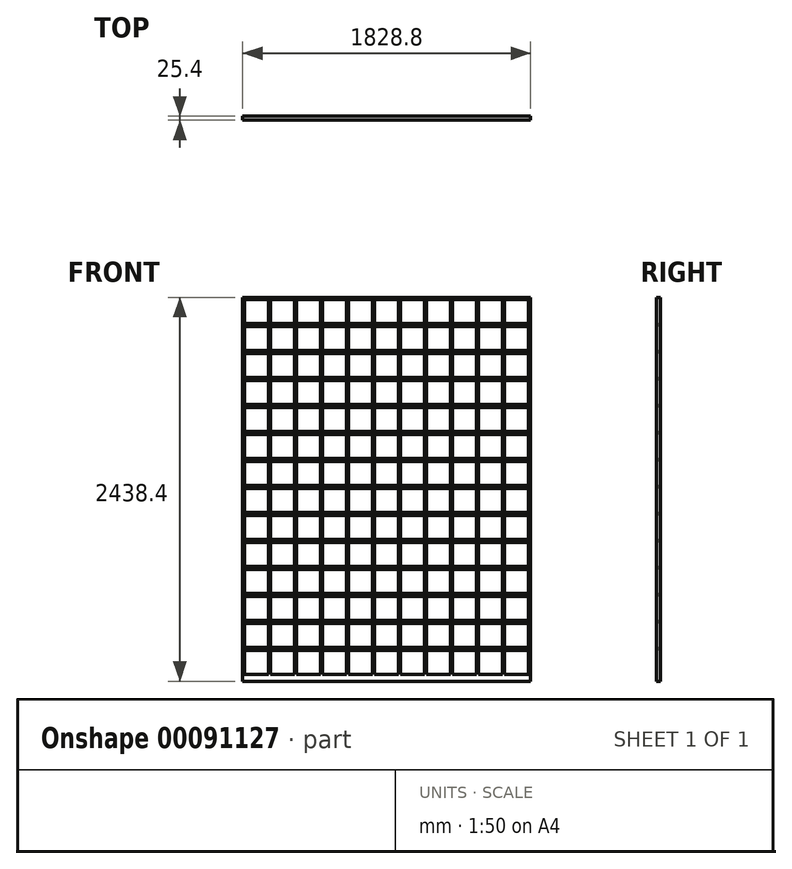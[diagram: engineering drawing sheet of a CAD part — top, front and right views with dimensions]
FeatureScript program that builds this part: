
annotation { "Feature Type Name" : "Feature", "Feature Type Description" : "" }
export const myFeature = defineFeature(function(context is Context, id is Id, definition is map)
    precondition{}
    {
        {
            var Q0;
            Q0=qCreatedBy(makeId("Front.planeOp"),FACE);
            var sketch = newSketch(context, id + "F0", { "sketchPlane" : qUnion([Q0])});
            skLineSegment(sketch, "E0.bottom", {"start": v(-98.4, 2369.27) * mm, "end": v(1730.4, 2369.27) * mm});
            skLineSegment(sketch, "E0.top", {"start": v(-98.4, -69.13) * mm, "end": v(1730.4, -69.13) * mm});
            skLineSegment(sketch, "E0.left", {"start": v(-98.4, 2369.27) * mm, "end": v(-98.4, -69.13) * mm});
            skLineSegment(sketch, "E0.right", {"start": v(1730.4, 2369.27) * mm, "end": v(1730.4, -69.13) * mm});
            skSolve(sketch);
        }
        {
            var Q0;
            Q0 = qSketchRegion(id + "F0", true);
            extrude(context, id + "F1", {"entities" : qUnion([Q0]), "depth" : 25.4 * mm});
        }
        {
            var Q0;
            Q0=makeQuery(id+"F1.opExtrude","CAP_FACE",FACE,{"disambiguationData":[OSD([sQuery(id+"F0.wireOp",EDGE,"E0.bottom"),sQuery(id+"F0.wireOp",EDGE,"E0.top"),sQuery(id+"F0.wireOp",EDGE,"E0.left"),sQuery(id+"F0.wireOp",EDGE,"E0.right")])],"isStart":false});
            var sketch = newSketch(context, id + "F2", { "sketchPlane" : qUnion([Q0])});
            skLineSegment(sketch, "E1.bottom", {"start": v(-85.7, 2356.57) * mm, "end": v(66.7, 2356.57) * mm});
            skLineSegment(sketch, "E1.top", {"start": v(-85.7, 2204.17) * mm, "end": v(66.7, 2204.17) * mm});
            skLineSegment(sketch, "E1.left", {"start": v(-85.7, 2356.57) * mm, "end": v(-85.7, 2204.17) * mm});
            skLineSegment(sketch, "E1.right", {"start": v(66.7, 2356.57) * mm, "end": v(66.7, 2204.17) * mm});
            skLineSegment(sketch, "E2.0.1.0", {"start": v(66.7, 2185.12) * mm, "end": v(66.7, 2032.72) * mm});
            skLineSegment(sketch, "E2.0.1.1", {"start": v(-85.7, 2185.12) * mm, "end": v(66.7, 2185.12) * mm});
            skLineSegment(sketch, "E2.0.1.2", {"start": v(-85.7, 2185.12) * mm, "end": v(-85.7, 2032.72) * mm});
            skLineSegment(sketch, "E2.0.1.3", {"start": v(-85.7, 2032.72) * mm, "end": v(66.7, 2032.72) * mm});
            skLineSegment(sketch, "E2.0.2.0", {"start": v(66.7, 2013.67) * mm, "end": v(66.7, 1861.27) * mm});
            skLineSegment(sketch, "E2.0.2.1", {"start": v(-85.7, 2013.67) * mm, "end": v(66.7, 2013.67) * mm});
            skLineSegment(sketch, "E2.0.2.2", {"start": v(-85.7, 2013.67) * mm, "end": v(-85.7, 1861.27) * mm});
            skLineSegment(sketch, "E2.0.2.3", {"start": v(-85.7, 1861.27) * mm, "end": v(66.7, 1861.27) * mm});
            skLineSegment(sketch, "E2.0.3.0", {"start": v(66.7, 1842.22) * mm, "end": v(66.7, 1689.82) * mm});
            skLineSegment(sketch, "E2.0.3.1", {"start": v(-85.7, 1842.22) * mm, "end": v(66.7, 1842.22) * mm});
            skLineSegment(sketch, "E2.0.3.2", {"start": v(-85.7, 1842.22) * mm, "end": v(-85.7, 1689.82) * mm});
            skLineSegment(sketch, "E2.0.3.3", {"start": v(-85.7, 1689.82) * mm, "end": v(66.7, 1689.82) * mm});
            skLineSegment(sketch, "E2.0.4.0", {"start": v(66.7, 1670.77) * mm, "end": v(66.7, 1518.37) * mm});
            skLineSegment(sketch, "E2.0.4.1", {"start": v(-85.7, 1670.77) * mm, "end": v(66.7, 1670.77) * mm});
            skLineSegment(sketch, "E2.0.4.2", {"start": v(-85.7, 1670.77) * mm, "end": v(-85.7, 1518.37) * mm});
            skLineSegment(sketch, "E2.0.4.3", {"start": v(-85.7, 1518.37) * mm, "end": v(66.7, 1518.37) * mm});
            skLineSegment(sketch, "E2.0.5.0", {"start": v(66.7, 1499.32) * mm, "end": v(66.7, 1346.92) * mm});
            skLineSegment(sketch, "E2.0.5.1", {"start": v(-85.7, 1499.32) * mm, "end": v(66.7, 1499.32) * mm});
            skLineSegment(sketch, "E2.0.5.2", {"start": v(-85.7, 1499.32) * mm, "end": v(-85.7, 1346.92) * mm});
            skLineSegment(sketch, "E2.0.5.3", {"start": v(-85.7, 1346.92) * mm, "end": v(66.7, 1346.92) * mm});
            skLineSegment(sketch, "E2.0.6.0", {"start": v(66.7, 1327.87) * mm, "end": v(66.7, 1175.47) * mm});
            skLineSegment(sketch, "E2.0.6.1", {"start": v(-85.7, 1327.87) * mm, "end": v(66.7, 1327.87) * mm});
            skLineSegment(sketch, "E2.0.6.2", {"start": v(-85.7, 1327.87) * mm, "end": v(-85.7, 1175.47) * mm});
            skLineSegment(sketch, "E2.0.6.3", {"start": v(-85.7, 1175.47) * mm, "end": v(66.7, 1175.47) * mm});
            skLineSegment(sketch, "E2.0.7.0", {"start": v(66.7, 1156.42) * mm, "end": v(66.7, 1004.02) * mm});
            skLineSegment(sketch, "E2.0.7.1", {"start": v(-85.7, 1156.42) * mm, "end": v(66.7, 1156.42) * mm});
            skLineSegment(sketch, "E2.0.7.2", {"start": v(-85.7, 1156.42) * mm, "end": v(-85.7, 1004.02) * mm});
            skLineSegment(sketch, "E2.0.7.3", {"start": v(-85.7, 1004.02) * mm, "end": v(66.7, 1004.02) * mm});
            skLineSegment(sketch, "E2.1.0.0", {"start": v(231.8, 2356.57) * mm, "end": v(231.8, 2204.17) * mm});
            skLineSegment(sketch, "E2.1.0.1", {"start": v(79.4, 2356.57) * mm, "end": v(231.8, 2356.57) * mm});
            skLineSegment(sketch, "E2.1.0.2", {"start": v(79.4, 2356.57) * mm, "end": v(79.4, 2204.17) * mm});
            skLineSegment(sketch, "E2.1.0.3", {"start": v(79.4, 2204.17) * mm, "end": v(231.8, 2204.17) * mm});
            skLineSegment(sketch, "E2.1.1.0", {"start": v(231.8, 2185.12) * mm, "end": v(231.8, 2032.72) * mm});
            skLineSegment(sketch, "E2.1.1.1", {"start": v(79.4, 2185.12) * mm, "end": v(231.8, 2185.12) * mm});
            skLineSegment(sketch, "E2.1.1.2", {"start": v(79.4, 2185.12) * mm, "end": v(79.4, 2032.72) * mm});
            skLineSegment(sketch, "E2.1.1.3", {"start": v(79.4, 2032.72) * mm, "end": v(231.8, 2032.72) * mm});
            skLineSegment(sketch, "E2.1.2.0", {"start": v(231.8, 2013.67) * mm, "end": v(231.8, 1861.27) * mm});
            skLineSegment(sketch, "E2.1.2.1", {"start": v(79.4, 2013.67) * mm, "end": v(231.8, 2013.67) * mm});
            skLineSegment(sketch, "E2.1.2.2", {"start": v(79.4, 2013.67) * mm, "end": v(79.4, 1861.27) * mm});
            skLineSegment(sketch, "E2.1.2.3", {"start": v(79.4, 1861.27) * mm, "end": v(231.8, 1861.27) * mm});
            skLineSegment(sketch, "E2.1.3.0", {"start": v(231.8, 1842.22) * mm, "end": v(231.8, 1689.82) * mm});
            skLineSegment(sketch, "E2.1.3.1", {"start": v(79.4, 1842.22) * mm, "end": v(231.8, 1842.22) * mm});
            skLineSegment(sketch, "E2.1.3.2", {"start": v(79.4, 1842.22) * mm, "end": v(79.4, 1689.82) * mm});
            skLineSegment(sketch, "E2.1.3.3", {"start": v(79.4, 1689.82) * mm, "end": v(231.8, 1689.82) * mm});
            skLineSegment(sketch, "E2.1.4.0", {"start": v(231.8, 1670.77) * mm, "end": v(231.8, 1518.37) * mm});
            skLineSegment(sketch, "E2.1.4.1", {"start": v(79.4, 1670.77) * mm, "end": v(231.8, 1670.77) * mm});
            skLineSegment(sketch, "E2.1.4.2", {"start": v(79.4, 1670.77) * mm, "end": v(79.4, 1518.37) * mm});
            skLineSegment(sketch, "E2.1.4.3", {"start": v(79.4, 1518.37) * mm, "end": v(231.8, 1518.37) * mm});
            skLineSegment(sketch, "E2.1.5.0", {"start": v(231.8, 1499.32) * mm, "end": v(231.8, 1346.92) * mm});
            skLineSegment(sketch, "E2.1.5.1", {"start": v(79.4, 1499.32) * mm, "end": v(231.8, 1499.32) * mm});
            skLineSegment(sketch, "E2.1.5.2", {"start": v(79.4, 1499.32) * mm, "end": v(79.4, 1346.92) * mm});
            skLineSegment(sketch, "E2.1.5.3", {"start": v(79.4, 1346.92) * mm, "end": v(231.8, 1346.92) * mm});
            skLineSegment(sketch, "E2.1.6.0", {"start": v(231.8, 1327.87) * mm, "end": v(231.8, 1175.47) * mm});
            skLineSegment(sketch, "E2.1.6.1", {"start": v(79.4, 1327.87) * mm, "end": v(231.8, 1327.87) * mm});
            skLineSegment(sketch, "E2.1.6.2", {"start": v(79.4, 1327.87) * mm, "end": v(79.4, 1175.47) * mm});
            skLineSegment(sketch, "E2.1.6.3", {"start": v(79.4, 1175.47) * mm, "end": v(231.8, 1175.47) * mm});
            skLineSegment(sketch, "E2.1.7.0", {"start": v(231.8, 1156.42) * mm, "end": v(231.8, 1004.02) * mm});
            skLineSegment(sketch, "E2.1.7.1", {"start": v(79.4, 1156.42) * mm, "end": v(231.8, 1156.42) * mm});
            skLineSegment(sketch, "E2.1.7.2", {"start": v(79.4, 1156.42) * mm, "end": v(79.4, 1004.02) * mm});
            skLineSegment(sketch, "E2.1.7.3", {"start": v(79.4, 1004.02) * mm, "end": v(231.8, 1004.02) * mm});
            skLineSegment(sketch, "E2.2.0.0", {"start": v(396.9, 2356.57) * mm, "end": v(396.9, 2204.17) * mm});
            skLineSegment(sketch, "E2.2.0.1", {"start": v(244.5, 2356.57) * mm, "end": v(396.9, 2356.57) * mm});
            skLineSegment(sketch, "E2.2.0.2", {"start": v(244.5, 2356.57) * mm, "end": v(244.5, 2204.17) * mm});
            skLineSegment(sketch, "E2.2.0.3", {"start": v(244.5, 2204.17) * mm, "end": v(396.9, 2204.17) * mm});
            skLineSegment(sketch, "E2.2.1.0", {"start": v(396.9, 2185.12) * mm, "end": v(396.9, 2032.72) * mm});
            skLineSegment(sketch, "E2.2.1.1", {"start": v(244.5, 2185.12) * mm, "end": v(396.9, 2185.12) * mm});
            skLineSegment(sketch, "E2.2.1.2", {"start": v(244.5, 2185.12) * mm, "end": v(244.5, 2032.72) * mm});
            skLineSegment(sketch, "E2.2.1.3", {"start": v(244.5, 2032.72) * mm, "end": v(396.9, 2032.72) * mm});
            skLineSegment(sketch, "E2.2.2.0", {"start": v(396.9, 2013.67) * mm, "end": v(396.9, 1861.27) * mm});
            skLineSegment(sketch, "E2.2.2.1", {"start": v(244.5, 2013.67) * mm, "end": v(396.9, 2013.67) * mm});
            skLineSegment(sketch, "E2.2.2.2", {"start": v(244.5, 2013.67) * mm, "end": v(244.5, 1861.27) * mm});
            skLineSegment(sketch, "E2.2.2.3", {"start": v(244.5, 1861.27) * mm, "end": v(396.9, 1861.27) * mm});
            skLineSegment(sketch, "E2.2.3.0", {"start": v(396.9, 1842.22) * mm, "end": v(396.9, 1689.82) * mm});
            skLineSegment(sketch, "E2.2.3.1", {"start": v(244.5, 1842.22) * mm, "end": v(396.9, 1842.22) * mm});
            skLineSegment(sketch, "E2.2.3.2", {"start": v(244.5, 1842.22) * mm, "end": v(244.5, 1689.82) * mm});
            skLineSegment(sketch, "E2.2.3.3", {"start": v(244.5, 1689.82) * mm, "end": v(396.9, 1689.82) * mm});
            skLineSegment(sketch, "E2.2.4.0", {"start": v(396.9, 1670.77) * mm, "end": v(396.9, 1518.37) * mm});
            skLineSegment(sketch, "E2.2.4.1", {"start": v(244.5, 1670.77) * mm, "end": v(396.9, 1670.77) * mm});
            skLineSegment(sketch, "E2.2.4.2", {"start": v(244.5, 1670.77) * mm, "end": v(244.5, 1518.37) * mm});
            skLineSegment(sketch, "E2.2.4.3", {"start": v(244.5, 1518.37) * mm, "end": v(396.9, 1518.37) * mm});
            skLineSegment(sketch, "E2.2.5.0", {"start": v(396.9, 1499.32) * mm, "end": v(396.9, 1346.92) * mm});
            skLineSegment(sketch, "E2.2.5.1", {"start": v(244.5, 1499.32) * mm, "end": v(396.9, 1499.32) * mm});
            skLineSegment(sketch, "E2.2.5.2", {"start": v(244.5, 1499.32) * mm, "end": v(244.5, 1346.92) * mm});
            skLineSegment(sketch, "E2.2.5.3", {"start": v(244.5, 1346.92) * mm, "end": v(396.9, 1346.92) * mm});
            skLineSegment(sketch, "E2.2.6.0", {"start": v(396.9, 1327.87) * mm, "end": v(396.9, 1175.47) * mm});
            skLineSegment(sketch, "E2.2.6.1", {"start": v(244.5, 1327.87) * mm, "end": v(396.9, 1327.87) * mm});
            skLineSegment(sketch, "E2.2.6.2", {"start": v(244.5, 1327.87) * mm, "end": v(244.5, 1175.47) * mm});
            skLineSegment(sketch, "E2.2.6.3", {"start": v(244.5, 1175.47) * mm, "end": v(396.9, 1175.47) * mm});
            skLineSegment(sketch, "E2.2.7.0", {"start": v(396.9, 1156.42) * mm, "end": v(396.9, 1004.02) * mm});
            skLineSegment(sketch, "E2.2.7.1", {"start": v(244.5, 1156.42) * mm, "end": v(396.9, 1156.42) * mm});
            skLineSegment(sketch, "E2.2.7.2", {"start": v(244.5, 1156.42) * mm, "end": v(244.5, 1004.02) * mm});
            skLineSegment(sketch, "E2.2.7.3", {"start": v(244.5, 1004.02) * mm, "end": v(396.9, 1004.02) * mm});
            skLineSegment(sketch, "E2.3.0.0", {"start": v(562, 2356.57) * mm, "end": v(562, 2204.17) * mm});
            skLineSegment(sketch, "E2.3.0.1", {"start": v(409.6, 2356.57) * mm, "end": v(562, 2356.57) * mm});
            skLineSegment(sketch, "E2.3.0.2", {"start": v(409.6, 2356.57) * mm, "end": v(409.6, 2204.17) * mm});
            skLineSegment(sketch, "E2.3.0.3", {"start": v(409.6, 2204.17) * mm, "end": v(562, 2204.17) * mm});
            skLineSegment(sketch, "E2.3.1.0", {"start": v(562, 2185.12) * mm, "end": v(562, 2032.72) * mm});
            skLineSegment(sketch, "E2.3.1.1", {"start": v(409.6, 2185.12) * mm, "end": v(562, 2185.12) * mm});
            skLineSegment(sketch, "E2.3.1.2", {"start": v(409.6, 2185.12) * mm, "end": v(409.6, 2032.72) * mm});
            skLineSegment(sketch, "E2.3.1.3", {"start": v(409.6, 2032.72) * mm, "end": v(562, 2032.72) * mm});
            skLineSegment(sketch, "E2.3.2.0", {"start": v(562, 2013.67) * mm, "end": v(562, 1861.27) * mm});
            skLineSegment(sketch, "E2.3.2.1", {"start": v(409.6, 2013.67) * mm, "end": v(562, 2013.67) * mm});
            skLineSegment(sketch, "E2.3.2.2", {"start": v(409.6, 2013.67) * mm, "end": v(409.6, 1861.27) * mm});
            skLineSegment(sketch, "E2.3.2.3", {"start": v(409.6, 1861.27) * mm, "end": v(562, 1861.27) * mm});
            skLineSegment(sketch, "E2.3.3.0", {"start": v(562, 1842.22) * mm, "end": v(562, 1689.82) * mm});
            skLineSegment(sketch, "E2.3.3.1", {"start": v(409.6, 1842.22) * mm, "end": v(562, 1842.22) * mm});
            skLineSegment(sketch, "E2.3.3.2", {"start": v(409.6, 1842.22) * mm, "end": v(409.6, 1689.82) * mm});
            skLineSegment(sketch, "E2.3.3.3", {"start": v(409.6, 1689.82) * mm, "end": v(562, 1689.82) * mm});
            skLineSegment(sketch, "E2.3.4.0", {"start": v(562, 1670.77) * mm, "end": v(562, 1518.37) * mm});
            skLineSegment(sketch, "E2.3.4.1", {"start": v(409.6, 1670.77) * mm, "end": v(562, 1670.77) * mm});
            skLineSegment(sketch, "E2.3.4.2", {"start": v(409.6, 1670.77) * mm, "end": v(409.6, 1518.37) * mm});
            skLineSegment(sketch, "E2.3.4.3", {"start": v(409.6, 1518.37) * mm, "end": v(562, 1518.37) * mm});
            skLineSegment(sketch, "E2.3.5.0", {"start": v(562, 1499.32) * mm, "end": v(562, 1346.92) * mm});
            skLineSegment(sketch, "E2.3.5.1", {"start": v(409.6, 1499.32) * mm, "end": v(562, 1499.32) * mm});
            skLineSegment(sketch, "E2.3.5.2", {"start": v(409.6, 1499.32) * mm, "end": v(409.6, 1346.92) * mm});
            skLineSegment(sketch, "E2.3.5.3", {"start": v(409.6, 1346.92) * mm, "end": v(562, 1346.92) * mm});
            skLineSegment(sketch, "E2.3.6.0", {"start": v(562, 1327.87) * mm, "end": v(562, 1175.47) * mm});
            skLineSegment(sketch, "E2.3.6.1", {"start": v(409.6, 1327.87) * mm, "end": v(562, 1327.87) * mm});
            skLineSegment(sketch, "E2.3.6.2", {"start": v(409.6, 1327.87) * mm, "end": v(409.6, 1175.47) * mm});
            skLineSegment(sketch, "E2.3.6.3", {"start": v(409.6, 1175.47) * mm, "end": v(562, 1175.47) * mm});
            skLineSegment(sketch, "E2.3.7.0", {"start": v(562, 1156.42) * mm, "end": v(562, 1004.02) * mm});
            skLineSegment(sketch, "E2.3.7.1", {"start": v(409.6, 1156.42) * mm, "end": v(562, 1156.42) * mm});
            skLineSegment(sketch, "E2.3.7.2", {"start": v(409.6, 1156.42) * mm, "end": v(409.6, 1004.02) * mm});
            skLineSegment(sketch, "E2.3.7.3", {"start": v(409.6, 1004.02) * mm, "end": v(562, 1004.02) * mm});
            skLineSegment(sketch, "E2.4.0.0", {"start": v(727.1, 2356.57) * mm, "end": v(727.1, 2204.17) * mm});
            skLineSegment(sketch, "E2.4.0.1", {"start": v(574.7, 2356.57) * mm, "end": v(727.1, 2356.57) * mm});
            skLineSegment(sketch, "E2.4.0.2", {"start": v(574.7, 2356.57) * mm, "end": v(574.7, 2204.17) * mm});
            skLineSegment(sketch, "E2.4.0.3", {"start": v(574.7, 2204.17) * mm, "end": v(727.1, 2204.17) * mm});
            skLineSegment(sketch, "E2.4.1.0", {"start": v(727.1, 2185.12) * mm, "end": v(727.1, 2032.72) * mm});
            skLineSegment(sketch, "E2.4.1.1", {"start": v(574.7, 2185.12) * mm, "end": v(727.1, 2185.12) * mm});
            skLineSegment(sketch, "E2.4.1.2", {"start": v(574.7, 2185.12) * mm, "end": v(574.7, 2032.72) * mm});
            skLineSegment(sketch, "E2.4.1.3", {"start": v(574.7, 2032.72) * mm, "end": v(727.1, 2032.72) * mm});
            skLineSegment(sketch, "E2.4.2.0", {"start": v(727.1, 2013.67) * mm, "end": v(727.1, 1861.27) * mm});
            skLineSegment(sketch, "E2.4.2.1", {"start": v(574.7, 2013.67) * mm, "end": v(727.1, 2013.67) * mm});
            skLineSegment(sketch, "E2.4.2.2", {"start": v(574.7, 2013.67) * mm, "end": v(574.7, 1861.27) * mm});
            skLineSegment(sketch, "E2.4.2.3", {"start": v(574.7, 1861.27) * mm, "end": v(727.1, 1861.27) * mm});
            skLineSegment(sketch, "E2.4.3.0", {"start": v(727.1, 1842.22) * mm, "end": v(727.1, 1689.82) * mm});
            skLineSegment(sketch, "E2.4.3.1", {"start": v(574.7, 1842.22) * mm, "end": v(727.1, 1842.22) * mm});
            skLineSegment(sketch, "E2.4.3.2", {"start": v(574.7, 1842.22) * mm, "end": v(574.7, 1689.82) * mm});
            skLineSegment(sketch, "E2.4.3.3", {"start": v(574.7, 1689.82) * mm, "end": v(727.1, 1689.82) * mm});
            skLineSegment(sketch, "E2.4.4.0", {"start": v(727.1, 1670.77) * mm, "end": v(727.1, 1518.37) * mm});
            skLineSegment(sketch, "E2.4.4.1", {"start": v(574.7, 1670.77) * mm, "end": v(727.1, 1670.77) * mm});
            skLineSegment(sketch, "E2.4.4.2", {"start": v(574.7, 1670.77) * mm, "end": v(574.7, 1518.37) * mm});
            skLineSegment(sketch, "E2.4.4.3", {"start": v(574.7, 1518.37) * mm, "end": v(727.1, 1518.37) * mm});
            skLineSegment(sketch, "E2.4.5.0", {"start": v(727.1, 1499.32) * mm, "end": v(727.1, 1346.92) * mm});
            skLineSegment(sketch, "E2.4.5.1", {"start": v(574.7, 1499.32) * mm, "end": v(727.1, 1499.32) * mm});
            skLineSegment(sketch, "E2.4.5.2", {"start": v(574.7, 1499.32) * mm, "end": v(574.7, 1346.92) * mm});
            skLineSegment(sketch, "E2.4.5.3", {"start": v(574.7, 1346.92) * mm, "end": v(727.1, 1346.92) * mm});
            skLineSegment(sketch, "E2.4.6.0", {"start": v(727.1, 1327.87) * mm, "end": v(727.1, 1175.47) * mm});
            skLineSegment(sketch, "E2.4.6.1", {"start": v(574.7, 1327.87) * mm, "end": v(727.1, 1327.87) * mm});
            skLineSegment(sketch, "E2.4.6.2", {"start": v(574.7, 1327.87) * mm, "end": v(574.7, 1175.47) * mm});
            skLineSegment(sketch, "E2.4.6.3", {"start": v(574.7, 1175.47) * mm, "end": v(727.1, 1175.47) * mm});
            skLineSegment(sketch, "E2.4.7.0", {"start": v(727.1, 1156.42) * mm, "end": v(727.1, 1004.02) * mm});
            skLineSegment(sketch, "E2.4.7.1", {"start": v(574.7, 1156.42) * mm, "end": v(727.1, 1156.42) * mm});
            skLineSegment(sketch, "E2.4.7.2", {"start": v(574.7, 1156.42) * mm, "end": v(574.7, 1004.02) * mm});
            skLineSegment(sketch, "E2.4.7.3", {"start": v(574.7, 1004.02) * mm, "end": v(727.1, 1004.02) * mm});
            skLineSegment(sketch, "E2.5.0.0", {"start": v(892.2, 2356.57) * mm, "end": v(892.2, 2204.17) * mm});
            skLineSegment(sketch, "E2.5.0.1", {"start": v(739.8, 2356.57) * mm, "end": v(892.2, 2356.57) * mm});
            skLineSegment(sketch, "E2.5.0.2", {"start": v(739.8, 2356.57) * mm, "end": v(739.8, 2204.17) * mm});
            skLineSegment(sketch, "E2.5.0.3", {"start": v(739.8, 2204.17) * mm, "end": v(892.2, 2204.17) * mm});
            skLineSegment(sketch, "E2.5.1.0", {"start": v(892.2, 2185.12) * mm, "end": v(892.2, 2032.72) * mm});
            skLineSegment(sketch, "E2.5.1.1", {"start": v(739.8, 2185.12) * mm, "end": v(892.2, 2185.12) * mm});
            skLineSegment(sketch, "E2.5.1.2", {"start": v(739.8, 2185.12) * mm, "end": v(739.8, 2032.72) * mm});
            skLineSegment(sketch, "E2.5.1.3", {"start": v(739.8, 2032.72) * mm, "end": v(892.2, 2032.72) * mm});
            skLineSegment(sketch, "E2.5.2.0", {"start": v(892.2, 2013.67) * mm, "end": v(892.2, 1861.27) * mm});
            skLineSegment(sketch, "E2.5.2.1", {"start": v(739.8, 2013.67) * mm, "end": v(892.2, 2013.67) * mm});
            skLineSegment(sketch, "E2.5.2.2", {"start": v(739.8, 2013.67) * mm, "end": v(739.8, 1861.27) * mm});
            skLineSegment(sketch, "E2.5.2.3", {"start": v(739.8, 1861.27) * mm, "end": v(892.2, 1861.27) * mm});
            skLineSegment(sketch, "E2.5.3.0", {"start": v(892.2, 1842.22) * mm, "end": v(892.2, 1689.82) * mm});
            skLineSegment(sketch, "E2.5.3.1", {"start": v(739.8, 1842.22) * mm, "end": v(892.2, 1842.22) * mm});
            skLineSegment(sketch, "E2.5.3.2", {"start": v(739.8, 1842.22) * mm, "end": v(739.8, 1689.82) * mm});
            skLineSegment(sketch, "E2.5.3.3", {"start": v(739.8, 1689.82) * mm, "end": v(892.2, 1689.82) * mm});
            skLineSegment(sketch, "E2.5.4.0", {"start": v(892.2, 1670.77) * mm, "end": v(892.2, 1518.37) * mm});
            skLineSegment(sketch, "E2.5.4.1", {"start": v(739.8, 1670.77) * mm, "end": v(892.2, 1670.77) * mm});
            skLineSegment(sketch, "E2.5.4.2", {"start": v(739.8, 1670.77) * mm, "end": v(739.8, 1518.37) * mm});
            skLineSegment(sketch, "E2.5.4.3", {"start": v(739.8, 1518.37) * mm, "end": v(892.2, 1518.37) * mm});
            skLineSegment(sketch, "E2.5.5.0", {"start": v(892.2, 1499.32) * mm, "end": v(892.2, 1346.92) * mm});
            skLineSegment(sketch, "E2.5.5.1", {"start": v(739.8, 1499.32) * mm, "end": v(892.2, 1499.32) * mm});
            skLineSegment(sketch, "E2.5.5.2", {"start": v(739.8, 1499.32) * mm, "end": v(739.8, 1346.92) * mm});
            skLineSegment(sketch, "E2.5.5.3", {"start": v(739.8, 1346.92) * mm, "end": v(892.2, 1346.92) * mm});
            skLineSegment(sketch, "E2.5.6.0", {"start": v(892.2, 1327.87) * mm, "end": v(892.2, 1175.47) * mm});
            skLineSegment(sketch, "E2.5.6.1", {"start": v(739.8, 1327.87) * mm, "end": v(892.2, 1327.87) * mm});
            skLineSegment(sketch, "E2.5.6.2", {"start": v(739.8, 1327.87) * mm, "end": v(739.8, 1175.47) * mm});
            skLineSegment(sketch, "E2.5.6.3", {"start": v(739.8, 1175.47) * mm, "end": v(892.2, 1175.47) * mm});
            skLineSegment(sketch, "E2.5.7.0", {"start": v(892.2, 1156.42) * mm, "end": v(892.2, 1004.02) * mm});
            skLineSegment(sketch, "E2.5.7.1", {"start": v(739.8, 1156.42) * mm, "end": v(892.2, 1156.42) * mm});
            skLineSegment(sketch, "E2.5.7.2", {"start": v(739.8, 1156.42) * mm, "end": v(739.8, 1004.02) * mm});
            skLineSegment(sketch, "E2.5.7.3", {"start": v(739.8, 1004.02) * mm, "end": v(892.2, 1004.02) * mm});
            skLineSegment(sketch, "E2.direction1", {"start": v(66.7, 2204.17) * mm, "end": v(231.8, 2204.17) * mm, "construction": true});
            skLineSegment(sketch, "E2.direction2", {"start": v(66.7, 2204.17) * mm, "end": v(66.7, 2032.72) * mm, "construction": true});
            skLineSegment(sketch, "E3.0.6.0", {"start": v(1057.3, 2356.57) * mm, "end": v(1057.3, 2204.17) * mm});
            skLineSegment(sketch, "E3.3.6.0", {"start": v(904.9, 2356.57) * mm, "end": v(1057.3, 2356.57) * mm});
            skLineSegment(sketch, "E3.6.6.0", {"start": v(904.9, 2356.57) * mm, "end": v(904.9, 2204.17) * mm});
            skLineSegment(sketch, "E3.9.6.0", {"start": v(904.9, 2204.17) * mm, "end": v(1057.3, 2204.17) * mm});
            skLineSegment(sketch, "E3.0.6.1", {"start": v(1057.3, 2185.12) * mm, "end": v(1057.3, 2032.72) * mm});
            skLineSegment(sketch, "E3.3.6.1", {"start": v(904.9, 2185.12) * mm, "end": v(1057.3, 2185.12) * mm});
            skLineSegment(sketch, "E3.6.6.1", {"start": v(904.9, 2185.12) * mm, "end": v(904.9, 2032.72) * mm});
            skLineSegment(sketch, "E3.9.6.1", {"start": v(904.9, 2032.72) * mm, "end": v(1057.3, 2032.72) * mm});
            skLineSegment(sketch, "E3.0.6.2", {"start": v(1057.3, 2013.67) * mm, "end": v(1057.3, 1861.27) * mm});
            skLineSegment(sketch, "E3.3.6.2", {"start": v(904.9, 2013.67) * mm, "end": v(1057.3, 2013.67) * mm});
            skLineSegment(sketch, "E3.6.6.2", {"start": v(904.9, 2013.67) * mm, "end": v(904.9, 1861.27) * mm});
            skLineSegment(sketch, "E3.9.6.2", {"start": v(904.9, 1861.27) * mm, "end": v(1057.3, 1861.27) * mm});
            skLineSegment(sketch, "E3.0.6.3", {"start": v(1057.3, 1842.22) * mm, "end": v(1057.3, 1689.82) * mm});
            skLineSegment(sketch, "E3.3.6.3", {"start": v(904.9, 1842.22) * mm, "end": v(1057.3, 1842.22) * mm});
            skLineSegment(sketch, "E3.6.6.3", {"start": v(904.9, 1842.22) * mm, "end": v(904.9, 1689.82) * mm});
            skLineSegment(sketch, "E3.9.6.3", {"start": v(904.9, 1689.82) * mm, "end": v(1057.3, 1689.82) * mm});
            skLineSegment(sketch, "E3.0.6.4", {"start": v(1057.3, 1670.77) * mm, "end": v(1057.3, 1518.37) * mm});
            skLineSegment(sketch, "E3.3.6.4", {"start": v(904.9, 1670.77) * mm, "end": v(1057.3, 1670.77) * mm});
            skLineSegment(sketch, "E3.6.6.4", {"start": v(904.9, 1670.77) * mm, "end": v(904.9, 1518.37) * mm});
            skLineSegment(sketch, "E3.9.6.4", {"start": v(904.9, 1518.37) * mm, "end": v(1057.3, 1518.37) * mm});
            skLineSegment(sketch, "E3.0.6.5", {"start": v(1057.3, 1499.32) * mm, "end": v(1057.3, 1346.92) * mm});
            skLineSegment(sketch, "E3.3.6.5", {"start": v(904.9, 1499.32) * mm, "end": v(1057.3, 1499.32) * mm});
            skLineSegment(sketch, "E3.6.6.5", {"start": v(904.9, 1499.32) * mm, "end": v(904.9, 1346.92) * mm});
            skLineSegment(sketch, "E3.9.6.5", {"start": v(904.9, 1346.92) * mm, "end": v(1057.3, 1346.92) * mm});
            skLineSegment(sketch, "E3.0.6.6", {"start": v(1057.3, 1327.87) * mm, "end": v(1057.3, 1175.47) * mm});
            skLineSegment(sketch, "E3.3.6.6", {"start": v(904.9, 1327.87) * mm, "end": v(1057.3, 1327.87) * mm});
            skLineSegment(sketch, "E3.6.6.6", {"start": v(904.9, 1327.87) * mm, "end": v(904.9, 1175.47) * mm});
            skLineSegment(sketch, "E3.9.6.6", {"start": v(904.9, 1175.47) * mm, "end": v(1057.3, 1175.47) * mm});
            skLineSegment(sketch, "E3.0.6.7", {"start": v(1057.3, 1156.42) * mm, "end": v(1057.3, 1004.02) * mm});
            skLineSegment(sketch, "E3.3.6.7", {"start": v(904.9, 1156.42) * mm, "end": v(1057.3, 1156.42) * mm});
            skLineSegment(sketch, "E3.6.6.7", {"start": v(904.9, 1156.42) * mm, "end": v(904.9, 1004.02) * mm});
            skLineSegment(sketch, "E3.9.6.7", {"start": v(904.9, 1004.02) * mm, "end": v(1057.3, 1004.02) * mm});
            skLineSegment(sketch, "E4.0.0.8", {"start": v(66.7, 984.97) * mm, "end": v(66.7, 832.57) * mm});
            skLineSegment(sketch, "E4.3.0.8", {"start": v(-85.7, 984.97) * mm, "end": v(66.7, 984.97) * mm});
            skLineSegment(sketch, "E4.6.0.8", {"start": v(-85.7, 984.97) * mm, "end": v(-85.7, 832.57) * mm});
            skLineSegment(sketch, "E4.9.0.8", {"start": v(-85.7, 832.57) * mm, "end": v(66.7, 832.57) * mm});
            skLineSegment(sketch, "E4.0.1.8", {"start": v(231.8, 984.97) * mm, "end": v(231.8, 832.57) * mm});
            skLineSegment(sketch, "E4.3.1.8", {"start": v(79.4, 984.97) * mm, "end": v(231.8, 984.97) * mm});
            skLineSegment(sketch, "E4.6.1.8", {"start": v(79.4, 984.97) * mm, "end": v(79.4, 832.57) * mm});
            skLineSegment(sketch, "E4.9.1.8", {"start": v(79.4, 832.57) * mm, "end": v(231.8, 832.57) * mm});
            skLineSegment(sketch, "E4.0.2.8", {"start": v(396.9, 984.97) * mm, "end": v(396.9, 832.57) * mm});
            skLineSegment(sketch, "E4.3.2.8", {"start": v(244.5, 984.97) * mm, "end": v(396.9, 984.97) * mm});
            skLineSegment(sketch, "E4.6.2.8", {"start": v(244.5, 984.97) * mm, "end": v(244.5, 832.57) * mm});
            skLineSegment(sketch, "E4.9.2.8", {"start": v(244.5, 832.57) * mm, "end": v(396.9, 832.57) * mm});
            skLineSegment(sketch, "E4.0.3.8", {"start": v(562, 984.97) * mm, "end": v(562, 832.57) * mm});
            skLineSegment(sketch, "E4.3.3.8", {"start": v(409.6, 984.97) * mm, "end": v(562, 984.97) * mm});
            skLineSegment(sketch, "E4.6.3.8", {"start": v(409.6, 984.97) * mm, "end": v(409.6, 832.57) * mm});
            skLineSegment(sketch, "E4.9.3.8", {"start": v(409.6, 832.57) * mm, "end": v(562, 832.57) * mm});
            skLineSegment(sketch, "E4.0.4.8", {"start": v(727.1, 984.97) * mm, "end": v(727.1, 832.57) * mm});
            skLineSegment(sketch, "E4.3.4.8", {"start": v(574.7, 984.97) * mm, "end": v(727.1, 984.97) * mm});
            skLineSegment(sketch, "E4.6.4.8", {"start": v(574.7, 984.97) * mm, "end": v(574.7, 832.57) * mm});
            skLineSegment(sketch, "E4.9.4.8", {"start": v(574.7, 832.57) * mm, "end": v(727.1, 832.57) * mm});
            skLineSegment(sketch, "E4.0.5.8", {"start": v(892.2, 984.97) * mm, "end": v(892.2, 832.57) * mm});
            skLineSegment(sketch, "E4.3.5.8", {"start": v(739.8, 984.97) * mm, "end": v(892.2, 984.97) * mm});
            skLineSegment(sketch, "E4.6.5.8", {"start": v(739.8, 984.97) * mm, "end": v(739.8, 832.57) * mm});
            skLineSegment(sketch, "E4.9.5.8", {"start": v(739.8, 832.57) * mm, "end": v(892.2, 832.57) * mm});
            skLineSegment(sketch, "E4.0.6.8", {"start": v(1057.3, 984.97) * mm, "end": v(1057.3, 832.57) * mm});
            skLineSegment(sketch, "E4.3.6.8", {"start": v(904.9, 984.97) * mm, "end": v(1057.3, 984.97) * mm});
            skLineSegment(sketch, "E4.6.6.8", {"start": v(904.9, 984.97) * mm, "end": v(904.9, 832.57) * mm});
            skLineSegment(sketch, "E4.9.6.8", {"start": v(904.9, 832.57) * mm, "end": v(1057.3, 832.57) * mm});
            skLineSegment(sketch, "E5.0.7.0", {"start": v(1222.4, 2356.57) * mm, "end": v(1222.4, 2204.17) * mm});
            skLineSegment(sketch, "E5.3.7.0", {"start": v(1070, 2356.57) * mm, "end": v(1222.4, 2356.57) * mm});
            skLineSegment(sketch, "E5.6.7.0", {"start": v(1070, 2356.57) * mm, "end": v(1070, 2204.17) * mm});
            skLineSegment(sketch, "E5.9.7.0", {"start": v(1070, 2204.17) * mm, "end": v(1222.4, 2204.17) * mm});
            skLineSegment(sketch, "E5.0.7.1", {"start": v(1222.4, 2185.12) * mm, "end": v(1222.4, 2032.72) * mm});
            skLineSegment(sketch, "E5.3.7.1", {"start": v(1070, 2185.12) * mm, "end": v(1222.4, 2185.12) * mm});
            skLineSegment(sketch, "E5.6.7.1", {"start": v(1070, 2185.12) * mm, "end": v(1070, 2032.72) * mm});
            skLineSegment(sketch, "E5.9.7.1", {"start": v(1070, 2032.72) * mm, "end": v(1222.4, 2032.72) * mm});
            skLineSegment(sketch, "E5.0.7.2", {"start": v(1222.4, 2013.67) * mm, "end": v(1222.4, 1861.27) * mm});
            skLineSegment(sketch, "E5.3.7.2", {"start": v(1070, 2013.67) * mm, "end": v(1222.4, 2013.67) * mm});
            skLineSegment(sketch, "E5.6.7.2", {"start": v(1070, 2013.67) * mm, "end": v(1070, 1861.27) * mm});
            skLineSegment(sketch, "E5.9.7.2", {"start": v(1070, 1861.27) * mm, "end": v(1222.4, 1861.27) * mm});
            skLineSegment(sketch, "E5.0.7.3", {"start": v(1222.4, 1842.22) * mm, "end": v(1222.4, 1689.82) * mm});
            skLineSegment(sketch, "E5.3.7.3", {"start": v(1070, 1842.22) * mm, "end": v(1222.4, 1842.22) * mm});
            skLineSegment(sketch, "E5.6.7.3", {"start": v(1070, 1842.22) * mm, "end": v(1070, 1689.82) * mm});
            skLineSegment(sketch, "E5.9.7.3", {"start": v(1070, 1689.82) * mm, "end": v(1222.4, 1689.82) * mm});
            skLineSegment(sketch, "E5.0.7.4", {"start": v(1222.4, 1670.77) * mm, "end": v(1222.4, 1518.37) * mm});
            skLineSegment(sketch, "E5.3.7.4", {"start": v(1070, 1670.77) * mm, "end": v(1222.4, 1670.77) * mm});
            skLineSegment(sketch, "E5.6.7.4", {"start": v(1070, 1670.77) * mm, "end": v(1070, 1518.37) * mm});
            skLineSegment(sketch, "E5.9.7.4", {"start": v(1070, 1518.37) * mm, "end": v(1222.4, 1518.37) * mm});
            skLineSegment(sketch, "E5.0.7.5", {"start": v(1222.4, 1499.32) * mm, "end": v(1222.4, 1346.92) * mm});
            skLineSegment(sketch, "E5.3.7.5", {"start": v(1070, 1499.32) * mm, "end": v(1222.4, 1499.32) * mm});
            skLineSegment(sketch, "E5.6.7.5", {"start": v(1070, 1499.32) * mm, "end": v(1070, 1346.92) * mm});
            skLineSegment(sketch, "E5.9.7.5", {"start": v(1070, 1346.92) * mm, "end": v(1222.4, 1346.92) * mm});
            skLineSegment(sketch, "E5.0.7.6", {"start": v(1222.4, 1327.87) * mm, "end": v(1222.4, 1175.47) * mm});
            skLineSegment(sketch, "E5.3.7.6", {"start": v(1070, 1327.87) * mm, "end": v(1222.4, 1327.87) * mm});
            skLineSegment(sketch, "E5.6.7.6", {"start": v(1070, 1327.87) * mm, "end": v(1070, 1175.47) * mm});
            skLineSegment(sketch, "E5.9.7.6", {"start": v(1070, 1175.47) * mm, "end": v(1222.4, 1175.47) * mm});
            skLineSegment(sketch, "E5.0.7.7", {"start": v(1222.4, 1156.42) * mm, "end": v(1222.4, 1004.02) * mm});
            skLineSegment(sketch, "E5.3.7.7", {"start": v(1070, 1156.42) * mm, "end": v(1222.4, 1156.42) * mm});
            skLineSegment(sketch, "E5.6.7.7", {"start": v(1070, 1156.42) * mm, "end": v(1070, 1004.02) * mm});
            skLineSegment(sketch, "E5.9.7.7", {"start": v(1070, 1004.02) * mm, "end": v(1222.4, 1004.02) * mm});
            skLineSegment(sketch, "E5.0.7.8", {"start": v(1222.4, 984.97) * mm, "end": v(1222.4, 832.57) * mm});
            skLineSegment(sketch, "E5.3.7.8", {"start": v(1070, 984.97) * mm, "end": v(1222.4, 984.97) * mm});
            skLineSegment(sketch, "E5.6.7.8", {"start": v(1070, 984.97) * mm, "end": v(1070, 832.57) * mm});
            skLineSegment(sketch, "E5.9.7.8", {"start": v(1070, 832.57) * mm, "end": v(1222.4, 832.57) * mm});
            skLineSegment(sketch, "E5.0.8.0", {"start": v(1387.5, 2356.57) * mm, "end": v(1387.5, 2204.17) * mm});
            skLineSegment(sketch, "E5.3.8.0", {"start": v(1235.1, 2356.57) * mm, "end": v(1387.5, 2356.57) * mm});
            skLineSegment(sketch, "E5.6.8.0", {"start": v(1235.1, 2356.57) * mm, "end": v(1235.1, 2204.17) * mm});
            skLineSegment(sketch, "E5.9.8.0", {"start": v(1235.1, 2204.17) * mm, "end": v(1387.5, 2204.17) * mm});
            skLineSegment(sketch, "E5.0.8.1", {"start": v(1387.5, 2185.12) * mm, "end": v(1387.5, 2032.72) * mm});
            skLineSegment(sketch, "E5.3.8.1", {"start": v(1235.1, 2185.12) * mm, "end": v(1387.5, 2185.12) * mm});
            skLineSegment(sketch, "E5.6.8.1", {"start": v(1235.1, 2185.12) * mm, "end": v(1235.1, 2032.72) * mm});
            skLineSegment(sketch, "E5.9.8.1", {"start": v(1235.1, 2032.72) * mm, "end": v(1387.5, 2032.72) * mm});
            skLineSegment(sketch, "E5.0.8.2", {"start": v(1387.5, 2013.67) * mm, "end": v(1387.5, 1861.27) * mm});
            skLineSegment(sketch, "E5.3.8.2", {"start": v(1235.1, 2013.67) * mm, "end": v(1387.5, 2013.67) * mm});
            skLineSegment(sketch, "E5.6.8.2", {"start": v(1235.1, 2013.67) * mm, "end": v(1235.1, 1861.27) * mm});
            skLineSegment(sketch, "E5.9.8.2", {"start": v(1235.1, 1861.27) * mm, "end": v(1387.5, 1861.27) * mm});
            skLineSegment(sketch, "E5.0.8.3", {"start": v(1387.5, 1842.22) * mm, "end": v(1387.5, 1689.82) * mm});
            skLineSegment(sketch, "E5.3.8.3", {"start": v(1235.1, 1842.22) * mm, "end": v(1387.5, 1842.22) * mm});
            skLineSegment(sketch, "E5.6.8.3", {"start": v(1235.1, 1842.22) * mm, "end": v(1235.1, 1689.82) * mm});
            skLineSegment(sketch, "E5.9.8.3", {"start": v(1235.1, 1689.82) * mm, "end": v(1387.5, 1689.82) * mm});
            skLineSegment(sketch, "E5.0.8.4", {"start": v(1387.5, 1670.77) * mm, "end": v(1387.5, 1518.37) * mm});
            skLineSegment(sketch, "E5.3.8.4", {"start": v(1235.1, 1670.77) * mm, "end": v(1387.5, 1670.77) * mm});
            skLineSegment(sketch, "E5.6.8.4", {"start": v(1235.1, 1670.77) * mm, "end": v(1235.1, 1518.37) * mm});
            skLineSegment(sketch, "E5.9.8.4", {"start": v(1235.1, 1518.37) * mm, "end": v(1387.5, 1518.37) * mm});
            skLineSegment(sketch, "E5.0.8.5", {"start": v(1387.5, 1499.32) * mm, "end": v(1387.5, 1346.92) * mm});
            skLineSegment(sketch, "E5.3.8.5", {"start": v(1235.1, 1499.32) * mm, "end": v(1387.5, 1499.32) * mm});
            skLineSegment(sketch, "E5.6.8.5", {"start": v(1235.1, 1499.32) * mm, "end": v(1235.1, 1346.92) * mm});
            skLineSegment(sketch, "E5.9.8.5", {"start": v(1235.1, 1346.92) * mm, "end": v(1387.5, 1346.92) * mm});
            skLineSegment(sketch, "E5.0.8.6", {"start": v(1387.5, 1327.87) * mm, "end": v(1387.5, 1175.47) * mm});
            skLineSegment(sketch, "E5.3.8.6", {"start": v(1235.1, 1327.87) * mm, "end": v(1387.5, 1327.87) * mm});
            skLineSegment(sketch, "E5.6.8.6", {"start": v(1235.1, 1327.87) * mm, "end": v(1235.1, 1175.47) * mm});
            skLineSegment(sketch, "E5.9.8.6", {"start": v(1235.1, 1175.47) * mm, "end": v(1387.5, 1175.47) * mm});
            skLineSegment(sketch, "E5.0.8.7", {"start": v(1387.5, 1156.42) * mm, "end": v(1387.5, 1004.02) * mm});
            skLineSegment(sketch, "E5.3.8.7", {"start": v(1235.1, 1156.42) * mm, "end": v(1387.5, 1156.42) * mm});
            skLineSegment(sketch, "E5.6.8.7", {"start": v(1235.1, 1156.42) * mm, "end": v(1235.1, 1004.02) * mm});
            skLineSegment(sketch, "E5.9.8.7", {"start": v(1235.1, 1004.02) * mm, "end": v(1387.5, 1004.02) * mm});
            skLineSegment(sketch, "E5.0.8.8", {"start": v(1387.5, 984.97) * mm, "end": v(1387.5, 832.57) * mm});
            skLineSegment(sketch, "E5.3.8.8", {"start": v(1235.1, 984.97) * mm, "end": v(1387.5, 984.97) * mm});
            skLineSegment(sketch, "E5.6.8.8", {"start": v(1235.1, 984.97) * mm, "end": v(1235.1, 832.57) * mm});
            skLineSegment(sketch, "E5.9.8.8", {"start": v(1235.1, 832.57) * mm, "end": v(1387.5, 832.57) * mm});
            skLineSegment(sketch, "E5.0.9.0", {"start": v(1552.6, 2356.57) * mm, "end": v(1552.6, 2204.17) * mm});
            skLineSegment(sketch, "E5.3.9.0", {"start": v(1400.2, 2356.57) * mm, "end": v(1552.6, 2356.57) * mm});
            skLineSegment(sketch, "E5.6.9.0", {"start": v(1400.2, 2356.57) * mm, "end": v(1400.2, 2204.17) * mm});
            skLineSegment(sketch, "E5.9.9.0", {"start": v(1400.2, 2204.17) * mm, "end": v(1552.6, 2204.17) * mm});
            skLineSegment(sketch, "E5.0.9.1", {"start": v(1552.6, 2185.12) * mm, "end": v(1552.6, 2032.72) * mm});
            skLineSegment(sketch, "E5.3.9.1", {"start": v(1400.2, 2185.12) * mm, "end": v(1552.6, 2185.12) * mm});
            skLineSegment(sketch, "E5.6.9.1", {"start": v(1400.2, 2185.12) * mm, "end": v(1400.2, 2032.72) * mm});
            skLineSegment(sketch, "E5.9.9.1", {"start": v(1400.2, 2032.72) * mm, "end": v(1552.6, 2032.72) * mm});
            skLineSegment(sketch, "E5.0.9.2", {"start": v(1552.6, 2013.67) * mm, "end": v(1552.6, 1861.27) * mm});
            skLineSegment(sketch, "E5.3.9.2", {"start": v(1400.2, 2013.67) * mm, "end": v(1552.6, 2013.67) * mm});
            skLineSegment(sketch, "E5.6.9.2", {"start": v(1400.2, 2013.67) * mm, "end": v(1400.2, 1861.27) * mm});
            skLineSegment(sketch, "E5.9.9.2", {"start": v(1400.2, 1861.27) * mm, "end": v(1552.6, 1861.27) * mm});
            skLineSegment(sketch, "E5.0.9.3", {"start": v(1552.6, 1842.22) * mm, "end": v(1552.6, 1689.82) * mm});
            skLineSegment(sketch, "E5.3.9.3", {"start": v(1400.2, 1842.22) * mm, "end": v(1552.6, 1842.22) * mm});
            skLineSegment(sketch, "E5.6.9.3", {"start": v(1400.2, 1842.22) * mm, "end": v(1400.2, 1689.82) * mm});
            skLineSegment(sketch, "E5.9.9.3", {"start": v(1400.2, 1689.82) * mm, "end": v(1552.6, 1689.82) * mm});
            skLineSegment(sketch, "E5.0.9.4", {"start": v(1552.6, 1670.77) * mm, "end": v(1552.6, 1518.37) * mm});
            skLineSegment(sketch, "E5.3.9.4", {"start": v(1400.2, 1670.77) * mm, "end": v(1552.6, 1670.77) * mm});
            skLineSegment(sketch, "E5.6.9.4", {"start": v(1400.2, 1670.77) * mm, "end": v(1400.2, 1518.37) * mm});
            skLineSegment(sketch, "E5.9.9.4", {"start": v(1400.2, 1518.37) * mm, "end": v(1552.6, 1518.37) * mm});
            skLineSegment(sketch, "E5.0.9.5", {"start": v(1552.6, 1499.32) * mm, "end": v(1552.6, 1346.92) * mm});
            skLineSegment(sketch, "E5.3.9.5", {"start": v(1400.2, 1499.32) * mm, "end": v(1552.6, 1499.32) * mm});
            skLineSegment(sketch, "E5.6.9.5", {"start": v(1400.2, 1499.32) * mm, "end": v(1400.2, 1346.92) * mm});
            skLineSegment(sketch, "E5.9.9.5", {"start": v(1400.2, 1346.92) * mm, "end": v(1552.6, 1346.92) * mm});
            skLineSegment(sketch, "E5.0.9.6", {"start": v(1552.6, 1327.87) * mm, "end": v(1552.6, 1175.47) * mm});
            skLineSegment(sketch, "E5.3.9.6", {"start": v(1400.2, 1327.87) * mm, "end": v(1552.6, 1327.87) * mm});
            skLineSegment(sketch, "E5.6.9.6", {"start": v(1400.2, 1327.87) * mm, "end": v(1400.2, 1175.47) * mm});
            skLineSegment(sketch, "E5.9.9.6", {"start": v(1400.2, 1175.47) * mm, "end": v(1552.6, 1175.47) * mm});
            skLineSegment(sketch, "E5.0.9.7", {"start": v(1552.6, 1156.42) * mm, "end": v(1552.6, 1004.02) * mm});
            skLineSegment(sketch, "E5.3.9.7", {"start": v(1400.2, 1156.42) * mm, "end": v(1552.6, 1156.42) * mm});
            skLineSegment(sketch, "E5.6.9.7", {"start": v(1400.2, 1156.42) * mm, "end": v(1400.2, 1004.02) * mm});
            skLineSegment(sketch, "E5.9.9.7", {"start": v(1400.2, 1004.02) * mm, "end": v(1552.6, 1004.02) * mm});
            skLineSegment(sketch, "E5.0.9.8", {"start": v(1552.6, 984.97) * mm, "end": v(1552.6, 832.57) * mm});
            skLineSegment(sketch, "E5.3.9.8", {"start": v(1400.2, 984.97) * mm, "end": v(1552.6, 984.97) * mm});
            skLineSegment(sketch, "E5.6.9.8", {"start": v(1400.2, 984.97) * mm, "end": v(1400.2, 832.57) * mm});
            skLineSegment(sketch, "E5.9.9.8", {"start": v(1400.2, 832.57) * mm, "end": v(1552.6, 832.57) * mm});
            skLineSegment(sketch, "E5.0.10.0", {"start": v(1717.7, 2356.57) * mm, "end": v(1717.7, 2204.17) * mm});
            skLineSegment(sketch, "E5.3.10.0", {"start": v(1565.3, 2356.57) * mm, "end": v(1717.7, 2356.57) * mm});
            skLineSegment(sketch, "E5.6.10.0", {"start": v(1565.3, 2356.57) * mm, "end": v(1565.3, 2204.17) * mm});
            skLineSegment(sketch, "E5.9.10.0", {"start": v(1565.3, 2204.17) * mm, "end": v(1717.7, 2204.17) * mm});
            skLineSegment(sketch, "E5.0.10.1", {"start": v(1717.7, 2185.12) * mm, "end": v(1717.7, 2032.72) * mm});
            skLineSegment(sketch, "E5.3.10.1", {"start": v(1565.3, 2185.12) * mm, "end": v(1717.7, 2185.12) * mm});
            skLineSegment(sketch, "E5.6.10.1", {"start": v(1565.3, 2185.12) * mm, "end": v(1565.3, 2032.72) * mm});
            skLineSegment(sketch, "E5.9.10.1", {"start": v(1565.3, 2032.72) * mm, "end": v(1717.7, 2032.72) * mm});
            skLineSegment(sketch, "E5.0.10.2", {"start": v(1717.7, 2013.67) * mm, "end": v(1717.7, 1861.27) * mm});
            skLineSegment(sketch, "E5.3.10.2", {"start": v(1565.3, 2013.67) * mm, "end": v(1717.7, 2013.67) * mm});
            skLineSegment(sketch, "E5.6.10.2", {"start": v(1565.3, 2013.67) * mm, "end": v(1565.3, 1861.27) * mm});
            skLineSegment(sketch, "E5.9.10.2", {"start": v(1565.3, 1861.27) * mm, "end": v(1717.7, 1861.27) * mm});
            skLineSegment(sketch, "E5.0.10.3", {"start": v(1717.7, 1842.22) * mm, "end": v(1717.7, 1689.82) * mm});
            skLineSegment(sketch, "E5.3.10.3", {"start": v(1565.3, 1842.22) * mm, "end": v(1717.7, 1842.22) * mm});
            skLineSegment(sketch, "E5.6.10.3", {"start": v(1565.3, 1842.22) * mm, "end": v(1565.3, 1689.82) * mm});
            skLineSegment(sketch, "E5.9.10.3", {"start": v(1565.3, 1689.82) * mm, "end": v(1717.7, 1689.82) * mm});
            skLineSegment(sketch, "E5.0.10.4", {"start": v(1717.7, 1670.77) * mm, "end": v(1717.7, 1518.37) * mm});
            skLineSegment(sketch, "E5.3.10.4", {"start": v(1565.3, 1670.77) * mm, "end": v(1717.7, 1670.77) * mm});
            skLineSegment(sketch, "E5.6.10.4", {"start": v(1565.3, 1670.77) * mm, "end": v(1565.3, 1518.37) * mm});
            skLineSegment(sketch, "E5.9.10.4", {"start": v(1565.3, 1518.37) * mm, "end": v(1717.7, 1518.37) * mm});
            skLineSegment(sketch, "E5.0.10.5", {"start": v(1717.7, 1499.32) * mm, "end": v(1717.7, 1346.92) * mm});
            skLineSegment(sketch, "E5.3.10.5", {"start": v(1565.3, 1499.32) * mm, "end": v(1717.7, 1499.32) * mm});
            skLineSegment(sketch, "E5.6.10.5", {"start": v(1565.3, 1499.32) * mm, "end": v(1565.3, 1346.92) * mm});
            skLineSegment(sketch, "E5.9.10.5", {"start": v(1565.3, 1346.92) * mm, "end": v(1717.7, 1346.92) * mm});
            skLineSegment(sketch, "E5.0.10.6", {"start": v(1717.7, 1327.87) * mm, "end": v(1717.7, 1175.47) * mm});
            skLineSegment(sketch, "E5.3.10.6", {"start": v(1565.3, 1327.87) * mm, "end": v(1717.7, 1327.87) * mm});
            skLineSegment(sketch, "E5.6.10.6", {"start": v(1565.3, 1327.87) * mm, "end": v(1565.3, 1175.47) * mm});
            skLineSegment(sketch, "E5.9.10.6", {"start": v(1565.3, 1175.47) * mm, "end": v(1717.7, 1175.47) * mm});
            skLineSegment(sketch, "E5.0.10.7", {"start": v(1717.7, 1156.42) * mm, "end": v(1717.7, 1004.02) * mm});
            skLineSegment(sketch, "E5.3.10.7", {"start": v(1565.3, 1156.42) * mm, "end": v(1717.7, 1156.42) * mm});
            skLineSegment(sketch, "E5.6.10.7", {"start": v(1565.3, 1156.42) * mm, "end": v(1565.3, 1004.02) * mm});
            skLineSegment(sketch, "E5.9.10.7", {"start": v(1565.3, 1004.02) * mm, "end": v(1717.7, 1004.02) * mm});
            skLineSegment(sketch, "E5.0.10.8", {"start": v(1717.7, 984.97) * mm, "end": v(1717.7, 832.57) * mm});
            skLineSegment(sketch, "E5.3.10.8", {"start": v(1565.3, 984.97) * mm, "end": v(1717.7, 984.97) * mm});
            skLineSegment(sketch, "E5.6.10.8", {"start": v(1565.3, 984.97) * mm, "end": v(1565.3, 832.57) * mm});
            skLineSegment(sketch, "E5.9.10.8", {"start": v(1565.3, 832.57) * mm, "end": v(1717.7, 832.57) * mm});
            skLineSegment(sketch, "E6.0.0.9", {"start": v(66.7, 813.52) * mm, "end": v(66.7, 661.12) * mm});
            skLineSegment(sketch, "E6.3.0.9", {"start": v(-85.7, 813.52) * mm, "end": v(66.7, 813.52) * mm});
            skLineSegment(sketch, "E6.6.0.9", {"start": v(-85.7, 813.52) * mm, "end": v(-85.7, 661.12) * mm});
            skLineSegment(sketch, "E6.9.0.9", {"start": v(-85.7, 661.12) * mm, "end": v(66.7, 661.12) * mm});
            skLineSegment(sketch, "E6.0.0.10", {"start": v(66.7, 642.07) * mm, "end": v(66.7, 489.67) * mm});
            skLineSegment(sketch, "E6.3.0.10", {"start": v(-85.7, 642.07) * mm, "end": v(66.7, 642.07) * mm});
            skLineSegment(sketch, "E6.6.0.10", {"start": v(-85.7, 642.07) * mm, "end": v(-85.7, 489.67) * mm});
            skLineSegment(sketch, "E6.9.0.10", {"start": v(-85.7, 489.67) * mm, "end": v(66.7, 489.67) * mm});
            skLineSegment(sketch, "E6.0.0.11", {"start": v(66.7, 470.62) * mm, "end": v(66.7, 318.22) * mm});
            skLineSegment(sketch, "E6.3.0.11", {"start": v(-85.7, 470.62) * mm, "end": v(66.7, 470.62) * mm});
            skLineSegment(sketch, "E6.6.0.11", {"start": v(-85.7, 470.62) * mm, "end": v(-85.7, 318.22) * mm});
            skLineSegment(sketch, "E6.9.0.11", {"start": v(-85.7, 318.22) * mm, "end": v(66.7, 318.22) * mm});
            skLineSegment(sketch, "E6.0.0.12", {"start": v(66.7, 299.17) * mm, "end": v(66.7, 146.77) * mm});
            skLineSegment(sketch, "E6.3.0.12", {"start": v(-85.7, 299.17) * mm, "end": v(66.7, 299.17) * mm});
            skLineSegment(sketch, "E6.6.0.12", {"start": v(-85.7, 299.17) * mm, "end": v(-85.7, 146.77) * mm});
            skLineSegment(sketch, "E6.9.0.12", {"start": v(-85.7, 146.77) * mm, "end": v(66.7, 146.77) * mm});
            skLineSegment(sketch, "E6.0.0.13", {"start": v(66.7, 127.72) * mm, "end": v(66.7, -24.68) * mm});
            skLineSegment(sketch, "E6.3.0.13", {"start": v(-85.7, 127.72) * mm, "end": v(66.7, 127.72) * mm});
            skLineSegment(sketch, "E6.6.0.13", {"start": v(-85.7, 127.72) * mm, "end": v(-85.7, -24.68) * mm});
            skLineSegment(sketch, "E6.9.0.13", {"start": v(-85.7, -24.68) * mm, "end": v(66.7, -24.68) * mm});
            skLineSegment(sketch, "E6.0.1.9", {"start": v(231.8, 813.52) * mm, "end": v(231.8, 661.12) * mm});
            skLineSegment(sketch, "E6.3.1.9", {"start": v(79.4, 813.52) * mm, "end": v(231.8, 813.52) * mm});
            skLineSegment(sketch, "E6.6.1.9", {"start": v(79.4, 813.52) * mm, "end": v(79.4, 661.12) * mm});
            skLineSegment(sketch, "E6.9.1.9", {"start": v(79.4, 661.12) * mm, "end": v(231.8, 661.12) * mm});
            skLineSegment(sketch, "E6.0.1.10", {"start": v(231.8, 642.07) * mm, "end": v(231.8, 489.67) * mm});
            skLineSegment(sketch, "E6.3.1.10", {"start": v(79.4, 642.07) * mm, "end": v(231.8, 642.07) * mm});
            skLineSegment(sketch, "E6.6.1.10", {"start": v(79.4, 642.07) * mm, "end": v(79.4, 489.67) * mm});
            skLineSegment(sketch, "E6.9.1.10", {"start": v(79.4, 489.67) * mm, "end": v(231.8, 489.67) * mm});
            skLineSegment(sketch, "E6.0.1.11", {"start": v(231.8, 470.62) * mm, "end": v(231.8, 318.22) * mm});
            skLineSegment(sketch, "E6.3.1.11", {"start": v(79.4, 470.62) * mm, "end": v(231.8, 470.62) * mm});
            skLineSegment(sketch, "E6.6.1.11", {"start": v(79.4, 470.62) * mm, "end": v(79.4, 318.22) * mm});
            skLineSegment(sketch, "E6.9.1.11", {"start": v(79.4, 318.22) * mm, "end": v(231.8, 318.22) * mm});
            skLineSegment(sketch, "E6.0.1.12", {"start": v(231.8, 299.17) * mm, "end": v(231.8, 146.77) * mm});
            skLineSegment(sketch, "E6.3.1.12", {"start": v(79.4, 299.17) * mm, "end": v(231.8, 299.17) * mm});
            skLineSegment(sketch, "E6.6.1.12", {"start": v(79.4, 299.17) * mm, "end": v(79.4, 146.77) * mm});
            skLineSegment(sketch, "E6.9.1.12", {"start": v(79.4, 146.77) * mm, "end": v(231.8, 146.77) * mm});
            skLineSegment(sketch, "E6.0.1.13", {"start": v(231.8, 127.72) * mm, "end": v(231.8, -24.68) * mm});
            skLineSegment(sketch, "E6.3.1.13", {"start": v(79.4, 127.72) * mm, "end": v(231.8, 127.72) * mm});
            skLineSegment(sketch, "E6.6.1.13", {"start": v(79.4, 127.72) * mm, "end": v(79.4, -24.68) * mm});
            skLineSegment(sketch, "E6.9.1.13", {"start": v(79.4, -24.68) * mm, "end": v(231.8, -24.68) * mm});
            skLineSegment(sketch, "E6.0.2.9", {"start": v(396.9, 813.52) * mm, "end": v(396.9, 661.12) * mm});
            skLineSegment(sketch, "E6.3.2.9", {"start": v(244.5, 813.52) * mm, "end": v(396.9, 813.52) * mm});
            skLineSegment(sketch, "E6.6.2.9", {"start": v(244.5, 813.52) * mm, "end": v(244.5, 661.12) * mm});
            skLineSegment(sketch, "E6.9.2.9", {"start": v(244.5, 661.12) * mm, "end": v(396.9, 661.12) * mm});
            skLineSegment(sketch, "E6.0.2.10", {"start": v(396.9, 642.07) * mm, "end": v(396.9, 489.67) * mm});
            skLineSegment(sketch, "E6.3.2.10", {"start": v(244.5, 642.07) * mm, "end": v(396.9, 642.07) * mm});
            skLineSegment(sketch, "E6.6.2.10", {"start": v(244.5, 642.07) * mm, "end": v(244.5, 489.67) * mm});
            skLineSegment(sketch, "E6.9.2.10", {"start": v(244.5, 489.67) * mm, "end": v(396.9, 489.67) * mm});
            skLineSegment(sketch, "E6.0.2.11", {"start": v(396.9, 470.62) * mm, "end": v(396.9, 318.22) * mm});
            skLineSegment(sketch, "E6.3.2.11", {"start": v(244.5, 470.62) * mm, "end": v(396.9, 470.62) * mm});
            skLineSegment(sketch, "E6.6.2.11", {"start": v(244.5, 470.62) * mm, "end": v(244.5, 318.22) * mm});
            skLineSegment(sketch, "E6.9.2.11", {"start": v(244.5, 318.22) * mm, "end": v(396.9, 318.22) * mm});
            skLineSegment(sketch, "E6.0.2.12", {"start": v(396.9, 299.17) * mm, "end": v(396.9, 146.77) * mm});
            skLineSegment(sketch, "E6.3.2.12", {"start": v(244.5, 299.17) * mm, "end": v(396.9, 299.17) * mm});
            skLineSegment(sketch, "E6.6.2.12", {"start": v(244.5, 299.17) * mm, "end": v(244.5, 146.77) * mm});
            skLineSegment(sketch, "E6.9.2.12", {"start": v(244.5, 146.77) * mm, "end": v(396.9, 146.77) * mm});
            skLineSegment(sketch, "E6.0.2.13", {"start": v(396.9, 127.72) * mm, "end": v(396.9, -24.68) * mm});
            skLineSegment(sketch, "E6.3.2.13", {"start": v(244.5, 127.72) * mm, "end": v(396.9, 127.72) * mm});
            skLineSegment(sketch, "E6.6.2.13", {"start": v(244.5, 127.72) * mm, "end": v(244.5, -24.68) * mm});
            skLineSegment(sketch, "E6.9.2.13", {"start": v(244.5, -24.68) * mm, "end": v(396.9, -24.68) * mm});
            skLineSegment(sketch, "E6.0.3.9", {"start": v(562, 813.52) * mm, "end": v(562, 661.12) * mm});
            skLineSegment(sketch, "E6.3.3.9", {"start": v(409.6, 813.52) * mm, "end": v(562, 813.52) * mm});
            skLineSegment(sketch, "E6.6.3.9", {"start": v(409.6, 813.52) * mm, "end": v(409.6, 661.12) * mm});
            skLineSegment(sketch, "E6.9.3.9", {"start": v(409.6, 661.12) * mm, "end": v(562, 661.12) * mm});
            skLineSegment(sketch, "E6.0.3.10", {"start": v(562, 642.07) * mm, "end": v(562, 489.67) * mm});
            skLineSegment(sketch, "E6.3.3.10", {"start": v(409.6, 642.07) * mm, "end": v(562, 642.07) * mm});
            skLineSegment(sketch, "E6.6.3.10", {"start": v(409.6, 642.07) * mm, "end": v(409.6, 489.67) * mm});
            skLineSegment(sketch, "E6.9.3.10", {"start": v(409.6, 489.67) * mm, "end": v(562, 489.67) * mm});
            skLineSegment(sketch, "E6.0.3.11", {"start": v(562, 470.62) * mm, "end": v(562, 318.22) * mm});
            skLineSegment(sketch, "E6.3.3.11", {"start": v(409.6, 470.62) * mm, "end": v(562, 470.62) * mm});
            skLineSegment(sketch, "E6.6.3.11", {"start": v(409.6, 470.62) * mm, "end": v(409.6, 318.22) * mm});
            skLineSegment(sketch, "E6.9.3.11", {"start": v(409.6, 318.22) * mm, "end": v(562, 318.22) * mm});
            skLineSegment(sketch, "E6.0.3.12", {"start": v(562, 299.17) * mm, "end": v(562, 146.77) * mm});
            skLineSegment(sketch, "E6.3.3.12", {"start": v(409.6, 299.17) * mm, "end": v(562, 299.17) * mm});
            skLineSegment(sketch, "E6.6.3.12", {"start": v(409.6, 299.17) * mm, "end": v(409.6, 146.77) * mm});
            skLineSegment(sketch, "E6.9.3.12", {"start": v(409.6, 146.77) * mm, "end": v(562, 146.77) * mm});
            skLineSegment(sketch, "E6.0.3.13", {"start": v(562, 127.72) * mm, "end": v(562, -24.68) * mm});
            skLineSegment(sketch, "E6.3.3.13", {"start": v(409.6, 127.72) * mm, "end": v(562, 127.72) * mm});
            skLineSegment(sketch, "E6.6.3.13", {"start": v(409.6, 127.72) * mm, "end": v(409.6, -24.68) * mm});
            skLineSegment(sketch, "E6.9.3.13", {"start": v(409.6, -24.68) * mm, "end": v(562, -24.68) * mm});
            skLineSegment(sketch, "E6.0.4.9", {"start": v(727.1, 813.52) * mm, "end": v(727.1, 661.12) * mm});
            skLineSegment(sketch, "E6.3.4.9", {"start": v(574.7, 813.52) * mm, "end": v(727.1, 813.52) * mm});
            skLineSegment(sketch, "E6.6.4.9", {"start": v(574.7, 813.52) * mm, "end": v(574.7, 661.12) * mm});
            skLineSegment(sketch, "E6.9.4.9", {"start": v(574.7, 661.12) * mm, "end": v(727.1, 661.12) * mm});
            skLineSegment(sketch, "E6.0.4.10", {"start": v(727.1, 642.07) * mm, "end": v(727.1, 489.67) * mm});
            skLineSegment(sketch, "E6.3.4.10", {"start": v(574.7, 642.07) * mm, "end": v(727.1, 642.07) * mm});
            skLineSegment(sketch, "E6.6.4.10", {"start": v(574.7, 642.07) * mm, "end": v(574.7, 489.67) * mm});
            skLineSegment(sketch, "E6.9.4.10", {"start": v(574.7, 489.67) * mm, "end": v(727.1, 489.67) * mm});
            skLineSegment(sketch, "E6.0.4.11", {"start": v(727.1, 470.62) * mm, "end": v(727.1, 318.22) * mm});
            skLineSegment(sketch, "E6.3.4.11", {"start": v(574.7, 470.62) * mm, "end": v(727.1, 470.62) * mm});
            skLineSegment(sketch, "E6.6.4.11", {"start": v(574.7, 470.62) * mm, "end": v(574.7, 318.22) * mm});
            skLineSegment(sketch, "E6.9.4.11", {"start": v(574.7, 318.22) * mm, "end": v(727.1, 318.22) * mm});
            skLineSegment(sketch, "E6.0.4.12", {"start": v(727.1, 299.17) * mm, "end": v(727.1, 146.77) * mm});
            skLineSegment(sketch, "E6.3.4.12", {"start": v(574.7, 299.17) * mm, "end": v(727.1, 299.17) * mm});
            skLineSegment(sketch, "E6.6.4.12", {"start": v(574.7, 299.17) * mm, "end": v(574.7, 146.77) * mm});
            skLineSegment(sketch, "E6.9.4.12", {"start": v(574.7, 146.77) * mm, "end": v(727.1, 146.77) * mm});
            skLineSegment(sketch, "E6.0.4.13", {"start": v(727.1, 127.72) * mm, "end": v(727.1, -24.68) * mm});
            skLineSegment(sketch, "E6.3.4.13", {"start": v(574.7, 127.72) * mm, "end": v(727.1, 127.72) * mm});
            skLineSegment(sketch, "E6.6.4.13", {"start": v(574.7, 127.72) * mm, "end": v(574.7, -24.68) * mm});
            skLineSegment(sketch, "E6.9.4.13", {"start": v(574.7, -24.68) * mm, "end": v(727.1, -24.68) * mm});
            skLineSegment(sketch, "E6.0.5.9", {"start": v(892.2, 813.52) * mm, "end": v(892.2, 661.12) * mm});
            skLineSegment(sketch, "E6.3.5.9", {"start": v(739.8, 813.52) * mm, "end": v(892.2, 813.52) * mm});
            skLineSegment(sketch, "E6.6.5.9", {"start": v(739.8, 813.52) * mm, "end": v(739.8, 661.12) * mm});
            skLineSegment(sketch, "E6.9.5.9", {"start": v(739.8, 661.12) * mm, "end": v(892.2, 661.12) * mm});
            skLineSegment(sketch, "E6.0.5.10", {"start": v(892.2, 642.07) * mm, "end": v(892.2, 489.67) * mm});
            skLineSegment(sketch, "E6.3.5.10", {"start": v(739.8, 642.07) * mm, "end": v(892.2, 642.07) * mm});
            skLineSegment(sketch, "E6.6.5.10", {"start": v(739.8, 642.07) * mm, "end": v(739.8, 489.67) * mm});
            skLineSegment(sketch, "E6.9.5.10", {"start": v(739.8, 489.67) * mm, "end": v(892.2, 489.67) * mm});
            skLineSegment(sketch, "E6.0.5.11", {"start": v(892.2, 470.62) * mm, "end": v(892.2, 318.22) * mm});
            skLineSegment(sketch, "E6.3.5.11", {"start": v(739.8, 470.62) * mm, "end": v(892.2, 470.62) * mm});
            skLineSegment(sketch, "E6.6.5.11", {"start": v(739.8, 470.62) * mm, "end": v(739.8, 318.22) * mm});
            skLineSegment(sketch, "E6.9.5.11", {"start": v(739.8, 318.22) * mm, "end": v(892.2, 318.22) * mm});
            skLineSegment(sketch, "E6.0.5.12", {"start": v(892.2, 299.17) * mm, "end": v(892.2, 146.77) * mm});
            skLineSegment(sketch, "E6.3.5.12", {"start": v(739.8, 299.17) * mm, "end": v(892.2, 299.17) * mm});
            skLineSegment(sketch, "E6.6.5.12", {"start": v(739.8, 299.17) * mm, "end": v(739.8, 146.77) * mm});
            skLineSegment(sketch, "E6.9.5.12", {"start": v(739.8, 146.77) * mm, "end": v(892.2, 146.77) * mm});
            skLineSegment(sketch, "E6.0.5.13", {"start": v(892.2, 127.72) * mm, "end": v(892.2, -24.68) * mm});
            skLineSegment(sketch, "E6.3.5.13", {"start": v(739.8, 127.72) * mm, "end": v(892.2, 127.72) * mm});
            skLineSegment(sketch, "E6.6.5.13", {"start": v(739.8, 127.72) * mm, "end": v(739.8, -24.68) * mm});
            skLineSegment(sketch, "E6.9.5.13", {"start": v(739.8, -24.68) * mm, "end": v(892.2, -24.68) * mm});
            skLineSegment(sketch, "E6.0.6.9", {"start": v(1057.3, 813.52) * mm, "end": v(1057.3, 661.12) * mm});
            skLineSegment(sketch, "E6.3.6.9", {"start": v(904.9, 813.52) * mm, "end": v(1057.3, 813.52) * mm});
            skLineSegment(sketch, "E6.6.6.9", {"start": v(904.9, 813.52) * mm, "end": v(904.9, 661.12) * mm});
            skLineSegment(sketch, "E6.9.6.9", {"start": v(904.9, 661.12) * mm, "end": v(1057.3, 661.12) * mm});
            skLineSegment(sketch, "E6.0.6.10", {"start": v(1057.3, 642.07) * mm, "end": v(1057.3, 489.67) * mm});
            skLineSegment(sketch, "E6.3.6.10", {"start": v(904.9, 642.07) * mm, "end": v(1057.3, 642.07) * mm});
            skLineSegment(sketch, "E6.6.6.10", {"start": v(904.9, 642.07) * mm, "end": v(904.9, 489.67) * mm});
            skLineSegment(sketch, "E6.9.6.10", {"start": v(904.9, 489.67) * mm, "end": v(1057.3, 489.67) * mm});
            skLineSegment(sketch, "E6.0.6.11", {"start": v(1057.3, 470.62) * mm, "end": v(1057.3, 318.22) * mm});
            skLineSegment(sketch, "E6.3.6.11", {"start": v(904.9, 470.62) * mm, "end": v(1057.3, 470.62) * mm});
            skLineSegment(sketch, "E6.6.6.11", {"start": v(904.9, 470.62) * mm, "end": v(904.9, 318.22) * mm});
            skLineSegment(sketch, "E6.9.6.11", {"start": v(904.9, 318.22) * mm, "end": v(1057.3, 318.22) * mm});
            skLineSegment(sketch, "E6.0.6.12", {"start": v(1057.3, 299.17) * mm, "end": v(1057.3, 146.77) * mm});
            skLineSegment(sketch, "E6.3.6.12", {"start": v(904.9, 299.17) * mm, "end": v(1057.3, 299.17) * mm});
            skLineSegment(sketch, "E6.6.6.12", {"start": v(904.9, 299.17) * mm, "end": v(904.9, 146.77) * mm});
            skLineSegment(sketch, "E6.9.6.12", {"start": v(904.9, 146.77) * mm, "end": v(1057.3, 146.77) * mm});
            skLineSegment(sketch, "E6.0.6.13", {"start": v(1057.3, 127.72) * mm, "end": v(1057.3, -24.68) * mm});
            skLineSegment(sketch, "E6.3.6.13", {"start": v(904.9, 127.72) * mm, "end": v(1057.3, 127.72) * mm});
            skLineSegment(sketch, "E6.6.6.13", {"start": v(904.9, 127.72) * mm, "end": v(904.9, -24.68) * mm});
            skLineSegment(sketch, "E6.9.6.13", {"start": v(904.9, -24.68) * mm, "end": v(1057.3, -24.68) * mm});
            skLineSegment(sketch, "E6.0.7.9", {"start": v(1222.4, 813.52) * mm, "end": v(1222.4, 661.12) * mm});
            skLineSegment(sketch, "E6.3.7.9", {"start": v(1070, 813.52) * mm, "end": v(1222.4, 813.52) * mm});
            skLineSegment(sketch, "E6.6.7.9", {"start": v(1070, 813.52) * mm, "end": v(1070, 661.12) * mm});
            skLineSegment(sketch, "E6.9.7.9", {"start": v(1070, 661.12) * mm, "end": v(1222.4, 661.12) * mm});
            skLineSegment(sketch, "E6.0.7.10", {"start": v(1222.4, 642.07) * mm, "end": v(1222.4, 489.67) * mm});
            skLineSegment(sketch, "E6.3.7.10", {"start": v(1070, 642.07) * mm, "end": v(1222.4, 642.07) * mm});
            skLineSegment(sketch, "E6.6.7.10", {"start": v(1070, 642.07) * mm, "end": v(1070, 489.67) * mm});
            skLineSegment(sketch, "E6.9.7.10", {"start": v(1070, 489.67) * mm, "end": v(1222.4, 489.67) * mm});
            skLineSegment(sketch, "E6.0.7.11", {"start": v(1222.4, 470.62) * mm, "end": v(1222.4, 318.22) * mm});
            skLineSegment(sketch, "E6.3.7.11", {"start": v(1070, 470.62) * mm, "end": v(1222.4, 470.62) * mm});
            skLineSegment(sketch, "E6.6.7.11", {"start": v(1070, 470.62) * mm, "end": v(1070, 318.22) * mm});
            skLineSegment(sketch, "E6.9.7.11", {"start": v(1070, 318.22) * mm, "end": v(1222.4, 318.22) * mm});
            skLineSegment(sketch, "E6.0.7.12", {"start": v(1222.4, 299.17) * mm, "end": v(1222.4, 146.77) * mm});
            skLineSegment(sketch, "E6.3.7.12", {"start": v(1070, 299.17) * mm, "end": v(1222.4, 299.17) * mm});
            skLineSegment(sketch, "E6.6.7.12", {"start": v(1070, 299.17) * mm, "end": v(1070, 146.77) * mm});
            skLineSegment(sketch, "E6.9.7.12", {"start": v(1070, 146.77) * mm, "end": v(1222.4, 146.77) * mm});
            skLineSegment(sketch, "E6.0.7.13", {"start": v(1222.4, 127.72) * mm, "end": v(1222.4, -24.68) * mm});
            skLineSegment(sketch, "E6.3.7.13", {"start": v(1070, 127.72) * mm, "end": v(1222.4, 127.72) * mm});
            skLineSegment(sketch, "E6.6.7.13", {"start": v(1070, 127.72) * mm, "end": v(1070, -24.68) * mm});
            skLineSegment(sketch, "E6.9.7.13", {"start": v(1070, -24.68) * mm, "end": v(1222.4, -24.68) * mm});
            skLineSegment(sketch, "E6.0.8.9", {"start": v(1387.5, 813.52) * mm, "end": v(1387.5, 661.12) * mm});
            skLineSegment(sketch, "E6.3.8.9", {"start": v(1235.1, 813.52) * mm, "end": v(1387.5, 813.52) * mm});
            skLineSegment(sketch, "E6.6.8.9", {"start": v(1235.1, 813.52) * mm, "end": v(1235.1, 661.12) * mm});
            skLineSegment(sketch, "E6.9.8.9", {"start": v(1235.1, 661.12) * mm, "end": v(1387.5, 661.12) * mm});
            skLineSegment(sketch, "E6.0.8.10", {"start": v(1387.5, 642.07) * mm, "end": v(1387.5, 489.67) * mm});
            skLineSegment(sketch, "E6.3.8.10", {"start": v(1235.1, 642.07) * mm, "end": v(1387.5, 642.07) * mm});
            skLineSegment(sketch, "E6.6.8.10", {"start": v(1235.1, 642.07) * mm, "end": v(1235.1, 489.67) * mm});
            skLineSegment(sketch, "E6.9.8.10", {"start": v(1235.1, 489.67) * mm, "end": v(1387.5, 489.67) * mm});
            skLineSegment(sketch, "E6.0.8.11", {"start": v(1387.5, 470.62) * mm, "end": v(1387.5, 318.22) * mm});
            skLineSegment(sketch, "E6.3.8.11", {"start": v(1235.1, 470.62) * mm, "end": v(1387.5, 470.62) * mm});
            skLineSegment(sketch, "E6.6.8.11", {"start": v(1235.1, 470.62) * mm, "end": v(1235.1, 318.22) * mm});
            skLineSegment(sketch, "E6.9.8.11", {"start": v(1235.1, 318.22) * mm, "end": v(1387.5, 318.22) * mm});
            skLineSegment(sketch, "E6.0.8.12", {"start": v(1387.5, 299.17) * mm, "end": v(1387.5, 146.77) * mm});
            skLineSegment(sketch, "E6.3.8.12", {"start": v(1235.1, 299.17) * mm, "end": v(1387.5, 299.17) * mm});
            skLineSegment(sketch, "E6.6.8.12", {"start": v(1235.1, 299.17) * mm, "end": v(1235.1, 146.77) * mm});
            skLineSegment(sketch, "E6.9.8.12", {"start": v(1235.1, 146.77) * mm, "end": v(1387.5, 146.77) * mm});
            skLineSegment(sketch, "E6.0.8.13", {"start": v(1387.5, 127.72) * mm, "end": v(1387.5, -24.68) * mm});
            skLineSegment(sketch, "E6.3.8.13", {"start": v(1235.1, 127.72) * mm, "end": v(1387.5, 127.72) * mm});
            skLineSegment(sketch, "E6.6.8.13", {"start": v(1235.1, 127.72) * mm, "end": v(1235.1, -24.68) * mm});
            skLineSegment(sketch, "E6.9.8.13", {"start": v(1235.1, -24.68) * mm, "end": v(1387.5, -24.68) * mm});
            skLineSegment(sketch, "E6.0.9.9", {"start": v(1552.6, 813.52) * mm, "end": v(1552.6, 661.12) * mm});
            skLineSegment(sketch, "E6.3.9.9", {"start": v(1400.2, 813.52) * mm, "end": v(1552.6, 813.52) * mm});
            skLineSegment(sketch, "E6.6.9.9", {"start": v(1400.2, 813.52) * mm, "end": v(1400.2, 661.12) * mm});
            skLineSegment(sketch, "E6.9.9.9", {"start": v(1400.2, 661.12) * mm, "end": v(1552.6, 661.12) * mm});
            skLineSegment(sketch, "E6.0.9.10", {"start": v(1552.6, 642.07) * mm, "end": v(1552.6, 489.67) * mm});
            skLineSegment(sketch, "E6.3.9.10", {"start": v(1400.2, 642.07) * mm, "end": v(1552.6, 642.07) * mm});
            skLineSegment(sketch, "E6.6.9.10", {"start": v(1400.2, 642.07) * mm, "end": v(1400.2, 489.67) * mm});
            skLineSegment(sketch, "E6.9.9.10", {"start": v(1400.2, 489.67) * mm, "end": v(1552.6, 489.67) * mm});
            skLineSegment(sketch, "E6.0.9.11", {"start": v(1552.6, 470.62) * mm, "end": v(1552.6, 318.22) * mm});
            skLineSegment(sketch, "E6.3.9.11", {"start": v(1400.2, 470.62) * mm, "end": v(1552.6, 470.62) * mm});
            skLineSegment(sketch, "E6.6.9.11", {"start": v(1400.2, 470.62) * mm, "end": v(1400.2, 318.22) * mm});
            skLineSegment(sketch, "E6.9.9.11", {"start": v(1400.2, 318.22) * mm, "end": v(1552.6, 318.22) * mm});
            skLineSegment(sketch, "E6.0.9.12", {"start": v(1552.6, 299.17) * mm, "end": v(1552.6, 146.77) * mm});
            skLineSegment(sketch, "E6.3.9.12", {"start": v(1400.2, 299.17) * mm, "end": v(1552.6, 299.17) * mm});
            skLineSegment(sketch, "E6.6.9.12", {"start": v(1400.2, 299.17) * mm, "end": v(1400.2, 146.77) * mm});
            skLineSegment(sketch, "E6.9.9.12", {"start": v(1400.2, 146.77) * mm, "end": v(1552.6, 146.77) * mm});
            skLineSegment(sketch, "E6.0.9.13", {"start": v(1552.6, 127.72) * mm, "end": v(1552.6, -24.68) * mm});
            skLineSegment(sketch, "E6.3.9.13", {"start": v(1400.2, 127.72) * mm, "end": v(1552.6, 127.72) * mm});
            skLineSegment(sketch, "E6.6.9.13", {"start": v(1400.2, 127.72) * mm, "end": v(1400.2, -24.68) * mm});
            skLineSegment(sketch, "E6.9.9.13", {"start": v(1400.2, -24.68) * mm, "end": v(1552.6, -24.68) * mm});
            skLineSegment(sketch, "E6.0.10.9", {"start": v(1717.7, 813.52) * mm, "end": v(1717.7, 661.12) * mm});
            skLineSegment(sketch, "E6.3.10.9", {"start": v(1565.3, 813.52) * mm, "end": v(1717.7, 813.52) * mm});
            skLineSegment(sketch, "E6.6.10.9", {"start": v(1565.3, 813.52) * mm, "end": v(1565.3, 661.12) * mm});
            skLineSegment(sketch, "E6.9.10.9", {"start": v(1565.3, 661.12) * mm, "end": v(1717.7, 661.12) * mm});
            skLineSegment(sketch, "E6.0.10.10", {"start": v(1717.7, 642.07) * mm, "end": v(1717.7, 489.67) * mm});
            skLineSegment(sketch, "E6.3.10.10", {"start": v(1565.3, 642.07) * mm, "end": v(1717.7, 642.07) * mm});
            skLineSegment(sketch, "E6.6.10.10", {"start": v(1565.3, 642.07) * mm, "end": v(1565.3, 489.67) * mm});
            skLineSegment(sketch, "E6.9.10.10", {"start": v(1565.3, 489.67) * mm, "end": v(1717.7, 489.67) * mm});
            skLineSegment(sketch, "E6.0.10.11", {"start": v(1717.7, 470.62) * mm, "end": v(1717.7, 318.22) * mm});
            skLineSegment(sketch, "E6.3.10.11", {"start": v(1565.3, 470.62) * mm, "end": v(1717.7, 470.62) * mm});
            skLineSegment(sketch, "E6.6.10.11", {"start": v(1565.3, 470.62) * mm, "end": v(1565.3, 318.22) * mm});
            skLineSegment(sketch, "E6.9.10.11", {"start": v(1565.3, 318.22) * mm, "end": v(1717.7, 318.22) * mm});
            skLineSegment(sketch, "E6.0.10.12", {"start": v(1717.7, 299.17) * mm, "end": v(1717.7, 146.77) * mm});
            skLineSegment(sketch, "E6.3.10.12", {"start": v(1565.3, 299.17) * mm, "end": v(1717.7, 299.17) * mm});
            skLineSegment(sketch, "E6.6.10.12", {"start": v(1565.3, 299.17) * mm, "end": v(1565.3, 146.77) * mm});
            skLineSegment(sketch, "E6.9.10.12", {"start": v(1565.3, 146.77) * mm, "end": v(1717.7, 146.77) * mm});
            skLineSegment(sketch, "E6.0.10.13", {"start": v(1717.7, 127.72) * mm, "end": v(1717.7, -24.68) * mm});
            skLineSegment(sketch, "E6.3.10.13", {"start": v(1565.3, 127.72) * mm, "end": v(1717.7, 127.72) * mm});
            skLineSegment(sketch, "E6.6.10.13", {"start": v(1565.3, 127.72) * mm, "end": v(1565.3, -24.68) * mm});
            skLineSegment(sketch, "E6.9.10.13", {"start": v(1565.3, -24.68) * mm, "end": v(1717.7, -24.68) * mm});
            skSolve(sketch);
        }
        {
            var Q0;
            Q0 = qSketchRegion(id + "F2", true);
            extrude(context, id + "F3", {"entities" : qUnion([Q0]), "operationType" : NewBodyOperationType.REMOVE, "oppositeDirection" : true, "depth" : .25 / 101.6 * mm});
        }
        {
            var Q0;
            Q0=makeQuery(id+"F1.opExtrude","CAP_FACE",FACE,{"disambiguationData":[OSD([sQuery(id+"F0.wireOp",EDGE,"E0.bottom"),sQuery(id+"F0.wireOp",EDGE,"E0.top"),sQuery(id+"F0.wireOp",EDGE,"E0.left"),sQuery(id+"F0.wireOp",EDGE,"E0.right")])],"isStart":false});
            var sketch = newSketch(context, id + "F4", { "sketchPlane" : qUnion([Q0])});
            skCircle(sketch, "E7.cCircle", {"center": v(73.05, 2194.64) * mm, "radius": 10.8 * mm, "construction": true});
            skLineSegment(sketch, "E7.0", {"start": v(79.28, 2183.85) * mm, "end": v(66.82, 2183.85) * mm});
            skLineSegment(sketch, "E7.1", {"start": v(66.82, 2183.85) * mm, "end": v(60.6, 2194.64) * mm});
            skLineSegment(sketch, "E7.2", {"start": v(60.6, 2194.64) * mm, "end": v(66.82, 2205.43) * mm});
            skLineSegment(sketch, "E7.3", {"start": v(66.82, 2205.43) * mm, "end": v(79.28, 2205.43) * mm});
            skLineSegment(sketch, "E7.4", {"start": v(79.28, 2205.43) * mm, "end": v(85.52, 2194.64) * mm});
            skLineSegment(sketch, "E7.5", {"start": v(85.52, 2194.64) * mm, "end": v(79.28, 2183.85) * mm});
            skPoint(sketch, "E7.0.midPoint", {"position": v(73.05, 2183.85) * mm});
            skLineSegment(sketch, "E8.0.1.0", {"start": v(66.82, 2033.98) * mm, "end": v(79.28, 2033.98) * mm});
            skLineSegment(sketch, "E8.0.1.1", {"start": v(60.6, 2023.2) * mm, "end": v(66.82, 2033.98) * mm});
            skLineSegment(sketch, "E8.0.1.2", {"start": v(66.82, 2012.4) * mm, "end": v(60.6, 2023.2) * mm});
            skLineSegment(sketch, "E8.0.1.3", {"start": v(79.28, 2012.4) * mm, "end": v(66.82, 2012.4) * mm});
            skLineSegment(sketch, "E8.0.1.4", {"start": v(85.52, 2023.2) * mm, "end": v(79.28, 2012.4) * mm});
            skLineSegment(sketch, "E8.0.1.5", {"start": v(79.28, 2033.98) * mm, "end": v(85.52, 2023.2) * mm});
            skLineSegment(sketch, "E8.0.2.0", {"start": v(66.82, 1862.53) * mm, "end": v(79.28, 1862.53) * mm});
            skLineSegment(sketch, "E8.0.2.1", {"start": v(60.6, 1851.74) * mm, "end": v(66.82, 1862.53) * mm});
            skLineSegment(sketch, "E8.0.2.2", {"start": v(66.82, 1840.95) * mm, "end": v(60.6, 1851.74) * mm});
            skLineSegment(sketch, "E8.0.2.3", {"start": v(79.28, 1840.95) * mm, "end": v(66.82, 1840.95) * mm});
            skLineSegment(sketch, "E8.0.2.4", {"start": v(85.52, 1851.74) * mm, "end": v(79.28, 1840.95) * mm});
            skLineSegment(sketch, "E8.0.2.5", {"start": v(79.28, 1862.53) * mm, "end": v(85.52, 1851.74) * mm});
            skLineSegment(sketch, "E8.0.3.0", {"start": v(66.82, 1691.08) * mm, "end": v(79.28, 1691.08) * mm});
            skLineSegment(sketch, "E8.0.3.1", {"start": v(60.6, 1680.3) * mm, "end": v(66.82, 1691.08) * mm});
            skLineSegment(sketch, "E8.0.3.2", {"start": v(66.82, 1669.5) * mm, "end": v(60.6, 1680.3) * mm});
            skLineSegment(sketch, "E8.0.3.3", {"start": v(79.28, 1669.5) * mm, "end": v(66.82, 1669.5) * mm});
            skLineSegment(sketch, "E8.0.3.4", {"start": v(85.52, 1680.3) * mm, "end": v(79.28, 1669.5) * mm});
            skLineSegment(sketch, "E8.0.3.5", {"start": v(79.28, 1691.08) * mm, "end": v(85.52, 1680.3) * mm});
            skLineSegment(sketch, "E8.0.4.0", {"start": v(66.82, 1519.63) * mm, "end": v(79.28, 1519.63) * mm});
            skLineSegment(sketch, "E8.0.4.1", {"start": v(60.6, 1508.84) * mm, "end": v(66.82, 1519.63) * mm});
            skLineSegment(sketch, "E8.0.4.2", {"start": v(66.82, 1498.05) * mm, "end": v(60.6, 1508.84) * mm});
            skLineSegment(sketch, "E8.0.4.3", {"start": v(79.28, 1498.05) * mm, "end": v(66.82, 1498.05) * mm});
            skLineSegment(sketch, "E8.0.4.4", {"start": v(85.52, 1508.84) * mm, "end": v(79.28, 1498.05) * mm});
            skLineSegment(sketch, "E8.0.4.5", {"start": v(79.28, 1519.63) * mm, "end": v(85.52, 1508.84) * mm});
            skLineSegment(sketch, "E8.0.5.0", {"start": v(66.82, 1348.18) * mm, "end": v(79.28, 1348.18) * mm});
            skLineSegment(sketch, "E8.0.5.1", {"start": v(60.6, 1337.4) * mm, "end": v(66.82, 1348.18) * mm});
            skLineSegment(sketch, "E8.0.5.2", {"start": v(66.82, 1326.6) * mm, "end": v(60.6, 1337.4) * mm});
            skLineSegment(sketch, "E8.0.5.3", {"start": v(79.28, 1326.6) * mm, "end": v(66.82, 1326.6) * mm});
            skLineSegment(sketch, "E8.0.5.4", {"start": v(85.52, 1337.4) * mm, "end": v(79.28, 1326.6) * mm});
            skLineSegment(sketch, "E8.0.5.5", {"start": v(79.28, 1348.18) * mm, "end": v(85.52, 1337.4) * mm});
            skLineSegment(sketch, "E8.0.6.0", {"start": v(66.82, 1176.73) * mm, "end": v(79.28, 1176.73) * mm});
            skLineSegment(sketch, "E8.0.6.1", {"start": v(60.6, 1165.94) * mm, "end": v(66.82, 1176.73) * mm});
            skLineSegment(sketch, "E8.0.6.2", {"start": v(66.82, 1155.15) * mm, "end": v(60.6, 1165.94) * mm});
            skLineSegment(sketch, "E8.0.6.3", {"start": v(79.28, 1155.15) * mm, "end": v(66.82, 1155.15) * mm});
            skLineSegment(sketch, "E8.0.6.4", {"start": v(85.52, 1165.94) * mm, "end": v(79.28, 1155.15) * mm});
            skLineSegment(sketch, "E8.0.6.5", {"start": v(79.28, 1176.73) * mm, "end": v(85.52, 1165.94) * mm});
            skLineSegment(sketch, "E8.0.7.0", {"start": v(66.82, 1005.28) * mm, "end": v(79.28, 1005.28) * mm});
            skLineSegment(sketch, "E8.0.7.1", {"start": v(60.6, 994.5) * mm, "end": v(66.82, 1005.28) * mm});
            skLineSegment(sketch, "E8.0.7.2", {"start": v(66.82, 983.7) * mm, "end": v(60.6, 994.5) * mm});
            skLineSegment(sketch, "E8.0.7.3", {"start": v(79.28, 983.7) * mm, "end": v(66.82, 983.7) * mm});
            skLineSegment(sketch, "E8.0.7.4", {"start": v(85.52, 994.5) * mm, "end": v(79.28, 983.7) * mm});
            skLineSegment(sketch, "E8.0.7.5", {"start": v(79.28, 1005.28) * mm, "end": v(85.52, 994.5) * mm});
            skLineSegment(sketch, "E8.1.0.0", {"start": v(231.92, 2205.43) * mm, "end": v(244.38, 2205.43) * mm});
            skLineSegment(sketch, "E8.1.0.1", {"start": v(225.7, 2194.64) * mm, "end": v(231.92, 2205.43) * mm});
            skLineSegment(sketch, "E8.1.0.2", {"start": v(231.92, 2183.85) * mm, "end": v(225.7, 2194.64) * mm});
            skLineSegment(sketch, "E8.1.0.3", {"start": v(244.38, 2183.85) * mm, "end": v(231.92, 2183.85) * mm});
            skLineSegment(sketch, "E8.1.0.4", {"start": v(250.62, 2194.64) * mm, "end": v(244.38, 2183.85) * mm});
            skLineSegment(sketch, "E8.1.0.5", {"start": v(244.38, 2205.43) * mm, "end": v(250.62, 2194.64) * mm});
            skLineSegment(sketch, "E8.1.1.0", {"start": v(231.92, 2033.98) * mm, "end": v(244.38, 2033.98) * mm});
            skLineSegment(sketch, "E8.1.1.1", {"start": v(225.7, 2023.2) * mm, "end": v(231.92, 2033.98) * mm});
            skLineSegment(sketch, "E8.1.1.2", {"start": v(231.92, 2012.4) * mm, "end": v(225.7, 2023.2) * mm});
            skLineSegment(sketch, "E8.1.1.3", {"start": v(244.38, 2012.4) * mm, "end": v(231.92, 2012.4) * mm});
            skLineSegment(sketch, "E8.1.1.4", {"start": v(250.62, 2023.2) * mm, "end": v(244.38, 2012.4) * mm});
            skLineSegment(sketch, "E8.1.1.5", {"start": v(244.38, 2033.98) * mm, "end": v(250.62, 2023.2) * mm});
            skLineSegment(sketch, "E8.1.2.0", {"start": v(231.92, 1862.53) * mm, "end": v(244.38, 1862.53) * mm});
            skLineSegment(sketch, "E8.1.2.1", {"start": v(225.7, 1851.74) * mm, "end": v(231.92, 1862.53) * mm});
            skLineSegment(sketch, "E8.1.2.2", {"start": v(231.92, 1840.95) * mm, "end": v(225.7, 1851.74) * mm});
            skLineSegment(sketch, "E8.1.2.3", {"start": v(244.38, 1840.95) * mm, "end": v(231.92, 1840.95) * mm});
            skLineSegment(sketch, "E8.1.2.4", {"start": v(250.62, 1851.74) * mm, "end": v(244.38, 1840.95) * mm});
            skLineSegment(sketch, "E8.1.2.5", {"start": v(244.38, 1862.53) * mm, "end": v(250.62, 1851.74) * mm});
            skLineSegment(sketch, "E8.1.3.0", {"start": v(231.92, 1691.08) * mm, "end": v(244.38, 1691.08) * mm});
            skLineSegment(sketch, "E8.1.3.1", {"start": v(225.7, 1680.3) * mm, "end": v(231.92, 1691.08) * mm});
            skLineSegment(sketch, "E8.1.3.2", {"start": v(231.92, 1669.5) * mm, "end": v(225.7, 1680.3) * mm});
            skLineSegment(sketch, "E8.1.3.3", {"start": v(244.38, 1669.5) * mm, "end": v(231.92, 1669.5) * mm});
            skLineSegment(sketch, "E8.1.3.4", {"start": v(250.62, 1680.3) * mm, "end": v(244.38, 1669.5) * mm});
            skLineSegment(sketch, "E8.1.3.5", {"start": v(244.38, 1691.08) * mm, "end": v(250.62, 1680.3) * mm});
            skLineSegment(sketch, "E8.1.4.0", {"start": v(231.92, 1519.63) * mm, "end": v(244.38, 1519.63) * mm});
            skLineSegment(sketch, "E8.1.4.1", {"start": v(225.7, 1508.84) * mm, "end": v(231.92, 1519.63) * mm});
            skLineSegment(sketch, "E8.1.4.2", {"start": v(231.92, 1498.05) * mm, "end": v(225.7, 1508.84) * mm});
            skLineSegment(sketch, "E8.1.4.3", {"start": v(244.38, 1498.05) * mm, "end": v(231.92, 1498.05) * mm});
            skLineSegment(sketch, "E8.1.4.4", {"start": v(250.62, 1508.84) * mm, "end": v(244.38, 1498.05) * mm});
            skLineSegment(sketch, "E8.1.4.5", {"start": v(244.38, 1519.63) * mm, "end": v(250.62, 1508.84) * mm});
            skLineSegment(sketch, "E8.1.5.0", {"start": v(231.92, 1348.18) * mm, "end": v(244.38, 1348.18) * mm});
            skLineSegment(sketch, "E8.1.5.1", {"start": v(225.7, 1337.4) * mm, "end": v(231.92, 1348.18) * mm});
            skLineSegment(sketch, "E8.1.5.2", {"start": v(231.92, 1326.6) * mm, "end": v(225.7, 1337.4) * mm});
            skLineSegment(sketch, "E8.1.5.3", {"start": v(244.38, 1326.6) * mm, "end": v(231.92, 1326.6) * mm});
            skLineSegment(sketch, "E8.1.5.4", {"start": v(250.62, 1337.4) * mm, "end": v(244.38, 1326.6) * mm});
            skLineSegment(sketch, "E8.1.5.5", {"start": v(244.38, 1348.18) * mm, "end": v(250.62, 1337.4) * mm});
            skLineSegment(sketch, "E8.1.6.0", {"start": v(231.92, 1176.73) * mm, "end": v(244.38, 1176.73) * mm});
            skLineSegment(sketch, "E8.1.6.1", {"start": v(225.7, 1165.94) * mm, "end": v(231.92, 1176.73) * mm});
            skLineSegment(sketch, "E8.1.6.2", {"start": v(231.92, 1155.15) * mm, "end": v(225.7, 1165.94) * mm});
            skLineSegment(sketch, "E8.1.6.3", {"start": v(244.38, 1155.15) * mm, "end": v(231.92, 1155.15) * mm});
            skLineSegment(sketch, "E8.1.6.4", {"start": v(250.62, 1165.94) * mm, "end": v(244.38, 1155.15) * mm});
            skLineSegment(sketch, "E8.1.6.5", {"start": v(244.38, 1176.73) * mm, "end": v(250.62, 1165.94) * mm});
            skLineSegment(sketch, "E8.1.7.0", {"start": v(231.92, 1005.28) * mm, "end": v(244.38, 1005.28) * mm});
            skLineSegment(sketch, "E8.1.7.1", {"start": v(225.7, 994.5) * mm, "end": v(231.92, 1005.28) * mm});
            skLineSegment(sketch, "E8.1.7.2", {"start": v(231.92, 983.7) * mm, "end": v(225.7, 994.5) * mm});
            skLineSegment(sketch, "E8.1.7.3", {"start": v(244.38, 983.7) * mm, "end": v(231.92, 983.7) * mm});
            skLineSegment(sketch, "E8.1.7.4", {"start": v(250.62, 994.5) * mm, "end": v(244.38, 983.7) * mm});
            skLineSegment(sketch, "E8.1.7.5", {"start": v(244.38, 1005.28) * mm, "end": v(250.62, 994.5) * mm});
            skLineSegment(sketch, "E8.2.0.0", {"start": v(397.02, 2205.43) * mm, "end": v(409.48, 2205.43) * mm});
            skLineSegment(sketch, "E8.2.0.1", {"start": v(390.8, 2194.64) * mm, "end": v(397.02, 2205.43) * mm});
            skLineSegment(sketch, "E8.2.0.2", {"start": v(397.02, 2183.85) * mm, "end": v(390.8, 2194.64) * mm});
            skLineSegment(sketch, "E8.2.0.3", {"start": v(409.48, 2183.85) * mm, "end": v(397.02, 2183.85) * mm});
            skLineSegment(sketch, "E8.2.0.4", {"start": v(415.72, 2194.64) * mm, "end": v(409.48, 2183.85) * mm});
            skLineSegment(sketch, "E8.2.0.5", {"start": v(409.48, 2205.43) * mm, "end": v(415.72, 2194.64) * mm});
            skLineSegment(sketch, "E8.2.1.0", {"start": v(397.02, 2033.98) * mm, "end": v(409.48, 2033.98) * mm});
            skLineSegment(sketch, "E8.2.1.1", {"start": v(390.8, 2023.2) * mm, "end": v(397.02, 2033.98) * mm});
            skLineSegment(sketch, "E8.2.1.2", {"start": v(397.02, 2012.4) * mm, "end": v(390.8, 2023.2) * mm});
            skLineSegment(sketch, "E8.2.1.3", {"start": v(409.48, 2012.4) * mm, "end": v(397.02, 2012.4) * mm});
            skLineSegment(sketch, "E8.2.1.4", {"start": v(415.72, 2023.2) * mm, "end": v(409.48, 2012.4) * mm});
            skLineSegment(sketch, "E8.2.1.5", {"start": v(409.48, 2033.98) * mm, "end": v(415.72, 2023.2) * mm});
            skLineSegment(sketch, "E8.2.2.0", {"start": v(397.02, 1862.53) * mm, "end": v(409.48, 1862.53) * mm});
            skLineSegment(sketch, "E8.2.2.1", {"start": v(390.8, 1851.74) * mm, "end": v(397.02, 1862.53) * mm});
            skLineSegment(sketch, "E8.2.2.2", {"start": v(397.02, 1840.95) * mm, "end": v(390.8, 1851.74) * mm});
            skLineSegment(sketch, "E8.2.2.3", {"start": v(409.48, 1840.95) * mm, "end": v(397.02, 1840.95) * mm});
            skLineSegment(sketch, "E8.2.2.4", {"start": v(415.72, 1851.74) * mm, "end": v(409.48, 1840.95) * mm});
            skLineSegment(sketch, "E8.2.2.5", {"start": v(409.48, 1862.53) * mm, "end": v(415.72, 1851.74) * mm});
            skLineSegment(sketch, "E8.2.3.0", {"start": v(397.02, 1691.08) * mm, "end": v(409.48, 1691.08) * mm});
            skLineSegment(sketch, "E8.2.3.1", {"start": v(390.8, 1680.3) * mm, "end": v(397.02, 1691.08) * mm});
            skLineSegment(sketch, "E8.2.3.2", {"start": v(397.02, 1669.5) * mm, "end": v(390.8, 1680.3) * mm});
            skLineSegment(sketch, "E8.2.3.3", {"start": v(409.48, 1669.5) * mm, "end": v(397.02, 1669.5) * mm});
            skLineSegment(sketch, "E8.2.3.4", {"start": v(415.72, 1680.3) * mm, "end": v(409.48, 1669.5) * mm});
            skLineSegment(sketch, "E8.2.3.5", {"start": v(409.48, 1691.08) * mm, "end": v(415.72, 1680.3) * mm});
            skLineSegment(sketch, "E8.2.4.0", {"start": v(397.02, 1519.63) * mm, "end": v(409.48, 1519.63) * mm});
            skLineSegment(sketch, "E8.2.4.1", {"start": v(390.8, 1508.84) * mm, "end": v(397.02, 1519.63) * mm});
            skLineSegment(sketch, "E8.2.4.2", {"start": v(397.02, 1498.05) * mm, "end": v(390.8, 1508.84) * mm});
            skLineSegment(sketch, "E8.2.4.3", {"start": v(409.48, 1498.05) * mm, "end": v(397.02, 1498.05) * mm});
            skLineSegment(sketch, "E8.2.4.4", {"start": v(415.72, 1508.84) * mm, "end": v(409.48, 1498.05) * mm});
            skLineSegment(sketch, "E8.2.4.5", {"start": v(409.48, 1519.63) * mm, "end": v(415.72, 1508.84) * mm});
            skLineSegment(sketch, "E8.2.5.0", {"start": v(397.02, 1348.18) * mm, "end": v(409.48, 1348.18) * mm});
            skLineSegment(sketch, "E8.2.5.1", {"start": v(390.8, 1337.4) * mm, "end": v(397.02, 1348.18) * mm});
            skLineSegment(sketch, "E8.2.5.2", {"start": v(397.02, 1326.6) * mm, "end": v(390.8, 1337.4) * mm});
            skLineSegment(sketch, "E8.2.5.3", {"start": v(409.48, 1326.6) * mm, "end": v(397.02, 1326.6) * mm});
            skLineSegment(sketch, "E8.2.5.4", {"start": v(415.72, 1337.4) * mm, "end": v(409.48, 1326.6) * mm});
            skLineSegment(sketch, "E8.2.5.5", {"start": v(409.48, 1348.18) * mm, "end": v(415.72, 1337.4) * mm});
            skLineSegment(sketch, "E8.2.6.0", {"start": v(397.02, 1176.73) * mm, "end": v(409.48, 1176.73) * mm});
            skLineSegment(sketch, "E8.2.6.1", {"start": v(390.8, 1165.94) * mm, "end": v(397.02, 1176.73) * mm});
            skLineSegment(sketch, "E8.2.6.2", {"start": v(397.02, 1155.15) * mm, "end": v(390.8, 1165.94) * mm});
            skLineSegment(sketch, "E8.2.6.3", {"start": v(409.48, 1155.15) * mm, "end": v(397.02, 1155.15) * mm});
            skLineSegment(sketch, "E8.2.6.4", {"start": v(415.72, 1165.94) * mm, "end": v(409.48, 1155.15) * mm});
            skLineSegment(sketch, "E8.2.6.5", {"start": v(409.48, 1176.73) * mm, "end": v(415.72, 1165.94) * mm});
            skLineSegment(sketch, "E8.2.7.0", {"start": v(397.02, 1005.28) * mm, "end": v(409.48, 1005.28) * mm});
            skLineSegment(sketch, "E8.2.7.1", {"start": v(390.8, 994.5) * mm, "end": v(397.02, 1005.28) * mm});
            skLineSegment(sketch, "E8.2.7.2", {"start": v(397.02, 983.7) * mm, "end": v(390.8, 994.5) * mm});
            skLineSegment(sketch, "E8.2.7.3", {"start": v(409.48, 983.7) * mm, "end": v(397.02, 983.7) * mm});
            skLineSegment(sketch, "E8.2.7.4", {"start": v(415.72, 994.5) * mm, "end": v(409.48, 983.7) * mm});
            skLineSegment(sketch, "E8.2.7.5", {"start": v(409.48, 1005.28) * mm, "end": v(415.72, 994.5) * mm});
            skLineSegment(sketch, "E8.3.0.0", {"start": v(562.12, 2205.43) * mm, "end": v(574.58, 2205.43) * mm});
            skLineSegment(sketch, "E8.3.0.1", {"start": v(555.9, 2194.64) * mm, "end": v(562.12, 2205.43) * mm});
            skLineSegment(sketch, "E8.3.0.2", {"start": v(562.12, 2183.85) * mm, "end": v(555.9, 2194.64) * mm});
            skLineSegment(sketch, "E8.3.0.3", {"start": v(574.58, 2183.85) * mm, "end": v(562.12, 2183.85) * mm});
            skLineSegment(sketch, "E8.3.0.4", {"start": v(580.82, 2194.64) * mm, "end": v(574.58, 2183.85) * mm});
            skLineSegment(sketch, "E8.3.0.5", {"start": v(574.58, 2205.43) * mm, "end": v(580.82, 2194.64) * mm});
            skLineSegment(sketch, "E8.3.1.0", {"start": v(562.12, 2033.98) * mm, "end": v(574.58, 2033.98) * mm});
            skLineSegment(sketch, "E8.3.1.1", {"start": v(555.9, 2023.2) * mm, "end": v(562.12, 2033.98) * mm});
            skLineSegment(sketch, "E8.3.1.2", {"start": v(562.12, 2012.4) * mm, "end": v(555.9, 2023.2) * mm});
            skLineSegment(sketch, "E8.3.1.3", {"start": v(574.58, 2012.4) * mm, "end": v(562.12, 2012.4) * mm});
            skLineSegment(sketch, "E8.3.1.4", {"start": v(580.82, 2023.2) * mm, "end": v(574.58, 2012.4) * mm});
            skLineSegment(sketch, "E8.3.1.5", {"start": v(574.58, 2033.98) * mm, "end": v(580.82, 2023.2) * mm});
            skLineSegment(sketch, "E8.3.2.0", {"start": v(562.12, 1862.53) * mm, "end": v(574.58, 1862.53) * mm});
            skLineSegment(sketch, "E8.3.2.1", {"start": v(555.9, 1851.74) * mm, "end": v(562.12, 1862.53) * mm});
            skLineSegment(sketch, "E8.3.2.2", {"start": v(562.12, 1840.95) * mm, "end": v(555.9, 1851.74) * mm});
            skLineSegment(sketch, "E8.3.2.3", {"start": v(574.58, 1840.95) * mm, "end": v(562.12, 1840.95) * mm});
            skLineSegment(sketch, "E8.3.2.4", {"start": v(580.82, 1851.74) * mm, "end": v(574.58, 1840.95) * mm});
            skLineSegment(sketch, "E8.3.2.5", {"start": v(574.58, 1862.53) * mm, "end": v(580.82, 1851.74) * mm});
            skLineSegment(sketch, "E8.3.3.0", {"start": v(562.12, 1691.08) * mm, "end": v(574.58, 1691.08) * mm});
            skLineSegment(sketch, "E8.3.3.1", {"start": v(555.9, 1680.3) * mm, "end": v(562.12, 1691.08) * mm});
            skLineSegment(sketch, "E8.3.3.2", {"start": v(562.12, 1669.5) * mm, "end": v(555.9, 1680.3) * mm});
            skLineSegment(sketch, "E8.3.3.3", {"start": v(574.58, 1669.5) * mm, "end": v(562.12, 1669.5) * mm});
            skLineSegment(sketch, "E8.3.3.4", {"start": v(580.82, 1680.3) * mm, "end": v(574.58, 1669.5) * mm});
            skLineSegment(sketch, "E8.3.3.5", {"start": v(574.58, 1691.08) * mm, "end": v(580.82, 1680.3) * mm});
            skLineSegment(sketch, "E8.3.4.0", {"start": v(562.12, 1519.63) * mm, "end": v(574.58, 1519.63) * mm});
            skLineSegment(sketch, "E8.3.4.1", {"start": v(555.9, 1508.84) * mm, "end": v(562.12, 1519.63) * mm});
            skLineSegment(sketch, "E8.3.4.2", {"start": v(562.12, 1498.05) * mm, "end": v(555.9, 1508.84) * mm});
            skLineSegment(sketch, "E8.3.4.3", {"start": v(574.58, 1498.05) * mm, "end": v(562.12, 1498.05) * mm});
            skLineSegment(sketch, "E8.3.4.4", {"start": v(580.82, 1508.84) * mm, "end": v(574.58, 1498.05) * mm});
            skLineSegment(sketch, "E8.3.4.5", {"start": v(574.58, 1519.63) * mm, "end": v(580.82, 1508.84) * mm});
            skLineSegment(sketch, "E8.3.5.0", {"start": v(562.12, 1348.18) * mm, "end": v(574.58, 1348.18) * mm});
            skLineSegment(sketch, "E8.3.5.1", {"start": v(555.9, 1337.4) * mm, "end": v(562.12, 1348.18) * mm});
            skLineSegment(sketch, "E8.3.5.2", {"start": v(562.12, 1326.6) * mm, "end": v(555.9, 1337.4) * mm});
            skLineSegment(sketch, "E8.3.5.3", {"start": v(574.58, 1326.6) * mm, "end": v(562.12, 1326.6) * mm});
            skLineSegment(sketch, "E8.3.5.4", {"start": v(580.82, 1337.4) * mm, "end": v(574.58, 1326.6) * mm});
            skLineSegment(sketch, "E8.3.5.5", {"start": v(574.58, 1348.18) * mm, "end": v(580.82, 1337.4) * mm});
            skLineSegment(sketch, "E8.3.6.0", {"start": v(562.12, 1176.73) * mm, "end": v(574.58, 1176.73) * mm});
            skLineSegment(sketch, "E8.3.6.1", {"start": v(555.9, 1165.94) * mm, "end": v(562.12, 1176.73) * mm});
            skLineSegment(sketch, "E8.3.6.2", {"start": v(562.12, 1155.15) * mm, "end": v(555.9, 1165.94) * mm});
            skLineSegment(sketch, "E8.3.6.3", {"start": v(574.58, 1155.15) * mm, "end": v(562.12, 1155.15) * mm});
            skLineSegment(sketch, "E8.3.6.4", {"start": v(580.82, 1165.94) * mm, "end": v(574.58, 1155.15) * mm});
            skLineSegment(sketch, "E8.3.6.5", {"start": v(574.58, 1176.73) * mm, "end": v(580.82, 1165.94) * mm});
            skLineSegment(sketch, "E8.3.7.0", {"start": v(562.12, 1005.28) * mm, "end": v(574.58, 1005.28) * mm});
            skLineSegment(sketch, "E8.3.7.1", {"start": v(555.9, 994.5) * mm, "end": v(562.12, 1005.28) * mm});
            skLineSegment(sketch, "E8.3.7.2", {"start": v(562.12, 983.7) * mm, "end": v(555.9, 994.5) * mm});
            skLineSegment(sketch, "E8.3.7.3", {"start": v(574.58, 983.7) * mm, "end": v(562.12, 983.7) * mm});
            skLineSegment(sketch, "E8.3.7.4", {"start": v(580.82, 994.5) * mm, "end": v(574.58, 983.7) * mm});
            skLineSegment(sketch, "E8.3.7.5", {"start": v(574.58, 1005.28) * mm, "end": v(580.82, 994.5) * mm});
            skLineSegment(sketch, "E8.4.0.0", {"start": v(727.22, 2205.43) * mm, "end": v(739.68, 2205.43) * mm});
            skLineSegment(sketch, "E8.4.0.1", {"start": v(721, 2194.64) * mm, "end": v(727.22, 2205.43) * mm});
            skLineSegment(sketch, "E8.4.0.2", {"start": v(727.22, 2183.85) * mm, "end": v(721, 2194.64) * mm});
            skLineSegment(sketch, "E8.4.0.3", {"start": v(739.68, 2183.85) * mm, "end": v(727.22, 2183.85) * mm});
            skLineSegment(sketch, "E8.4.0.4", {"start": v(745.92, 2194.64) * mm, "end": v(739.68, 2183.85) * mm});
            skLineSegment(sketch, "E8.4.0.5", {"start": v(739.68, 2205.43) * mm, "end": v(745.92, 2194.64) * mm});
            skLineSegment(sketch, "E8.4.1.0", {"start": v(727.22, 2033.98) * mm, "end": v(739.68, 2033.98) * mm});
            skLineSegment(sketch, "E8.4.1.1", {"start": v(721, 2023.2) * mm, "end": v(727.22, 2033.98) * mm});
            skLineSegment(sketch, "E8.4.1.2", {"start": v(727.22, 2012.4) * mm, "end": v(721, 2023.2) * mm});
            skLineSegment(sketch, "E8.4.1.3", {"start": v(739.68, 2012.4) * mm, "end": v(727.22, 2012.4) * mm});
            skLineSegment(sketch, "E8.4.1.4", {"start": v(745.92, 2023.2) * mm, "end": v(739.68, 2012.4) * mm});
            skLineSegment(sketch, "E8.4.1.5", {"start": v(739.68, 2033.98) * mm, "end": v(745.92, 2023.2) * mm});
            skLineSegment(sketch, "E8.4.2.0", {"start": v(727.22, 1862.53) * mm, "end": v(739.68, 1862.53) * mm});
            skLineSegment(sketch, "E8.4.2.1", {"start": v(721, 1851.74) * mm, "end": v(727.22, 1862.53) * mm});
            skLineSegment(sketch, "E8.4.2.2", {"start": v(727.22, 1840.95) * mm, "end": v(721, 1851.74) * mm});
            skLineSegment(sketch, "E8.4.2.3", {"start": v(739.68, 1840.95) * mm, "end": v(727.22, 1840.95) * mm});
            skLineSegment(sketch, "E8.4.2.4", {"start": v(745.92, 1851.74) * mm, "end": v(739.68, 1840.95) * mm});
            skLineSegment(sketch, "E8.4.2.5", {"start": v(739.68, 1862.53) * mm, "end": v(745.92, 1851.74) * mm});
            skLineSegment(sketch, "E8.4.3.0", {"start": v(727.22, 1691.08) * mm, "end": v(739.68, 1691.08) * mm});
            skLineSegment(sketch, "E8.4.3.1", {"start": v(721, 1680.3) * mm, "end": v(727.22, 1691.08) * mm});
            skLineSegment(sketch, "E8.4.3.2", {"start": v(727.22, 1669.5) * mm, "end": v(721, 1680.3) * mm});
            skLineSegment(sketch, "E8.4.3.3", {"start": v(739.68, 1669.5) * mm, "end": v(727.22, 1669.5) * mm});
            skLineSegment(sketch, "E8.4.3.4", {"start": v(745.92, 1680.3) * mm, "end": v(739.68, 1669.5) * mm});
            skLineSegment(sketch, "E8.4.3.5", {"start": v(739.68, 1691.08) * mm, "end": v(745.92, 1680.3) * mm});
            skLineSegment(sketch, "E8.4.4.0", {"start": v(727.22, 1519.63) * mm, "end": v(739.68, 1519.63) * mm});
            skLineSegment(sketch, "E8.4.4.1", {"start": v(721, 1508.84) * mm, "end": v(727.22, 1519.63) * mm});
            skLineSegment(sketch, "E8.4.4.2", {"start": v(727.22, 1498.05) * mm, "end": v(721, 1508.84) * mm});
            skLineSegment(sketch, "E8.4.4.3", {"start": v(739.68, 1498.05) * mm, "end": v(727.22, 1498.05) * mm});
            skLineSegment(sketch, "E8.4.4.4", {"start": v(745.92, 1508.84) * mm, "end": v(739.68, 1498.05) * mm});
            skLineSegment(sketch, "E8.4.4.5", {"start": v(739.68, 1519.63) * mm, "end": v(745.92, 1508.84) * mm});
            skLineSegment(sketch, "E8.4.5.0", {"start": v(727.22, 1348.18) * mm, "end": v(739.68, 1348.18) * mm});
            skLineSegment(sketch, "E8.4.5.1", {"start": v(721, 1337.4) * mm, "end": v(727.22, 1348.18) * mm});
            skLineSegment(sketch, "E8.4.5.2", {"start": v(727.22, 1326.6) * mm, "end": v(721, 1337.4) * mm});
            skLineSegment(sketch, "E8.4.5.3", {"start": v(739.68, 1326.6) * mm, "end": v(727.22, 1326.6) * mm});
            skLineSegment(sketch, "E8.4.5.4", {"start": v(745.92, 1337.4) * mm, "end": v(739.68, 1326.6) * mm});
            skLineSegment(sketch, "E8.4.5.5", {"start": v(739.68, 1348.18) * mm, "end": v(745.92, 1337.4) * mm});
            skLineSegment(sketch, "E8.4.6.0", {"start": v(727.22, 1176.73) * mm, "end": v(739.68, 1176.73) * mm});
            skLineSegment(sketch, "E8.4.6.1", {"start": v(721, 1165.94) * mm, "end": v(727.22, 1176.73) * mm});
            skLineSegment(sketch, "E8.4.6.2", {"start": v(727.22, 1155.15) * mm, "end": v(721, 1165.94) * mm});
            skLineSegment(sketch, "E8.4.6.3", {"start": v(739.68, 1155.15) * mm, "end": v(727.22, 1155.15) * mm});
            skLineSegment(sketch, "E8.4.6.4", {"start": v(745.92, 1165.94) * mm, "end": v(739.68, 1155.15) * mm});
            skLineSegment(sketch, "E8.4.6.5", {"start": v(739.68, 1176.73) * mm, "end": v(745.92, 1165.94) * mm});
            skLineSegment(sketch, "E8.4.7.0", {"start": v(727.22, 1005.28) * mm, "end": v(739.68, 1005.28) * mm});
            skLineSegment(sketch, "E8.4.7.1", {"start": v(721, 994.5) * mm, "end": v(727.22, 1005.28) * mm});
            skLineSegment(sketch, "E8.4.7.2", {"start": v(727.22, 983.7) * mm, "end": v(721, 994.5) * mm});
            skLineSegment(sketch, "E8.4.7.3", {"start": v(739.68, 983.7) * mm, "end": v(727.22, 983.7) * mm});
            skLineSegment(sketch, "E8.4.7.4", {"start": v(745.92, 994.5) * mm, "end": v(739.68, 983.7) * mm});
            skLineSegment(sketch, "E8.4.7.5", {"start": v(739.68, 1005.28) * mm, "end": v(745.92, 994.5) * mm});
            skLineSegment(sketch, "E8.5.0.0", {"start": v(892.32, 2205.43) * mm, "end": v(904.78, 2205.43) * mm});
            skLineSegment(sketch, "E8.5.0.1", {"start": v(886.1, 2194.64) * mm, "end": v(892.32, 2205.43) * mm});
            skLineSegment(sketch, "E8.5.0.2", {"start": v(892.32, 2183.85) * mm, "end": v(886.1, 2194.64) * mm});
            skLineSegment(sketch, "E8.5.0.3", {"start": v(904.78, 2183.85) * mm, "end": v(892.32, 2183.85) * mm});
            skLineSegment(sketch, "E8.5.0.4", {"start": v(911.02, 2194.64) * mm, "end": v(904.78, 2183.85) * mm});
            skLineSegment(sketch, "E8.5.0.5", {"start": v(904.78, 2205.43) * mm, "end": v(911.02, 2194.64) * mm});
            skLineSegment(sketch, "E8.5.1.0", {"start": v(892.32, 2033.98) * mm, "end": v(904.78, 2033.98) * mm});
            skLineSegment(sketch, "E8.5.1.1", {"start": v(886.1, 2023.2) * mm, "end": v(892.32, 2033.98) * mm});
            skLineSegment(sketch, "E8.5.1.2", {"start": v(892.32, 2012.4) * mm, "end": v(886.1, 2023.2) * mm});
            skLineSegment(sketch, "E8.5.1.3", {"start": v(904.78, 2012.4) * mm, "end": v(892.32, 2012.4) * mm});
            skLineSegment(sketch, "E8.5.1.4", {"start": v(911.02, 2023.2) * mm, "end": v(904.78, 2012.4) * mm});
            skLineSegment(sketch, "E8.5.1.5", {"start": v(904.78, 2033.98) * mm, "end": v(911.02, 2023.2) * mm});
            skLineSegment(sketch, "E8.5.2.0", {"start": v(892.32, 1862.53) * mm, "end": v(904.78, 1862.53) * mm});
            skLineSegment(sketch, "E8.5.2.1", {"start": v(886.1, 1851.74) * mm, "end": v(892.32, 1862.53) * mm});
            skLineSegment(sketch, "E8.5.2.2", {"start": v(892.32, 1840.95) * mm, "end": v(886.1, 1851.74) * mm});
            skLineSegment(sketch, "E8.5.2.3", {"start": v(904.78, 1840.95) * mm, "end": v(892.32, 1840.95) * mm});
            skLineSegment(sketch, "E8.5.2.4", {"start": v(911.02, 1851.74) * mm, "end": v(904.78, 1840.95) * mm});
            skLineSegment(sketch, "E8.5.2.5", {"start": v(904.78, 1862.53) * mm, "end": v(911.02, 1851.74) * mm});
            skLineSegment(sketch, "E8.5.3.0", {"start": v(892.32, 1691.08) * mm, "end": v(904.78, 1691.08) * mm});
            skLineSegment(sketch, "E8.5.3.1", {"start": v(886.1, 1680.3) * mm, "end": v(892.32, 1691.08) * mm});
            skLineSegment(sketch, "E8.5.3.2", {"start": v(892.32, 1669.5) * mm, "end": v(886.1, 1680.3) * mm});
            skLineSegment(sketch, "E8.5.3.3", {"start": v(904.78, 1669.5) * mm, "end": v(892.32, 1669.5) * mm});
            skLineSegment(sketch, "E8.5.3.4", {"start": v(911.02, 1680.3) * mm, "end": v(904.78, 1669.5) * mm});
            skLineSegment(sketch, "E8.5.3.5", {"start": v(904.78, 1691.08) * mm, "end": v(911.02, 1680.3) * mm});
            skLineSegment(sketch, "E8.5.4.0", {"start": v(892.32, 1519.63) * mm, "end": v(904.78, 1519.63) * mm});
            skLineSegment(sketch, "E8.5.4.1", {"start": v(886.1, 1508.84) * mm, "end": v(892.32, 1519.63) * mm});
            skLineSegment(sketch, "E8.5.4.2", {"start": v(892.32, 1498.05) * mm, "end": v(886.1, 1508.84) * mm});
            skLineSegment(sketch, "E8.5.4.3", {"start": v(904.78, 1498.05) * mm, "end": v(892.32, 1498.05) * mm});
            skLineSegment(sketch, "E8.5.4.4", {"start": v(911.02, 1508.84) * mm, "end": v(904.78, 1498.05) * mm});
            skLineSegment(sketch, "E8.5.4.5", {"start": v(904.78, 1519.63) * mm, "end": v(911.02, 1508.84) * mm});
            skLineSegment(sketch, "E8.5.5.0", {"start": v(892.32, 1348.18) * mm, "end": v(904.78, 1348.18) * mm});
            skLineSegment(sketch, "E8.5.5.1", {"start": v(886.1, 1337.4) * mm, "end": v(892.32, 1348.18) * mm});
            skLineSegment(sketch, "E8.5.5.2", {"start": v(892.32, 1326.6) * mm, "end": v(886.1, 1337.4) * mm});
            skLineSegment(sketch, "E8.5.5.3", {"start": v(904.78, 1326.6) * mm, "end": v(892.32, 1326.6) * mm});
            skLineSegment(sketch, "E8.5.5.4", {"start": v(911.02, 1337.4) * mm, "end": v(904.78, 1326.6) * mm});
            skLineSegment(sketch, "E8.5.5.5", {"start": v(904.78, 1348.18) * mm, "end": v(911.02, 1337.4) * mm});
            skLineSegment(sketch, "E8.5.6.0", {"start": v(892.32, 1176.73) * mm, "end": v(904.78, 1176.73) * mm});
            skLineSegment(sketch, "E8.5.6.1", {"start": v(886.1, 1165.94) * mm, "end": v(892.32, 1176.73) * mm});
            skLineSegment(sketch, "E8.5.6.2", {"start": v(892.32, 1155.15) * mm, "end": v(886.1, 1165.94) * mm});
            skLineSegment(sketch, "E8.5.6.3", {"start": v(904.78, 1155.15) * mm, "end": v(892.32, 1155.15) * mm});
            skLineSegment(sketch, "E8.5.6.4", {"start": v(911.02, 1165.94) * mm, "end": v(904.78, 1155.15) * mm});
            skLineSegment(sketch, "E8.5.6.5", {"start": v(904.78, 1176.73) * mm, "end": v(911.02, 1165.94) * mm});
            skLineSegment(sketch, "E8.5.7.0", {"start": v(892.32, 1005.28) * mm, "end": v(904.78, 1005.28) * mm});
            skLineSegment(sketch, "E8.5.7.1", {"start": v(886.1, 994.5) * mm, "end": v(892.32, 1005.28) * mm});
            skLineSegment(sketch, "E8.5.7.2", {"start": v(892.32, 983.7) * mm, "end": v(886.1, 994.5) * mm});
            skLineSegment(sketch, "E8.5.7.3", {"start": v(904.78, 983.7) * mm, "end": v(892.32, 983.7) * mm});
            skLineSegment(sketch, "E8.5.7.4", {"start": v(911.02, 994.5) * mm, "end": v(904.78, 983.7) * mm});
            skLineSegment(sketch, "E8.5.7.5", {"start": v(904.78, 1005.28) * mm, "end": v(911.02, 994.5) * mm});
            skLineSegment(sketch, "E8.direction1", {"start": v(66.82, 2205.43) * mm, "end": v(231.92, 2205.43) * mm, "construction": true});
            skLineSegment(sketch, "E8.direction2", {"start": v(66.82, 2205.43) * mm, "end": v(66.82, 2033.98) * mm, "construction": true});
            skLineSegment(sketch, "E9.0.6.0", {"start": v(1057.42, 2205.43) * mm, "end": v(1069.88, 2205.43) * mm});
            skLineSegment(sketch, "E9.3.6.0", {"start": v(1051.2, 2194.64) * mm, "end": v(1057.42, 2205.43) * mm});
            skLineSegment(sketch, "E9.6.6.0", {"start": v(1057.42, 2183.85) * mm, "end": v(1051.2, 2194.64) * mm});
            skLineSegment(sketch, "E9.9.6.0", {"start": v(1069.88, 2183.85) * mm, "end": v(1057.42, 2183.85) * mm});
            skLineSegment(sketch, "E9.12.6.0", {"start": v(1076.12, 2194.64) * mm, "end": v(1069.88, 2183.85) * mm});
            skLineSegment(sketch, "E9.15.6.0", {"start": v(1069.88, 2205.43) * mm, "end": v(1076.12, 2194.64) * mm});
            skLineSegment(sketch, "E9.0.6.1", {"start": v(1057.42, 2033.98) * mm, "end": v(1069.88, 2033.98) * mm});
            skLineSegment(sketch, "E9.3.6.1", {"start": v(1051.2, 2023.2) * mm, "end": v(1057.42, 2033.98) * mm});
            skLineSegment(sketch, "E9.6.6.1", {"start": v(1057.42, 2012.4) * mm, "end": v(1051.2, 2023.2) * mm});
            skLineSegment(sketch, "E9.9.6.1", {"start": v(1069.88, 2012.4) * mm, "end": v(1057.42, 2012.4) * mm});
            skLineSegment(sketch, "E9.12.6.1", {"start": v(1076.12, 2023.2) * mm, "end": v(1069.88, 2012.4) * mm});
            skLineSegment(sketch, "E9.15.6.1", {"start": v(1069.88, 2033.98) * mm, "end": v(1076.12, 2023.2) * mm});
            skLineSegment(sketch, "E9.0.6.2", {"start": v(1057.42, 1862.53) * mm, "end": v(1069.88, 1862.53) * mm});
            skLineSegment(sketch, "E9.3.6.2", {"start": v(1051.2, 1851.74) * mm, "end": v(1057.42, 1862.53) * mm});
            skLineSegment(sketch, "E9.6.6.2", {"start": v(1057.42, 1840.95) * mm, "end": v(1051.2, 1851.74) * mm});
            skLineSegment(sketch, "E9.9.6.2", {"start": v(1069.88, 1840.95) * mm, "end": v(1057.42, 1840.95) * mm});
            skLineSegment(sketch, "E9.12.6.2", {"start": v(1076.12, 1851.74) * mm, "end": v(1069.88, 1840.95) * mm});
            skLineSegment(sketch, "E9.15.6.2", {"start": v(1069.88, 1862.53) * mm, "end": v(1076.12, 1851.74) * mm});
            skLineSegment(sketch, "E9.0.6.3", {"start": v(1057.42, 1691.08) * mm, "end": v(1069.88, 1691.08) * mm});
            skLineSegment(sketch, "E9.3.6.3", {"start": v(1051.2, 1680.3) * mm, "end": v(1057.42, 1691.08) * mm});
            skLineSegment(sketch, "E9.6.6.3", {"start": v(1057.42, 1669.5) * mm, "end": v(1051.2, 1680.3) * mm});
            skLineSegment(sketch, "E9.9.6.3", {"start": v(1069.88, 1669.5) * mm, "end": v(1057.42, 1669.5) * mm});
            skLineSegment(sketch, "E9.12.6.3", {"start": v(1076.12, 1680.3) * mm, "end": v(1069.88, 1669.5) * mm});
            skLineSegment(sketch, "E9.15.6.3", {"start": v(1069.88, 1691.08) * mm, "end": v(1076.12, 1680.3) * mm});
            skLineSegment(sketch, "E9.0.6.4", {"start": v(1057.42, 1519.63) * mm, "end": v(1069.88, 1519.63) * mm});
            skLineSegment(sketch, "E9.3.6.4", {"start": v(1051.2, 1508.84) * mm, "end": v(1057.42, 1519.63) * mm});
            skLineSegment(sketch, "E9.6.6.4", {"start": v(1057.42, 1498.05) * mm, "end": v(1051.2, 1508.84) * mm});
            skLineSegment(sketch, "E9.9.6.4", {"start": v(1069.88, 1498.05) * mm, "end": v(1057.42, 1498.05) * mm});
            skLineSegment(sketch, "E9.12.6.4", {"start": v(1076.12, 1508.84) * mm, "end": v(1069.88, 1498.05) * mm});
            skLineSegment(sketch, "E9.15.6.4", {"start": v(1069.88, 1519.63) * mm, "end": v(1076.12, 1508.84) * mm});
            skLineSegment(sketch, "E9.0.6.5", {"start": v(1057.42, 1348.18) * mm, "end": v(1069.88, 1348.18) * mm});
            skLineSegment(sketch, "E9.3.6.5", {"start": v(1051.2, 1337.4) * mm, "end": v(1057.42, 1348.18) * mm});
            skLineSegment(sketch, "E9.6.6.5", {"start": v(1057.42, 1326.6) * mm, "end": v(1051.2, 1337.4) * mm});
            skLineSegment(sketch, "E9.9.6.5", {"start": v(1069.88, 1326.6) * mm, "end": v(1057.42, 1326.6) * mm});
            skLineSegment(sketch, "E9.12.6.5", {"start": v(1076.12, 1337.4) * mm, "end": v(1069.88, 1326.6) * mm});
            skLineSegment(sketch, "E9.15.6.5", {"start": v(1069.88, 1348.18) * mm, "end": v(1076.12, 1337.4) * mm});
            skLineSegment(sketch, "E9.0.6.6", {"start": v(1057.42, 1176.73) * mm, "end": v(1069.88, 1176.73) * mm});
            skLineSegment(sketch, "E9.3.6.6", {"start": v(1051.2, 1165.94) * mm, "end": v(1057.42, 1176.73) * mm});
            skLineSegment(sketch, "E9.6.6.6", {"start": v(1057.42, 1155.15) * mm, "end": v(1051.2, 1165.94) * mm});
            skLineSegment(sketch, "E9.9.6.6", {"start": v(1069.88, 1155.15) * mm, "end": v(1057.42, 1155.15) * mm});
            skLineSegment(sketch, "E9.12.6.6", {"start": v(1076.12, 1165.94) * mm, "end": v(1069.88, 1155.15) * mm});
            skLineSegment(sketch, "E9.15.6.6", {"start": v(1069.88, 1176.73) * mm, "end": v(1076.12, 1165.94) * mm});
            skLineSegment(sketch, "E9.0.6.7", {"start": v(1057.42, 1005.28) * mm, "end": v(1069.88, 1005.28) * mm});
            skLineSegment(sketch, "E9.3.6.7", {"start": v(1051.2, 994.5) * mm, "end": v(1057.42, 1005.28) * mm});
            skLineSegment(sketch, "E9.6.6.7", {"start": v(1057.42, 983.7) * mm, "end": v(1051.2, 994.5) * mm});
            skLineSegment(sketch, "E9.9.6.7", {"start": v(1069.88, 983.7) * mm, "end": v(1057.42, 983.7) * mm});
            skLineSegment(sketch, "E9.12.6.7", {"start": v(1076.12, 994.5) * mm, "end": v(1069.88, 983.7) * mm});
            skLineSegment(sketch, "E9.15.6.7", {"start": v(1069.88, 1005.28) * mm, "end": v(1076.12, 994.5) * mm});
            skLineSegment(sketch, "E9.0.7.0", {"start": v(1222.52, 2205.43) * mm, "end": v(1234.98, 2205.43) * mm});
            skLineSegment(sketch, "E9.3.7.0", {"start": v(1216.3, 2194.64) * mm, "end": v(1222.52, 2205.43) * mm});
            skLineSegment(sketch, "E9.6.7.0", {"start": v(1222.52, 2183.85) * mm, "end": v(1216.3, 2194.64) * mm});
            skLineSegment(sketch, "E9.9.7.0", {"start": v(1234.98, 2183.85) * mm, "end": v(1222.52, 2183.85) * mm});
            skLineSegment(sketch, "E9.12.7.0", {"start": v(1241.22, 2194.64) * mm, "end": v(1234.98, 2183.85) * mm});
            skLineSegment(sketch, "E9.15.7.0", {"start": v(1234.98, 2205.43) * mm, "end": v(1241.22, 2194.64) * mm});
            skLineSegment(sketch, "E9.0.7.1", {"start": v(1222.52, 2033.98) * mm, "end": v(1234.98, 2033.98) * mm});
            skLineSegment(sketch, "E9.3.7.1", {"start": v(1216.3, 2023.2) * mm, "end": v(1222.52, 2033.98) * mm});
            skLineSegment(sketch, "E9.6.7.1", {"start": v(1222.52, 2012.4) * mm, "end": v(1216.3, 2023.2) * mm});
            skLineSegment(sketch, "E9.9.7.1", {"start": v(1234.98, 2012.4) * mm, "end": v(1222.52, 2012.4) * mm});
            skLineSegment(sketch, "E9.12.7.1", {"start": v(1241.22, 2023.2) * mm, "end": v(1234.98, 2012.4) * mm});
            skLineSegment(sketch, "E9.15.7.1", {"start": v(1234.98, 2033.98) * mm, "end": v(1241.22, 2023.2) * mm});
            skLineSegment(sketch, "E9.0.7.2", {"start": v(1222.52, 1862.53) * mm, "end": v(1234.98, 1862.53) * mm});
            skLineSegment(sketch, "E9.3.7.2", {"start": v(1216.3, 1851.74) * mm, "end": v(1222.52, 1862.53) * mm});
            skLineSegment(sketch, "E9.6.7.2", {"start": v(1222.52, 1840.95) * mm, "end": v(1216.3, 1851.74) * mm});
            skLineSegment(sketch, "E9.9.7.2", {"start": v(1234.98, 1840.95) * mm, "end": v(1222.52, 1840.95) * mm});
            skLineSegment(sketch, "E9.12.7.2", {"start": v(1241.22, 1851.74) * mm, "end": v(1234.98, 1840.95) * mm});
            skLineSegment(sketch, "E9.15.7.2", {"start": v(1234.98, 1862.53) * mm, "end": v(1241.22, 1851.74) * mm});
            skLineSegment(sketch, "E9.0.7.3", {"start": v(1222.52, 1691.08) * mm, "end": v(1234.98, 1691.08) * mm});
            skLineSegment(sketch, "E9.3.7.3", {"start": v(1216.3, 1680.3) * mm, "end": v(1222.52, 1691.08) * mm});
            skLineSegment(sketch, "E9.6.7.3", {"start": v(1222.52, 1669.5) * mm, "end": v(1216.3, 1680.3) * mm});
            skLineSegment(sketch, "E9.9.7.3", {"start": v(1234.98, 1669.5) * mm, "end": v(1222.52, 1669.5) * mm});
            skLineSegment(sketch, "E9.12.7.3", {"start": v(1241.22, 1680.3) * mm, "end": v(1234.98, 1669.5) * mm});
            skLineSegment(sketch, "E9.15.7.3", {"start": v(1234.98, 1691.08) * mm, "end": v(1241.22, 1680.3) * mm});
            skLineSegment(sketch, "E9.0.7.4", {"start": v(1222.52, 1519.63) * mm, "end": v(1234.98, 1519.63) * mm});
            skLineSegment(sketch, "E9.3.7.4", {"start": v(1216.3, 1508.84) * mm, "end": v(1222.52, 1519.63) * mm});
            skLineSegment(sketch, "E9.6.7.4", {"start": v(1222.52, 1498.05) * mm, "end": v(1216.3, 1508.84) * mm});
            skLineSegment(sketch, "E9.9.7.4", {"start": v(1234.98, 1498.05) * mm, "end": v(1222.52, 1498.05) * mm});
            skLineSegment(sketch, "E9.12.7.4", {"start": v(1241.22, 1508.84) * mm, "end": v(1234.98, 1498.05) * mm});
            skLineSegment(sketch, "E9.15.7.4", {"start": v(1234.98, 1519.63) * mm, "end": v(1241.22, 1508.84) * mm});
            skLineSegment(sketch, "E9.0.7.5", {"start": v(1222.52, 1348.18) * mm, "end": v(1234.98, 1348.18) * mm});
            skLineSegment(sketch, "E9.3.7.5", {"start": v(1216.3, 1337.4) * mm, "end": v(1222.52, 1348.18) * mm});
            skLineSegment(sketch, "E9.6.7.5", {"start": v(1222.52, 1326.6) * mm, "end": v(1216.3, 1337.4) * mm});
            skLineSegment(sketch, "E9.9.7.5", {"start": v(1234.98, 1326.6) * mm, "end": v(1222.52, 1326.6) * mm});
            skLineSegment(sketch, "E9.12.7.5", {"start": v(1241.22, 1337.4) * mm, "end": v(1234.98, 1326.6) * mm});
            skLineSegment(sketch, "E9.15.7.5", {"start": v(1234.98, 1348.18) * mm, "end": v(1241.22, 1337.4) * mm});
            skLineSegment(sketch, "E9.0.7.6", {"start": v(1222.52, 1176.73) * mm, "end": v(1234.98, 1176.73) * mm});
            skLineSegment(sketch, "E9.3.7.6", {"start": v(1216.3, 1165.94) * mm, "end": v(1222.52, 1176.73) * mm});
            skLineSegment(sketch, "E9.6.7.6", {"start": v(1222.52, 1155.15) * mm, "end": v(1216.3, 1165.94) * mm});
            skLineSegment(sketch, "E9.9.7.6", {"start": v(1234.98, 1155.15) * mm, "end": v(1222.52, 1155.15) * mm});
            skLineSegment(sketch, "E9.12.7.6", {"start": v(1241.22, 1165.94) * mm, "end": v(1234.98, 1155.15) * mm});
            skLineSegment(sketch, "E9.15.7.6", {"start": v(1234.98, 1176.73) * mm, "end": v(1241.22, 1165.94) * mm});
            skLineSegment(sketch, "E9.0.7.7", {"start": v(1222.52, 1005.28) * mm, "end": v(1234.98, 1005.28) * mm});
            skLineSegment(sketch, "E9.3.7.7", {"start": v(1216.3, 994.5) * mm, "end": v(1222.52, 1005.28) * mm});
            skLineSegment(sketch, "E9.6.7.7", {"start": v(1222.52, 983.7) * mm, "end": v(1216.3, 994.5) * mm});
            skLineSegment(sketch, "E9.9.7.7", {"start": v(1234.98, 983.7) * mm, "end": v(1222.52, 983.7) * mm});
            skLineSegment(sketch, "E9.12.7.7", {"start": v(1241.22, 994.5) * mm, "end": v(1234.98, 983.7) * mm});
            skLineSegment(sketch, "E9.15.7.7", {"start": v(1234.98, 1005.28) * mm, "end": v(1241.22, 994.5) * mm});
            skLineSegment(sketch, "E9.0.8.0", {"start": v(1387.62, 2205.43) * mm, "end": v(1400.08, 2205.43) * mm});
            skLineSegment(sketch, "E9.3.8.0", {"start": v(1381.4, 2194.64) * mm, "end": v(1387.62, 2205.43) * mm});
            skLineSegment(sketch, "E9.6.8.0", {"start": v(1387.62, 2183.85) * mm, "end": v(1381.4, 2194.64) * mm});
            skLineSegment(sketch, "E9.9.8.0", {"start": v(1400.08, 2183.85) * mm, "end": v(1387.62, 2183.85) * mm});
            skLineSegment(sketch, "E9.12.8.0", {"start": v(1406.32, 2194.64) * mm, "end": v(1400.08, 2183.85) * mm});
            skLineSegment(sketch, "E9.15.8.0", {"start": v(1400.08, 2205.43) * mm, "end": v(1406.32, 2194.64) * mm});
            skLineSegment(sketch, "E9.0.8.1", {"start": v(1387.62, 2033.98) * mm, "end": v(1400.08, 2033.98) * mm});
            skLineSegment(sketch, "E9.3.8.1", {"start": v(1381.4, 2023.2) * mm, "end": v(1387.62, 2033.98) * mm});
            skLineSegment(sketch, "E9.6.8.1", {"start": v(1387.62, 2012.4) * mm, "end": v(1381.4, 2023.2) * mm});
            skLineSegment(sketch, "E9.9.8.1", {"start": v(1400.08, 2012.4) * mm, "end": v(1387.62, 2012.4) * mm});
            skLineSegment(sketch, "E9.12.8.1", {"start": v(1406.32, 2023.2) * mm, "end": v(1400.08, 2012.4) * mm});
            skLineSegment(sketch, "E9.15.8.1", {"start": v(1400.08, 2033.98) * mm, "end": v(1406.32, 2023.2) * mm});
            skLineSegment(sketch, "E9.0.8.2", {"start": v(1387.62, 1862.53) * mm, "end": v(1400.08, 1862.53) * mm});
            skLineSegment(sketch, "E9.3.8.2", {"start": v(1381.4, 1851.74) * mm, "end": v(1387.62, 1862.53) * mm});
            skLineSegment(sketch, "E9.6.8.2", {"start": v(1387.62, 1840.95) * mm, "end": v(1381.4, 1851.74) * mm});
            skLineSegment(sketch, "E9.9.8.2", {"start": v(1400.08, 1840.95) * mm, "end": v(1387.62, 1840.95) * mm});
            skLineSegment(sketch, "E9.12.8.2", {"start": v(1406.32, 1851.74) * mm, "end": v(1400.08, 1840.95) * mm});
            skLineSegment(sketch, "E9.15.8.2", {"start": v(1400.08, 1862.53) * mm, "end": v(1406.32, 1851.74) * mm});
            skLineSegment(sketch, "E9.0.8.3", {"start": v(1387.62, 1691.08) * mm, "end": v(1400.08, 1691.08) * mm});
            skLineSegment(sketch, "E9.3.8.3", {"start": v(1381.4, 1680.3) * mm, "end": v(1387.62, 1691.08) * mm});
            skLineSegment(sketch, "E9.6.8.3", {"start": v(1387.62, 1669.5) * mm, "end": v(1381.4, 1680.3) * mm});
            skLineSegment(sketch, "E9.9.8.3", {"start": v(1400.08, 1669.5) * mm, "end": v(1387.62, 1669.5) * mm});
            skLineSegment(sketch, "E9.12.8.3", {"start": v(1406.32, 1680.3) * mm, "end": v(1400.08, 1669.5) * mm});
            skLineSegment(sketch, "E9.15.8.3", {"start": v(1400.08, 1691.08) * mm, "end": v(1406.32, 1680.3) * mm});
            skLineSegment(sketch, "E9.0.8.4", {"start": v(1387.62, 1519.63) * mm, "end": v(1400.08, 1519.63) * mm});
            skLineSegment(sketch, "E9.3.8.4", {"start": v(1381.4, 1508.84) * mm, "end": v(1387.62, 1519.63) * mm});
            skLineSegment(sketch, "E9.6.8.4", {"start": v(1387.62, 1498.05) * mm, "end": v(1381.4, 1508.84) * mm});
            skLineSegment(sketch, "E9.9.8.4", {"start": v(1400.08, 1498.05) * mm, "end": v(1387.62, 1498.05) * mm});
            skLineSegment(sketch, "E9.12.8.4", {"start": v(1406.32, 1508.84) * mm, "end": v(1400.08, 1498.05) * mm});
            skLineSegment(sketch, "E9.15.8.4", {"start": v(1400.08, 1519.63) * mm, "end": v(1406.32, 1508.84) * mm});
            skLineSegment(sketch, "E9.0.8.5", {"start": v(1387.62, 1348.18) * mm, "end": v(1400.08, 1348.18) * mm});
            skLineSegment(sketch, "E9.3.8.5", {"start": v(1381.4, 1337.4) * mm, "end": v(1387.62, 1348.18) * mm});
            skLineSegment(sketch, "E9.6.8.5", {"start": v(1387.62, 1326.6) * mm, "end": v(1381.4, 1337.4) * mm});
            skLineSegment(sketch, "E9.9.8.5", {"start": v(1400.08, 1326.6) * mm, "end": v(1387.62, 1326.6) * mm});
            skLineSegment(sketch, "E9.12.8.5", {"start": v(1406.32, 1337.4) * mm, "end": v(1400.08, 1326.6) * mm});
            skLineSegment(sketch, "E9.15.8.5", {"start": v(1400.08, 1348.18) * mm, "end": v(1406.32, 1337.4) * mm});
            skLineSegment(sketch, "E9.0.8.6", {"start": v(1387.62, 1176.73) * mm, "end": v(1400.08, 1176.73) * mm});
            skLineSegment(sketch, "E9.3.8.6", {"start": v(1381.4, 1165.94) * mm, "end": v(1387.62, 1176.73) * mm});
            skLineSegment(sketch, "E9.6.8.6", {"start": v(1387.62, 1155.15) * mm, "end": v(1381.4, 1165.94) * mm});
            skLineSegment(sketch, "E9.9.8.6", {"start": v(1400.08, 1155.15) * mm, "end": v(1387.62, 1155.15) * mm});
            skLineSegment(sketch, "E9.12.8.6", {"start": v(1406.32, 1165.94) * mm, "end": v(1400.08, 1155.15) * mm});
            skLineSegment(sketch, "E9.15.8.6", {"start": v(1400.08, 1176.73) * mm, "end": v(1406.32, 1165.94) * mm});
            skLineSegment(sketch, "E9.0.8.7", {"start": v(1387.62, 1005.28) * mm, "end": v(1400.08, 1005.28) * mm});
            skLineSegment(sketch, "E9.3.8.7", {"start": v(1381.4, 994.5) * mm, "end": v(1387.62, 1005.28) * mm});
            skLineSegment(sketch, "E9.6.8.7", {"start": v(1387.62, 983.7) * mm, "end": v(1381.4, 994.5) * mm});
            skLineSegment(sketch, "E9.9.8.7", {"start": v(1400.08, 983.7) * mm, "end": v(1387.62, 983.7) * mm});
            skLineSegment(sketch, "E9.12.8.7", {"start": v(1406.32, 994.5) * mm, "end": v(1400.08, 983.7) * mm});
            skLineSegment(sketch, "E9.15.8.7", {"start": v(1400.08, 1005.28) * mm, "end": v(1406.32, 994.5) * mm});
            skLineSegment(sketch, "E9.0.9.0", {"start": v(1552.72, 2205.43) * mm, "end": v(1565.18, 2205.43) * mm});
            skLineSegment(sketch, "E9.3.9.0", {"start": v(1546.5, 2194.64) * mm, "end": v(1552.72, 2205.43) * mm});
            skLineSegment(sketch, "E9.6.9.0", {"start": v(1552.72, 2183.85) * mm, "end": v(1546.5, 2194.64) * mm});
            skLineSegment(sketch, "E9.9.9.0", {"start": v(1565.18, 2183.85) * mm, "end": v(1552.72, 2183.85) * mm});
            skLineSegment(sketch, "E9.12.9.0", {"start": v(1571.42, 2194.64) * mm, "end": v(1565.18, 2183.85) * mm});
            skLineSegment(sketch, "E9.15.9.0", {"start": v(1565.18, 2205.43) * mm, "end": v(1571.42, 2194.64) * mm});
            skLineSegment(sketch, "E9.0.9.1", {"start": v(1552.72, 2033.98) * mm, "end": v(1565.18, 2033.98) * mm});
            skLineSegment(sketch, "E9.3.9.1", {"start": v(1546.5, 2023.2) * mm, "end": v(1552.72, 2033.98) * mm});
            skLineSegment(sketch, "E9.6.9.1", {"start": v(1552.72, 2012.4) * mm, "end": v(1546.5, 2023.2) * mm});
            skLineSegment(sketch, "E9.9.9.1", {"start": v(1565.18, 2012.4) * mm, "end": v(1552.72, 2012.4) * mm});
            skLineSegment(sketch, "E9.12.9.1", {"start": v(1571.42, 2023.2) * mm, "end": v(1565.18, 2012.4) * mm});
            skLineSegment(sketch, "E9.15.9.1", {"start": v(1565.18, 2033.98) * mm, "end": v(1571.42, 2023.2) * mm});
            skLineSegment(sketch, "E9.0.9.2", {"start": v(1552.72, 1862.53) * mm, "end": v(1565.18, 1862.53) * mm});
            skLineSegment(sketch, "E9.3.9.2", {"start": v(1546.5, 1851.74) * mm, "end": v(1552.72, 1862.53) * mm});
            skLineSegment(sketch, "E9.6.9.2", {"start": v(1552.72, 1840.95) * mm, "end": v(1546.5, 1851.74) * mm});
            skLineSegment(sketch, "E9.9.9.2", {"start": v(1565.18, 1840.95) * mm, "end": v(1552.72, 1840.95) * mm});
            skLineSegment(sketch, "E9.12.9.2", {"start": v(1571.42, 1851.74) * mm, "end": v(1565.18, 1840.95) * mm});
            skLineSegment(sketch, "E9.15.9.2", {"start": v(1565.18, 1862.53) * mm, "end": v(1571.42, 1851.74) * mm});
            skLineSegment(sketch, "E9.0.9.3", {"start": v(1552.72, 1691.08) * mm, "end": v(1565.18, 1691.08) * mm});
            skLineSegment(sketch, "E9.3.9.3", {"start": v(1546.5, 1680.3) * mm, "end": v(1552.72, 1691.08) * mm});
            skLineSegment(sketch, "E9.6.9.3", {"start": v(1552.72, 1669.5) * mm, "end": v(1546.5, 1680.3) * mm});
            skLineSegment(sketch, "E9.9.9.3", {"start": v(1565.18, 1669.5) * mm, "end": v(1552.72, 1669.5) * mm});
            skLineSegment(sketch, "E9.12.9.3", {"start": v(1571.42, 1680.3) * mm, "end": v(1565.18, 1669.5) * mm});
            skLineSegment(sketch, "E9.15.9.3", {"start": v(1565.18, 1691.08) * mm, "end": v(1571.42, 1680.3) * mm});
            skLineSegment(sketch, "E9.0.9.4", {"start": v(1552.72, 1519.63) * mm, "end": v(1565.18, 1519.63) * mm});
            skLineSegment(sketch, "E9.3.9.4", {"start": v(1546.5, 1508.84) * mm, "end": v(1552.72, 1519.63) * mm});
            skLineSegment(sketch, "E9.6.9.4", {"start": v(1552.72, 1498.05) * mm, "end": v(1546.5, 1508.84) * mm});
            skLineSegment(sketch, "E9.9.9.4", {"start": v(1565.18, 1498.05) * mm, "end": v(1552.72, 1498.05) * mm});
            skLineSegment(sketch, "E9.12.9.4", {"start": v(1571.42, 1508.84) * mm, "end": v(1565.18, 1498.05) * mm});
            skLineSegment(sketch, "E9.15.9.4", {"start": v(1565.18, 1519.63) * mm, "end": v(1571.42, 1508.84) * mm});
            skLineSegment(sketch, "E9.0.9.5", {"start": v(1552.72, 1348.18) * mm, "end": v(1565.18, 1348.18) * mm});
            skLineSegment(sketch, "E9.3.9.5", {"start": v(1546.5, 1337.4) * mm, "end": v(1552.72, 1348.18) * mm});
            skLineSegment(sketch, "E9.6.9.5", {"start": v(1552.72, 1326.6) * mm, "end": v(1546.5, 1337.4) * mm});
            skLineSegment(sketch, "E9.9.9.5", {"start": v(1565.18, 1326.6) * mm, "end": v(1552.72, 1326.6) * mm});
            skLineSegment(sketch, "E9.12.9.5", {"start": v(1571.42, 1337.4) * mm, "end": v(1565.18, 1326.6) * mm});
            skLineSegment(sketch, "E9.15.9.5", {"start": v(1565.18, 1348.18) * mm, "end": v(1571.42, 1337.4) * mm});
            skLineSegment(sketch, "E9.0.9.6", {"start": v(1552.72, 1176.73) * mm, "end": v(1565.18, 1176.73) * mm});
            skLineSegment(sketch, "E9.3.9.6", {"start": v(1546.5, 1165.94) * mm, "end": v(1552.72, 1176.73) * mm});
            skLineSegment(sketch, "E9.6.9.6", {"start": v(1552.72, 1155.15) * mm, "end": v(1546.5, 1165.94) * mm});
            skLineSegment(sketch, "E9.9.9.6", {"start": v(1565.18, 1155.15) * mm, "end": v(1552.72, 1155.15) * mm});
            skLineSegment(sketch, "E9.12.9.6", {"start": v(1571.42, 1165.94) * mm, "end": v(1565.18, 1155.15) * mm});
            skLineSegment(sketch, "E9.15.9.6", {"start": v(1565.18, 1176.73) * mm, "end": v(1571.42, 1165.94) * mm});
            skLineSegment(sketch, "E9.0.9.7", {"start": v(1552.72, 1005.28) * mm, "end": v(1565.18, 1005.28) * mm});
            skLineSegment(sketch, "E9.3.9.7", {"start": v(1546.5, 994.5) * mm, "end": v(1552.72, 1005.28) * mm});
            skLineSegment(sketch, "E9.6.9.7", {"start": v(1552.72, 983.7) * mm, "end": v(1546.5, 994.5) * mm});
            skLineSegment(sketch, "E9.9.9.7", {"start": v(1565.18, 983.7) * mm, "end": v(1552.72, 983.7) * mm});
            skLineSegment(sketch, "E9.12.9.7", {"start": v(1571.42, 994.5) * mm, "end": v(1565.18, 983.7) * mm});
            skLineSegment(sketch, "E9.15.9.7", {"start": v(1565.18, 1005.28) * mm, "end": v(1571.42, 994.5) * mm});
            skLineSegment(sketch, "E10.0.0.8", {"start": v(66.82, 833.83) * mm, "end": v(79.28, 833.83) * mm});
            skLineSegment(sketch, "E10.3.0.8", {"start": v(60.6, 823.04) * mm, "end": v(66.82, 833.83) * mm});
            skLineSegment(sketch, "E10.6.0.8", {"start": v(66.82, 812.25) * mm, "end": v(60.6, 823.04) * mm});
            skLineSegment(sketch, "E10.9.0.8", {"start": v(79.28, 812.25) * mm, "end": v(66.82, 812.25) * mm});
            skLineSegment(sketch, "E10.12.0.8", {"start": v(85.52, 823.04) * mm, "end": v(79.28, 812.25) * mm});
            skLineSegment(sketch, "E10.15.0.8", {"start": v(79.28, 833.83) * mm, "end": v(85.52, 823.04) * mm});
            skLineSegment(sketch, "E10.0.0.9", {"start": v(66.82, 662.38) * mm, "end": v(79.28, 662.38) * mm});
            skLineSegment(sketch, "E10.3.0.9", {"start": v(60.6, 651.6) * mm, "end": v(66.82, 662.38) * mm});
            skLineSegment(sketch, "E10.6.0.9", {"start": v(66.82, 640.8) * mm, "end": v(60.6, 651.6) * mm});
            skLineSegment(sketch, "E10.9.0.9", {"start": v(79.28, 640.8) * mm, "end": v(66.82, 640.8) * mm});
            skLineSegment(sketch, "E10.12.0.9", {"start": v(85.52, 651.6) * mm, "end": v(79.28, 640.8) * mm});
            skLineSegment(sketch, "E10.15.0.9", {"start": v(79.28, 662.38) * mm, "end": v(85.52, 651.6) * mm});
            skLineSegment(sketch, "E10.0.0.10", {"start": v(66.82, 490.93) * mm, "end": v(79.28, 490.93) * mm});
            skLineSegment(sketch, "E10.3.0.10", {"start": v(60.6, 480.14) * mm, "end": v(66.82, 490.93) * mm});
            skLineSegment(sketch, "E10.6.0.10", {"start": v(66.82, 469.35) * mm, "end": v(60.6, 480.14) * mm});
            skLineSegment(sketch, "E10.9.0.10", {"start": v(79.28, 469.35) * mm, "end": v(66.82, 469.35) * mm});
            skLineSegment(sketch, "E10.12.0.10", {"start": v(85.52, 480.14) * mm, "end": v(79.28, 469.35) * mm});
            skLineSegment(sketch, "E10.15.0.10", {"start": v(79.28, 490.93) * mm, "end": v(85.52, 480.14) * mm});
            skLineSegment(sketch, "E10.0.0.11", {"start": v(66.82, 319.48) * mm, "end": v(79.28, 319.48) * mm});
            skLineSegment(sketch, "E10.3.0.11", {"start": v(60.6, 308.7) * mm, "end": v(66.82, 319.48) * mm});
            skLineSegment(sketch, "E10.6.0.11", {"start": v(66.82, 297.9) * mm, "end": v(60.6, 308.7) * mm});
            skLineSegment(sketch, "E10.9.0.11", {"start": v(79.28, 297.9) * mm, "end": v(66.82, 297.9) * mm});
            skLineSegment(sketch, "E10.12.0.11", {"start": v(85.52, 308.7) * mm, "end": v(79.28, 297.9) * mm});
            skLineSegment(sketch, "E10.15.0.11", {"start": v(79.28, 319.48) * mm, "end": v(85.52, 308.7) * mm});
            skLineSegment(sketch, "E10.0.1.8", {"start": v(231.92, 833.83) * mm, "end": v(244.38, 833.83) * mm});
            skLineSegment(sketch, "E10.3.1.8", {"start": v(225.7, 823.04) * mm, "end": v(231.92, 833.83) * mm});
            skLineSegment(sketch, "E10.6.1.8", {"start": v(231.92, 812.25) * mm, "end": v(225.7, 823.04) * mm});
            skLineSegment(sketch, "E10.9.1.8", {"start": v(244.38, 812.25) * mm, "end": v(231.92, 812.25) * mm});
            skLineSegment(sketch, "E10.12.1.8", {"start": v(250.62, 823.04) * mm, "end": v(244.38, 812.25) * mm});
            skLineSegment(sketch, "E10.15.1.8", {"start": v(244.38, 833.83) * mm, "end": v(250.62, 823.04) * mm});
            skLineSegment(sketch, "E10.0.1.9", {"start": v(231.92, 662.38) * mm, "end": v(244.38, 662.38) * mm});
            skLineSegment(sketch, "E10.3.1.9", {"start": v(225.7, 651.6) * mm, "end": v(231.92, 662.38) * mm});
            skLineSegment(sketch, "E10.6.1.9", {"start": v(231.92, 640.8) * mm, "end": v(225.7, 651.6) * mm});
            skLineSegment(sketch, "E10.9.1.9", {"start": v(244.38, 640.8) * mm, "end": v(231.92, 640.8) * mm});
            skLineSegment(sketch, "E10.12.1.9", {"start": v(250.62, 651.6) * mm, "end": v(244.38, 640.8) * mm});
            skLineSegment(sketch, "E10.15.1.9", {"start": v(244.38, 662.38) * mm, "end": v(250.62, 651.6) * mm});
            skLineSegment(sketch, "E10.0.1.10", {"start": v(231.92, 490.93) * mm, "end": v(244.38, 490.93) * mm});
            skLineSegment(sketch, "E10.3.1.10", {"start": v(225.7, 480.14) * mm, "end": v(231.92, 490.93) * mm});
            skLineSegment(sketch, "E10.6.1.10", {"start": v(231.92, 469.35) * mm, "end": v(225.7, 480.14) * mm});
            skLineSegment(sketch, "E10.9.1.10", {"start": v(244.38, 469.35) * mm, "end": v(231.92, 469.35) * mm});
            skLineSegment(sketch, "E10.12.1.10", {"start": v(250.62, 480.14) * mm, "end": v(244.38, 469.35) * mm});
            skLineSegment(sketch, "E10.15.1.10", {"start": v(244.38, 490.93) * mm, "end": v(250.62, 480.14) * mm});
            skLineSegment(sketch, "E10.0.1.11", {"start": v(231.92, 319.48) * mm, "end": v(244.38, 319.48) * mm});
            skLineSegment(sketch, "E10.3.1.11", {"start": v(225.7, 308.7) * mm, "end": v(231.92, 319.48) * mm});
            skLineSegment(sketch, "E10.6.1.11", {"start": v(231.92, 297.9) * mm, "end": v(225.7, 308.7) * mm});
            skLineSegment(sketch, "E10.9.1.11", {"start": v(244.38, 297.9) * mm, "end": v(231.92, 297.9) * mm});
            skLineSegment(sketch, "E10.12.1.11", {"start": v(250.62, 308.7) * mm, "end": v(244.38, 297.9) * mm});
            skLineSegment(sketch, "E10.15.1.11", {"start": v(244.38, 319.48) * mm, "end": v(250.62, 308.7) * mm});
            skLineSegment(sketch, "E10.0.2.8", {"start": v(397.02, 833.83) * mm, "end": v(409.48, 833.83) * mm});
            skLineSegment(sketch, "E10.3.2.8", {"start": v(390.8, 823.04) * mm, "end": v(397.02, 833.83) * mm});
            skLineSegment(sketch, "E10.6.2.8", {"start": v(397.02, 812.25) * mm, "end": v(390.8, 823.04) * mm});
            skLineSegment(sketch, "E10.9.2.8", {"start": v(409.48, 812.25) * mm, "end": v(397.02, 812.25) * mm});
            skLineSegment(sketch, "E10.12.2.8", {"start": v(415.72, 823.04) * mm, "end": v(409.48, 812.25) * mm});
            skLineSegment(sketch, "E10.15.2.8", {"start": v(409.48, 833.83) * mm, "end": v(415.72, 823.04) * mm});
            skLineSegment(sketch, "E10.0.2.9", {"start": v(397.02, 662.38) * mm, "end": v(409.48, 662.38) * mm});
            skLineSegment(sketch, "E10.3.2.9", {"start": v(390.8, 651.6) * mm, "end": v(397.02, 662.38) * mm});
            skLineSegment(sketch, "E10.6.2.9", {"start": v(397.02, 640.8) * mm, "end": v(390.8, 651.6) * mm});
            skLineSegment(sketch, "E10.9.2.9", {"start": v(409.48, 640.8) * mm, "end": v(397.02, 640.8) * mm});
            skLineSegment(sketch, "E10.12.2.9", {"start": v(415.72, 651.6) * mm, "end": v(409.48, 640.8) * mm});
            skLineSegment(sketch, "E10.15.2.9", {"start": v(409.48, 662.38) * mm, "end": v(415.72, 651.6) * mm});
            skLineSegment(sketch, "E10.0.2.10", {"start": v(397.02, 490.93) * mm, "end": v(409.48, 490.93) * mm});
            skLineSegment(sketch, "E10.3.2.10", {"start": v(390.8, 480.14) * mm, "end": v(397.02, 490.93) * mm});
            skLineSegment(sketch, "E10.6.2.10", {"start": v(397.02, 469.35) * mm, "end": v(390.8, 480.14) * mm});
            skLineSegment(sketch, "E10.9.2.10", {"start": v(409.48, 469.35) * mm, "end": v(397.02, 469.35) * mm});
            skLineSegment(sketch, "E10.12.2.10", {"start": v(415.72, 480.14) * mm, "end": v(409.48, 469.35) * mm});
            skLineSegment(sketch, "E10.15.2.10", {"start": v(409.48, 490.93) * mm, "end": v(415.72, 480.14) * mm});
            skLineSegment(sketch, "E10.0.2.11", {"start": v(397.02, 319.48) * mm, "end": v(409.48, 319.48) * mm});
            skLineSegment(sketch, "E10.3.2.11", {"start": v(390.8, 308.7) * mm, "end": v(397.02, 319.48) * mm});
            skLineSegment(sketch, "E10.6.2.11", {"start": v(397.02, 297.9) * mm, "end": v(390.8, 308.7) * mm});
            skLineSegment(sketch, "E10.9.2.11", {"start": v(409.48, 297.9) * mm, "end": v(397.02, 297.9) * mm});
            skLineSegment(sketch, "E10.12.2.11", {"start": v(415.72, 308.7) * mm, "end": v(409.48, 297.9) * mm});
            skLineSegment(sketch, "E10.15.2.11", {"start": v(409.48, 319.48) * mm, "end": v(415.72, 308.7) * mm});
            skLineSegment(sketch, "E10.0.3.8", {"start": v(562.12, 833.83) * mm, "end": v(574.58, 833.83) * mm});
            skLineSegment(sketch, "E10.3.3.8", {"start": v(555.9, 823.04) * mm, "end": v(562.12, 833.83) * mm});
            skLineSegment(sketch, "E10.6.3.8", {"start": v(562.12, 812.25) * mm, "end": v(555.9, 823.04) * mm});
            skLineSegment(sketch, "E10.9.3.8", {"start": v(574.58, 812.25) * mm, "end": v(562.12, 812.25) * mm});
            skLineSegment(sketch, "E10.12.3.8", {"start": v(580.82, 823.04) * mm, "end": v(574.58, 812.25) * mm});
            skLineSegment(sketch, "E10.15.3.8", {"start": v(574.58, 833.83) * mm, "end": v(580.82, 823.04) * mm});
            skLineSegment(sketch, "E10.0.3.9", {"start": v(562.12, 662.38) * mm, "end": v(574.58, 662.38) * mm});
            skLineSegment(sketch, "E10.3.3.9", {"start": v(555.9, 651.6) * mm, "end": v(562.12, 662.38) * mm});
            skLineSegment(sketch, "E10.6.3.9", {"start": v(562.12, 640.8) * mm, "end": v(555.9, 651.6) * mm});
            skLineSegment(sketch, "E10.9.3.9", {"start": v(574.58, 640.8) * mm, "end": v(562.12, 640.8) * mm});
            skLineSegment(sketch, "E10.12.3.9", {"start": v(580.82, 651.6) * mm, "end": v(574.58, 640.8) * mm});
            skLineSegment(sketch, "E10.15.3.9", {"start": v(574.58, 662.38) * mm, "end": v(580.82, 651.6) * mm});
            skLineSegment(sketch, "E10.0.3.10", {"start": v(562.12, 490.93) * mm, "end": v(574.58, 490.93) * mm});
            skLineSegment(sketch, "E10.3.3.10", {"start": v(555.9, 480.14) * mm, "end": v(562.12, 490.93) * mm});
            skLineSegment(sketch, "E10.6.3.10", {"start": v(562.12, 469.35) * mm, "end": v(555.9, 480.14) * mm});
            skLineSegment(sketch, "E10.9.3.10", {"start": v(574.58, 469.35) * mm, "end": v(562.12, 469.35) * mm});
            skLineSegment(sketch, "E10.12.3.10", {"start": v(580.82, 480.14) * mm, "end": v(574.58, 469.35) * mm});
            skLineSegment(sketch, "E10.15.3.10", {"start": v(574.58, 490.93) * mm, "end": v(580.82, 480.14) * mm});
            skLineSegment(sketch, "E10.0.3.11", {"start": v(562.12, 319.48) * mm, "end": v(574.58, 319.48) * mm});
            skLineSegment(sketch, "E10.3.3.11", {"start": v(555.9, 308.7) * mm, "end": v(562.12, 319.48) * mm});
            skLineSegment(sketch, "E10.6.3.11", {"start": v(562.12, 297.9) * mm, "end": v(555.9, 308.7) * mm});
            skLineSegment(sketch, "E10.9.3.11", {"start": v(574.58, 297.9) * mm, "end": v(562.12, 297.9) * mm});
            skLineSegment(sketch, "E10.12.3.11", {"start": v(580.82, 308.7) * mm, "end": v(574.58, 297.9) * mm});
            skLineSegment(sketch, "E10.15.3.11", {"start": v(574.58, 319.48) * mm, "end": v(580.82, 308.7) * mm});
            skLineSegment(sketch, "E10.0.4.8", {"start": v(727.22, 833.83) * mm, "end": v(739.68, 833.83) * mm});
            skLineSegment(sketch, "E10.3.4.8", {"start": v(721, 823.04) * mm, "end": v(727.22, 833.83) * mm});
            skLineSegment(sketch, "E10.6.4.8", {"start": v(727.22, 812.25) * mm, "end": v(721, 823.04) * mm});
            skLineSegment(sketch, "E10.9.4.8", {"start": v(739.68, 812.25) * mm, "end": v(727.22, 812.25) * mm});
            skLineSegment(sketch, "E10.12.4.8", {"start": v(745.92, 823.04) * mm, "end": v(739.68, 812.25) * mm});
            skLineSegment(sketch, "E10.15.4.8", {"start": v(739.68, 833.83) * mm, "end": v(745.92, 823.04) * mm});
            skLineSegment(sketch, "E10.0.4.9", {"start": v(727.22, 662.38) * mm, "end": v(739.68, 662.38) * mm});
            skLineSegment(sketch, "E10.3.4.9", {"start": v(721, 651.6) * mm, "end": v(727.22, 662.38) * mm});
            skLineSegment(sketch, "E10.6.4.9", {"start": v(727.22, 640.8) * mm, "end": v(721, 651.6) * mm});
            skLineSegment(sketch, "E10.9.4.9", {"start": v(739.68, 640.8) * mm, "end": v(727.22, 640.8) * mm});
            skLineSegment(sketch, "E10.12.4.9", {"start": v(745.92, 651.6) * mm, "end": v(739.68, 640.8) * mm});
            skLineSegment(sketch, "E10.15.4.9", {"start": v(739.68, 662.38) * mm, "end": v(745.92, 651.6) * mm});
            skLineSegment(sketch, "E10.0.4.10", {"start": v(727.22, 490.93) * mm, "end": v(739.68, 490.93) * mm});
            skLineSegment(sketch, "E10.3.4.10", {"start": v(721, 480.14) * mm, "end": v(727.22, 490.93) * mm});
            skLineSegment(sketch, "E10.6.4.10", {"start": v(727.22, 469.35) * mm, "end": v(721, 480.14) * mm});
            skLineSegment(sketch, "E10.9.4.10", {"start": v(739.68, 469.35) * mm, "end": v(727.22, 469.35) * mm});
            skLineSegment(sketch, "E10.12.4.10", {"start": v(745.92, 480.14) * mm, "end": v(739.68, 469.35) * mm});
            skLineSegment(sketch, "E10.15.4.10", {"start": v(739.68, 490.93) * mm, "end": v(745.92, 480.14) * mm});
            skLineSegment(sketch, "E10.0.4.11", {"start": v(727.22, 319.48) * mm, "end": v(739.68, 319.48) * mm});
            skLineSegment(sketch, "E10.3.4.11", {"start": v(721, 308.7) * mm, "end": v(727.22, 319.48) * mm});
            skLineSegment(sketch, "E10.6.4.11", {"start": v(727.22, 297.9) * mm, "end": v(721, 308.7) * mm});
            skLineSegment(sketch, "E10.9.4.11", {"start": v(739.68, 297.9) * mm, "end": v(727.22, 297.9) * mm});
            skLineSegment(sketch, "E10.12.4.11", {"start": v(745.92, 308.7) * mm, "end": v(739.68, 297.9) * mm});
            skLineSegment(sketch, "E10.15.4.11", {"start": v(739.68, 319.48) * mm, "end": v(745.92, 308.7) * mm});
            skLineSegment(sketch, "E10.0.5.8", {"start": v(892.32, 833.83) * mm, "end": v(904.78, 833.83) * mm});
            skLineSegment(sketch, "E10.3.5.8", {"start": v(886.1, 823.04) * mm, "end": v(892.32, 833.83) * mm});
            skLineSegment(sketch, "E10.6.5.8", {"start": v(892.32, 812.25) * mm, "end": v(886.1, 823.04) * mm});
            skLineSegment(sketch, "E10.9.5.8", {"start": v(904.78, 812.25) * mm, "end": v(892.32, 812.25) * mm});
            skLineSegment(sketch, "E10.12.5.8", {"start": v(911.02, 823.04) * mm, "end": v(904.78, 812.25) * mm});
            skLineSegment(sketch, "E10.15.5.8", {"start": v(904.78, 833.83) * mm, "end": v(911.02, 823.04) * mm});
            skLineSegment(sketch, "E10.0.5.9", {"start": v(892.32, 662.38) * mm, "end": v(904.78, 662.38) * mm});
            skLineSegment(sketch, "E10.3.5.9", {"start": v(886.1, 651.6) * mm, "end": v(892.32, 662.38) * mm});
            skLineSegment(sketch, "E10.6.5.9", {"start": v(892.32, 640.8) * mm, "end": v(886.1, 651.6) * mm});
            skLineSegment(sketch, "E10.9.5.9", {"start": v(904.78, 640.8) * mm, "end": v(892.32, 640.8) * mm});
            skLineSegment(sketch, "E10.12.5.9", {"start": v(911.02, 651.6) * mm, "end": v(904.78, 640.8) * mm});
            skLineSegment(sketch, "E10.15.5.9", {"start": v(904.78, 662.38) * mm, "end": v(911.02, 651.6) * mm});
            skLineSegment(sketch, "E10.0.5.10", {"start": v(892.32, 490.93) * mm, "end": v(904.78, 490.93) * mm});
            skLineSegment(sketch, "E10.3.5.10", {"start": v(886.1, 480.14) * mm, "end": v(892.32, 490.93) * mm});
            skLineSegment(sketch, "E10.6.5.10", {"start": v(892.32, 469.35) * mm, "end": v(886.1, 480.14) * mm});
            skLineSegment(sketch, "E10.9.5.10", {"start": v(904.78, 469.35) * mm, "end": v(892.32, 469.35) * mm});
            skLineSegment(sketch, "E10.12.5.10", {"start": v(911.02, 480.14) * mm, "end": v(904.78, 469.35) * mm});
            skLineSegment(sketch, "E10.15.5.10", {"start": v(904.78, 490.93) * mm, "end": v(911.02, 480.14) * mm});
            skLineSegment(sketch, "E10.0.5.11", {"start": v(892.32, 319.48) * mm, "end": v(904.78, 319.48) * mm});
            skLineSegment(sketch, "E10.3.5.11", {"start": v(886.1, 308.7) * mm, "end": v(892.32, 319.48) * mm});
            skLineSegment(sketch, "E10.6.5.11", {"start": v(892.32, 297.9) * mm, "end": v(886.1, 308.7) * mm});
            skLineSegment(sketch, "E10.9.5.11", {"start": v(904.78, 297.9) * mm, "end": v(892.32, 297.9) * mm});
            skLineSegment(sketch, "E10.12.5.11", {"start": v(911.02, 308.7) * mm, "end": v(904.78, 297.9) * mm});
            skLineSegment(sketch, "E10.15.5.11", {"start": v(904.78, 319.48) * mm, "end": v(911.02, 308.7) * mm});
            skLineSegment(sketch, "E10.0.6.8", {"start": v(1057.42, 833.83) * mm, "end": v(1069.88, 833.83) * mm});
            skLineSegment(sketch, "E10.3.6.8", {"start": v(1051.2, 823.04) * mm, "end": v(1057.42, 833.83) * mm});
            skLineSegment(sketch, "E10.6.6.8", {"start": v(1057.42, 812.25) * mm, "end": v(1051.2, 823.04) * mm});
            skLineSegment(sketch, "E10.9.6.8", {"start": v(1069.88, 812.25) * mm, "end": v(1057.42, 812.25) * mm});
            skLineSegment(sketch, "E10.12.6.8", {"start": v(1076.12, 823.04) * mm, "end": v(1069.88, 812.25) * mm});
            skLineSegment(sketch, "E10.15.6.8", {"start": v(1069.88, 833.83) * mm, "end": v(1076.12, 823.04) * mm});
            skLineSegment(sketch, "E10.0.6.9", {"start": v(1057.42, 662.38) * mm, "end": v(1069.88, 662.38) * mm});
            skLineSegment(sketch, "E10.3.6.9", {"start": v(1051.2, 651.6) * mm, "end": v(1057.42, 662.38) * mm});
            skLineSegment(sketch, "E10.6.6.9", {"start": v(1057.42, 640.8) * mm, "end": v(1051.2, 651.6) * mm});
            skLineSegment(sketch, "E10.9.6.9", {"start": v(1069.88, 640.8) * mm, "end": v(1057.42, 640.8) * mm});
            skLineSegment(sketch, "E10.12.6.9", {"start": v(1076.12, 651.6) * mm, "end": v(1069.88, 640.8) * mm});
            skLineSegment(sketch, "E10.15.6.9", {"start": v(1069.88, 662.38) * mm, "end": v(1076.12, 651.6) * mm});
            skLineSegment(sketch, "E10.0.6.10", {"start": v(1057.42, 490.93) * mm, "end": v(1069.88, 490.93) * mm});
            skLineSegment(sketch, "E10.3.6.10", {"start": v(1051.2, 480.14) * mm, "end": v(1057.42, 490.93) * mm});
            skLineSegment(sketch, "E10.6.6.10", {"start": v(1057.42, 469.35) * mm, "end": v(1051.2, 480.14) * mm});
            skLineSegment(sketch, "E10.9.6.10", {"start": v(1069.88, 469.35) * mm, "end": v(1057.42, 469.35) * mm});
            skLineSegment(sketch, "E10.12.6.10", {"start": v(1076.12, 480.14) * mm, "end": v(1069.88, 469.35) * mm});
            skLineSegment(sketch, "E10.15.6.10", {"start": v(1069.88, 490.93) * mm, "end": v(1076.12, 480.14) * mm});
            skLineSegment(sketch, "E10.0.6.11", {"start": v(1057.42, 319.48) * mm, "end": v(1069.88, 319.48) * mm});
            skLineSegment(sketch, "E10.3.6.11", {"start": v(1051.2, 308.7) * mm, "end": v(1057.42, 319.48) * mm});
            skLineSegment(sketch, "E10.6.6.11", {"start": v(1057.42, 297.9) * mm, "end": v(1051.2, 308.7) * mm});
            skLineSegment(sketch, "E10.9.6.11", {"start": v(1069.88, 297.9) * mm, "end": v(1057.42, 297.9) * mm});
            skLineSegment(sketch, "E10.12.6.11", {"start": v(1076.12, 308.7) * mm, "end": v(1069.88, 297.9) * mm});
            skLineSegment(sketch, "E10.15.6.11", {"start": v(1069.88, 319.48) * mm, "end": v(1076.12, 308.7) * mm});
            skLineSegment(sketch, "E10.0.7.8", {"start": v(1222.52, 833.83) * mm, "end": v(1234.98, 833.83) * mm});
            skLineSegment(sketch, "E10.3.7.8", {"start": v(1216.3, 823.04) * mm, "end": v(1222.52, 833.83) * mm});
            skLineSegment(sketch, "E10.6.7.8", {"start": v(1222.52, 812.25) * mm, "end": v(1216.3, 823.04) * mm});
            skLineSegment(sketch, "E10.9.7.8", {"start": v(1234.98, 812.25) * mm, "end": v(1222.52, 812.25) * mm});
            skLineSegment(sketch, "E10.12.7.8", {"start": v(1241.22, 823.04) * mm, "end": v(1234.98, 812.25) * mm});
            skLineSegment(sketch, "E10.15.7.8", {"start": v(1234.98, 833.83) * mm, "end": v(1241.22, 823.04) * mm});
            skLineSegment(sketch, "E10.0.7.9", {"start": v(1222.52, 662.38) * mm, "end": v(1234.98, 662.38) * mm});
            skLineSegment(sketch, "E10.3.7.9", {"start": v(1216.3, 651.6) * mm, "end": v(1222.52, 662.38) * mm});
            skLineSegment(sketch, "E10.6.7.9", {"start": v(1222.52, 640.8) * mm, "end": v(1216.3, 651.6) * mm});
            skLineSegment(sketch, "E10.9.7.9", {"start": v(1234.98, 640.8) * mm, "end": v(1222.52, 640.8) * mm});
            skLineSegment(sketch, "E10.12.7.9", {"start": v(1241.22, 651.6) * mm, "end": v(1234.98, 640.8) * mm});
            skLineSegment(sketch, "E10.15.7.9", {"start": v(1234.98, 662.38) * mm, "end": v(1241.22, 651.6) * mm});
            skLineSegment(sketch, "E10.0.7.10", {"start": v(1222.52, 490.93) * mm, "end": v(1234.98, 490.93) * mm});
            skLineSegment(sketch, "E10.3.7.10", {"start": v(1216.3, 480.14) * mm, "end": v(1222.52, 490.93) * mm});
            skLineSegment(sketch, "E10.6.7.10", {"start": v(1222.52, 469.35) * mm, "end": v(1216.3, 480.14) * mm});
            skLineSegment(sketch, "E10.9.7.10", {"start": v(1234.98, 469.35) * mm, "end": v(1222.52, 469.35) * mm});
            skLineSegment(sketch, "E10.12.7.10", {"start": v(1241.22, 480.14) * mm, "end": v(1234.98, 469.35) * mm});
            skLineSegment(sketch, "E10.15.7.10", {"start": v(1234.98, 490.93) * mm, "end": v(1241.22, 480.14) * mm});
            skLineSegment(sketch, "E10.0.7.11", {"start": v(1222.52, 319.48) * mm, "end": v(1234.98, 319.48) * mm});
            skLineSegment(sketch, "E10.3.7.11", {"start": v(1216.3, 308.7) * mm, "end": v(1222.52, 319.48) * mm});
            skLineSegment(sketch, "E10.6.7.11", {"start": v(1222.52, 297.9) * mm, "end": v(1216.3, 308.7) * mm});
            skLineSegment(sketch, "E10.9.7.11", {"start": v(1234.98, 297.9) * mm, "end": v(1222.52, 297.9) * mm});
            skLineSegment(sketch, "E10.12.7.11", {"start": v(1241.22, 308.7) * mm, "end": v(1234.98, 297.9) * mm});
            skLineSegment(sketch, "E10.15.7.11", {"start": v(1234.98, 319.48) * mm, "end": v(1241.22, 308.7) * mm});
            skLineSegment(sketch, "E10.0.8.8", {"start": v(1387.62, 833.83) * mm, "end": v(1400.08, 833.83) * mm});
            skLineSegment(sketch, "E10.3.8.8", {"start": v(1381.4, 823.04) * mm, "end": v(1387.62, 833.83) * mm});
            skLineSegment(sketch, "E10.6.8.8", {"start": v(1387.62, 812.25) * mm, "end": v(1381.4, 823.04) * mm});
            skLineSegment(sketch, "E10.9.8.8", {"start": v(1400.08, 812.25) * mm, "end": v(1387.62, 812.25) * mm});
            skLineSegment(sketch, "E10.12.8.8", {"start": v(1406.32, 823.04) * mm, "end": v(1400.08, 812.25) * mm});
            skLineSegment(sketch, "E10.15.8.8", {"start": v(1400.08, 833.83) * mm, "end": v(1406.32, 823.04) * mm});
            skLineSegment(sketch, "E10.0.8.9", {"start": v(1387.62, 662.38) * mm, "end": v(1400.08, 662.38) * mm});
            skLineSegment(sketch, "E10.3.8.9", {"start": v(1381.4, 651.6) * mm, "end": v(1387.62, 662.38) * mm});
            skLineSegment(sketch, "E10.6.8.9", {"start": v(1387.62, 640.8) * mm, "end": v(1381.4, 651.6) * mm});
            skLineSegment(sketch, "E10.9.8.9", {"start": v(1400.08, 640.8) * mm, "end": v(1387.62, 640.8) * mm});
            skLineSegment(sketch, "E10.12.8.9", {"start": v(1406.32, 651.6) * mm, "end": v(1400.08, 640.8) * mm});
            skLineSegment(sketch, "E10.15.8.9", {"start": v(1400.08, 662.38) * mm, "end": v(1406.32, 651.6) * mm});
            skLineSegment(sketch, "E10.0.8.10", {"start": v(1387.62, 490.93) * mm, "end": v(1400.08, 490.93) * mm});
            skLineSegment(sketch, "E10.3.8.10", {"start": v(1381.4, 480.14) * mm, "end": v(1387.62, 490.93) * mm});
            skLineSegment(sketch, "E10.6.8.10", {"start": v(1387.62, 469.35) * mm, "end": v(1381.4, 480.14) * mm});
            skLineSegment(sketch, "E10.9.8.10", {"start": v(1400.08, 469.35) * mm, "end": v(1387.62, 469.35) * mm});
            skLineSegment(sketch, "E10.12.8.10", {"start": v(1406.32, 480.14) * mm, "end": v(1400.08, 469.35) * mm});
            skLineSegment(sketch, "E10.15.8.10", {"start": v(1400.08, 490.93) * mm, "end": v(1406.32, 480.14) * mm});
            skLineSegment(sketch, "E10.0.8.11", {"start": v(1387.62, 319.48) * mm, "end": v(1400.08, 319.48) * mm});
            skLineSegment(sketch, "E10.3.8.11", {"start": v(1381.4, 308.7) * mm, "end": v(1387.62, 319.48) * mm});
            skLineSegment(sketch, "E10.6.8.11", {"start": v(1387.62, 297.9) * mm, "end": v(1381.4, 308.7) * mm});
            skLineSegment(sketch, "E10.9.8.11", {"start": v(1400.08, 297.9) * mm, "end": v(1387.62, 297.9) * mm});
            skLineSegment(sketch, "E10.12.8.11", {"start": v(1406.32, 308.7) * mm, "end": v(1400.08, 297.9) * mm});
            skLineSegment(sketch, "E10.15.8.11", {"start": v(1400.08, 319.48) * mm, "end": v(1406.32, 308.7) * mm});
            skLineSegment(sketch, "E10.0.9.8", {"start": v(1552.72, 833.83) * mm, "end": v(1565.18, 833.83) * mm});
            skLineSegment(sketch, "E10.3.9.8", {"start": v(1546.5, 823.04) * mm, "end": v(1552.72, 833.83) * mm});
            skLineSegment(sketch, "E10.6.9.8", {"start": v(1552.72, 812.25) * mm, "end": v(1546.5, 823.04) * mm});
            skLineSegment(sketch, "E10.9.9.8", {"start": v(1565.18, 812.25) * mm, "end": v(1552.72, 812.25) * mm});
            skLineSegment(sketch, "E10.12.9.8", {"start": v(1571.42, 823.04) * mm, "end": v(1565.18, 812.25) * mm});
            skLineSegment(sketch, "E10.15.9.8", {"start": v(1565.18, 833.83) * mm, "end": v(1571.42, 823.04) * mm});
            skLineSegment(sketch, "E10.0.9.9", {"start": v(1552.72, 662.38) * mm, "end": v(1565.18, 662.38) * mm});
            skLineSegment(sketch, "E10.3.9.9", {"start": v(1546.5, 651.6) * mm, "end": v(1552.72, 662.38) * mm});
            skLineSegment(sketch, "E10.6.9.9", {"start": v(1552.72, 640.8) * mm, "end": v(1546.5, 651.6) * mm});
            skLineSegment(sketch, "E10.9.9.9", {"start": v(1565.18, 640.8) * mm, "end": v(1552.72, 640.8) * mm});
            skLineSegment(sketch, "E10.12.9.9", {"start": v(1571.42, 651.6) * mm, "end": v(1565.18, 640.8) * mm});
            skLineSegment(sketch, "E10.15.9.9", {"start": v(1565.18, 662.38) * mm, "end": v(1571.42, 651.6) * mm});
            skLineSegment(sketch, "E10.0.9.10", {"start": v(1552.72, 490.93) * mm, "end": v(1565.18, 490.93) * mm});
            skLineSegment(sketch, "E10.3.9.10", {"start": v(1546.5, 480.14) * mm, "end": v(1552.72, 490.93) * mm});
            skLineSegment(sketch, "E10.6.9.10", {"start": v(1552.72, 469.35) * mm, "end": v(1546.5, 480.14) * mm});
            skLineSegment(sketch, "E10.9.9.10", {"start": v(1565.18, 469.35) * mm, "end": v(1552.72, 469.35) * mm});
            skLineSegment(sketch, "E10.12.9.10", {"start": v(1571.42, 480.14) * mm, "end": v(1565.18, 469.35) * mm});
            skLineSegment(sketch, "E10.15.9.10", {"start": v(1565.18, 490.93) * mm, "end": v(1571.42, 480.14) * mm});
            skLineSegment(sketch, "E10.0.9.11", {"start": v(1552.72, 319.48) * mm, "end": v(1565.18, 319.48) * mm});
            skLineSegment(sketch, "E10.3.9.11", {"start": v(1546.5, 308.7) * mm, "end": v(1552.72, 319.48) * mm});
            skLineSegment(sketch, "E10.6.9.11", {"start": v(1552.72, 297.9) * mm, "end": v(1546.5, 308.7) * mm});
            skLineSegment(sketch, "E10.9.9.11", {"start": v(1565.18, 297.9) * mm, "end": v(1552.72, 297.9) * mm});
            skLineSegment(sketch, "E10.12.9.11", {"start": v(1571.42, 308.7) * mm, "end": v(1565.18, 297.9) * mm});
            skLineSegment(sketch, "E10.15.9.11", {"start": v(1565.18, 319.48) * mm, "end": v(1571.42, 308.7) * mm});
            skLineSegment(sketch, "E11.0.0.12", {"start": v(66.82, 148.03) * mm, "end": v(79.28, 148.03) * mm});
            skLineSegment(sketch, "E11.3.0.12", {"start": v(60.6, 137.24) * mm, "end": v(66.82, 148.03) * mm});
            skLineSegment(sketch, "E11.6.0.12", {"start": v(66.82, 126.45) * mm, "end": v(60.6, 137.24) * mm});
            skLineSegment(sketch, "E11.9.0.12", {"start": v(79.28, 126.45) * mm, "end": v(66.82, 126.45) * mm});
            skLineSegment(sketch, "E11.12.0.12", {"start": v(85.52, 137.24) * mm, "end": v(79.28, 126.45) * mm});
            skLineSegment(sketch, "E11.15.0.12", {"start": v(79.28, 148.03) * mm, "end": v(85.52, 137.24) * mm});
            skLineSegment(sketch, "E11.0.1.12", {"start": v(231.92, 148.03) * mm, "end": v(244.38, 148.03) * mm});
            skLineSegment(sketch, "E11.3.1.12", {"start": v(225.7, 137.24) * mm, "end": v(231.92, 148.03) * mm});
            skLineSegment(sketch, "E11.6.1.12", {"start": v(231.92, 126.45) * mm, "end": v(225.7, 137.24) * mm});
            skLineSegment(sketch, "E11.9.1.12", {"start": v(244.38, 126.45) * mm, "end": v(231.92, 126.45) * mm});
            skLineSegment(sketch, "E11.12.1.12", {"start": v(250.62, 137.24) * mm, "end": v(244.38, 126.45) * mm});
            skLineSegment(sketch, "E11.15.1.12", {"start": v(244.38, 148.03) * mm, "end": v(250.62, 137.24) * mm});
            skLineSegment(sketch, "E11.0.2.12", {"start": v(397.02, 148.03) * mm, "end": v(409.48, 148.03) * mm});
            skLineSegment(sketch, "E11.3.2.12", {"start": v(390.8, 137.24) * mm, "end": v(397.02, 148.03) * mm});
            skLineSegment(sketch, "E11.6.2.12", {"start": v(397.02, 126.45) * mm, "end": v(390.8, 137.24) * mm});
            skLineSegment(sketch, "E11.9.2.12", {"start": v(409.48, 126.45) * mm, "end": v(397.02, 126.45) * mm});
            skLineSegment(sketch, "E11.12.2.12", {"start": v(415.72, 137.24) * mm, "end": v(409.48, 126.45) * mm});
            skLineSegment(sketch, "E11.15.2.12", {"start": v(409.48, 148.03) * mm, "end": v(415.72, 137.24) * mm});
            skLineSegment(sketch, "E11.0.3.12", {"start": v(562.12, 148.03) * mm, "end": v(574.58, 148.03) * mm});
            skLineSegment(sketch, "E11.3.3.12", {"start": v(555.9, 137.24) * mm, "end": v(562.12, 148.03) * mm});
            skLineSegment(sketch, "E11.6.3.12", {"start": v(562.12, 126.45) * mm, "end": v(555.9, 137.24) * mm});
            skLineSegment(sketch, "E11.9.3.12", {"start": v(574.58, 126.45) * mm, "end": v(562.12, 126.45) * mm});
            skLineSegment(sketch, "E11.12.3.12", {"start": v(580.82, 137.24) * mm, "end": v(574.58, 126.45) * mm});
            skLineSegment(sketch, "E11.15.3.12", {"start": v(574.58, 148.03) * mm, "end": v(580.82, 137.24) * mm});
            skLineSegment(sketch, "E11.0.4.12", {"start": v(727.22, 148.03) * mm, "end": v(739.68, 148.03) * mm});
            skLineSegment(sketch, "E11.3.4.12", {"start": v(721, 137.24) * mm, "end": v(727.22, 148.03) * mm});
            skLineSegment(sketch, "E11.6.4.12", {"start": v(727.22, 126.45) * mm, "end": v(721, 137.24) * mm});
            skLineSegment(sketch, "E11.9.4.12", {"start": v(739.68, 126.45) * mm, "end": v(727.22, 126.45) * mm});
            skLineSegment(sketch, "E11.12.4.12", {"start": v(745.92, 137.24) * mm, "end": v(739.68, 126.45) * mm});
            skLineSegment(sketch, "E11.15.4.12", {"start": v(739.68, 148.03) * mm, "end": v(745.92, 137.24) * mm});
            skLineSegment(sketch, "E11.0.5.12", {"start": v(892.32, 148.03) * mm, "end": v(904.78, 148.03) * mm});
            skLineSegment(sketch, "E11.3.5.12", {"start": v(886.1, 137.24) * mm, "end": v(892.32, 148.03) * mm});
            skLineSegment(sketch, "E11.6.5.12", {"start": v(892.32, 126.45) * mm, "end": v(886.1, 137.24) * mm});
            skLineSegment(sketch, "E11.9.5.12", {"start": v(904.78, 126.45) * mm, "end": v(892.32, 126.45) * mm});
            skLineSegment(sketch, "E11.12.5.12", {"start": v(911.02, 137.24) * mm, "end": v(904.78, 126.45) * mm});
            skLineSegment(sketch, "E11.15.5.12", {"start": v(904.78, 148.03) * mm, "end": v(911.02, 137.24) * mm});
            skLineSegment(sketch, "E11.0.6.12", {"start": v(1057.42, 148.03) * mm, "end": v(1069.88, 148.03) * mm});
            skLineSegment(sketch, "E11.3.6.12", {"start": v(1051.2, 137.24) * mm, "end": v(1057.42, 148.03) * mm});
            skLineSegment(sketch, "E11.6.6.12", {"start": v(1057.42, 126.45) * mm, "end": v(1051.2, 137.24) * mm});
            skLineSegment(sketch, "E11.9.6.12", {"start": v(1069.88, 126.45) * mm, "end": v(1057.42, 126.45) * mm});
            skLineSegment(sketch, "E11.12.6.12", {"start": v(1076.12, 137.24) * mm, "end": v(1069.88, 126.45) * mm});
            skLineSegment(sketch, "E11.15.6.12", {"start": v(1069.88, 148.03) * mm, "end": v(1076.12, 137.24) * mm});
            skLineSegment(sketch, "E11.0.7.12", {"start": v(1222.52, 148.03) * mm, "end": v(1234.98, 148.03) * mm});
            skLineSegment(sketch, "E11.3.7.12", {"start": v(1216.3, 137.24) * mm, "end": v(1222.52, 148.03) * mm});
            skLineSegment(sketch, "E11.6.7.12", {"start": v(1222.52, 126.45) * mm, "end": v(1216.3, 137.24) * mm});
            skLineSegment(sketch, "E11.9.7.12", {"start": v(1234.98, 126.45) * mm, "end": v(1222.52, 126.45) * mm});
            skLineSegment(sketch, "E11.12.7.12", {"start": v(1241.22, 137.24) * mm, "end": v(1234.98, 126.45) * mm});
            skLineSegment(sketch, "E11.15.7.12", {"start": v(1234.98, 148.03) * mm, "end": v(1241.22, 137.24) * mm});
            skLineSegment(sketch, "E11.0.8.12", {"start": v(1387.62, 148.03) * mm, "end": v(1400.08, 148.03) * mm});
            skLineSegment(sketch, "E11.3.8.12", {"start": v(1381.4, 137.24) * mm, "end": v(1387.62, 148.03) * mm});
            skLineSegment(sketch, "E11.6.8.12", {"start": v(1387.62, 126.45) * mm, "end": v(1381.4, 137.24) * mm});
            skLineSegment(sketch, "E11.9.8.12", {"start": v(1400.08, 126.45) * mm, "end": v(1387.62, 126.45) * mm});
            skLineSegment(sketch, "E11.12.8.12", {"start": v(1406.32, 137.24) * mm, "end": v(1400.08, 126.45) * mm});
            skLineSegment(sketch, "E11.15.8.12", {"start": v(1400.08, 148.03) * mm, "end": v(1406.32, 137.24) * mm});
            skLineSegment(sketch, "E11.0.9.12", {"start": v(1552.72, 148.03) * mm, "end": v(1565.18, 148.03) * mm});
            skLineSegment(sketch, "E11.3.9.12", {"start": v(1546.5, 137.24) * mm, "end": v(1552.72, 148.03) * mm});
            skLineSegment(sketch, "E11.6.9.12", {"start": v(1552.72, 126.45) * mm, "end": v(1546.5, 137.24) * mm});
            skLineSegment(sketch, "E11.9.9.12", {"start": v(1565.18, 126.45) * mm, "end": v(1552.72, 126.45) * mm});
            skLineSegment(sketch, "E11.12.9.12", {"start": v(1571.42, 137.24) * mm, "end": v(1565.18, 126.45) * mm});
            skLineSegment(sketch, "E11.15.9.12", {"start": v(1565.18, 148.03) * mm, "end": v(1571.42, 137.24) * mm});
            skSolve(sketch);
        }
        {
            var Q0;
            Q0 = qSketchRegion(id + "F4", true);
            extrude(context, id + "F5", {"entities" : qUnion([Q0]), "operationType" : NewBodyOperationType.REMOVE, "oppositeDirection" : true, "depth" : 6.35 * mm});
        }
    });
